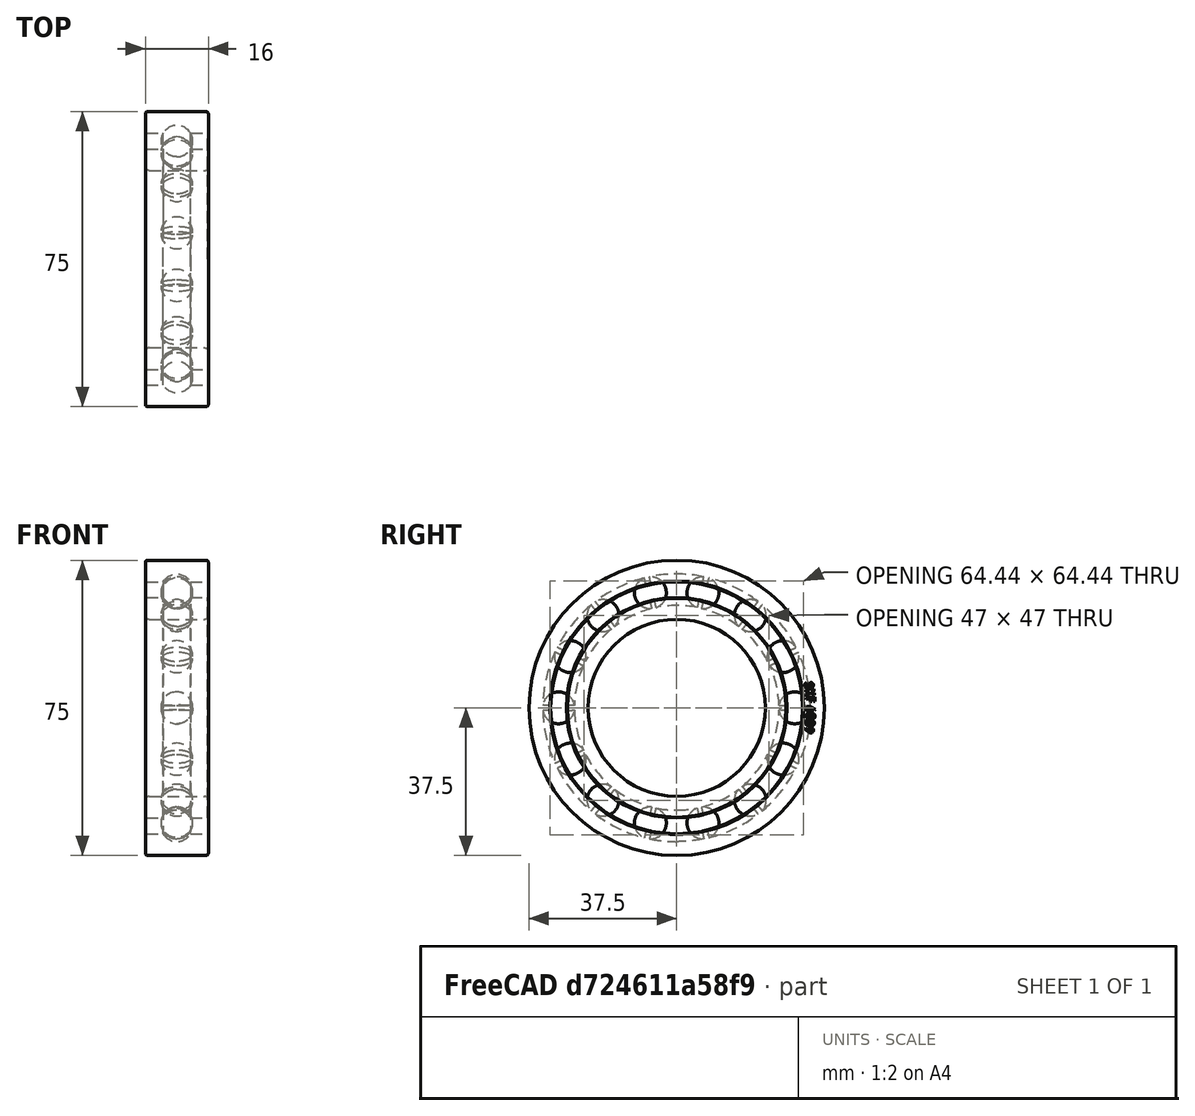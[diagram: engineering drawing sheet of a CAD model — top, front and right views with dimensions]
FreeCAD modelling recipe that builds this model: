
FCSTD DOCUMENT  (FreeCAD 0.21R33675 (Git))
Label: recicladora
License: Creative Commons Attribution-ShareAlike
LicenseURL: http://creativecommons.org/licenses/by-sa/4.0/
objects: App::Link×158, App::DocumentObjectGroup×3, App::FeaturePython×2, PartDesign::CoordinateSystem×2, App::Part×2, Part::Feature×1
note: 3 computed .brp shape members not serialized (recipe doc carries the construction recipe); baked Part::Feature solids carry a one-line shape summary decoded from their .brp
EXTERNAL_REF file=recicladora_eje.FCStd obj=LCS_eje_central_entrada
EXTERNAL_REF file=recicladora_eje.FCStd obj=EjeCentral
EXTERNAL_REF file=recicladora_eje.FCStd obj=LCS_eje_central_salida
EXTERNAL_REF file=recicladora_cuchillas.FCStd obj=LCS_separador_entrada
EXTERNAL_REF file=recicladora_cuchillas.FCStd obj=Body007
EXTERNAL_REF file=recicladora_piezas_fijas.FCStd obj=LCS_placa_caja_salida
EXTERNAL_REF file=recicladora_piezas_fijas.FCStd obj=CuchillaFija001
EXTERNAL_REF file=recicladora_piezas_fijas.FCStd obj=LCS_eje_central
EXTERNAL_REF file=recicladora_piezas_fijas.FCStd obj=Body
EXTERNAL_REF file=recicladora_piezas_fijas.FCStd obj=LCS_cuchilla_fija_separador_salida
EXTERNAL_REF file=recicladora_piezas_fijas.FCStd obj=LCS_eje_central001
EXTERNAL_REF file=recicladora_piezas_fijas.FCStd obj=CuchillaFija
EXTERNAL_REF file=recicladora_piezas_fijas.FCStd obj=LCS_cuchilla_fija_salida
EXTERNAL_REF file=recicladora_cuchillas.FCStd obj=LCS_separador
EXTERNAL_REF file=recicladora_cuchillas.FCStd obj=Body008
EXTERNAL_REF file=recicladora_cuchillas.FCStd obj=LCS_cuchilla_entrada
EXTERNAL_REF file=recicladora_cuchillas.FCStd obj=LCS_separador_salida
EXTERNAL_REF file=recicladora_cuchillas.FCStd obj=Body001
EXTERNAL_REF file=recicladora_cuchillas.FCStd obj=LCS_cuchilla_salida
EXTERNAL_REF file=recicladora_cuchillas.FCStd obj=LCS_cuchilla_entrada001
EXTERNAL_REF file=recicladora_cuchillas.FCStd obj=Body009
EXTERNAL_REF file=recicladora_cuchillas.FCStd obj=LCS_cuchilla_salida001
EXTERNAL_REF file=recicladora_cuchillas.FCStd obj=LCS_cuchilla_entrada002
EXTERNAL_REF file=recicladora_cuchillas.FCStd obj=Body010
EXTERNAL_REF file=recicladora_cuchillas.FCStd obj=LCS_cuchilla_salida002
EXTERNAL_REF file=recicladora_cuchillas.FCStd obj=LCS_cuchilla_entrada003
EXTERNAL_REF file=recicladora_cuchillas.FCStd obj=Body011
EXTERNAL_REF file=recicladora_cuchillas.FCStd obj=LCS_cuchilla_salida003
EXTERNAL_REF file=recicladora_cuchillas.FCStd obj=LCS_cuchilla_entrada004
EXTERNAL_REF file=recicladora_cuchillas.FCStd obj=Body012
EXTERNAL_REF file=recicladora_cuchillas.FCStd obj=LCS_cuchilla_salida004
EXTERNAL_REF file=recicladora_cuchillas.FCStd obj=LCS_cuchilla_entrada005
EXTERNAL_REF file=recicladora_cuchillas.FCStd obj=Body013
EXTERNAL_REF file=recicladora_cuchillas.FCStd obj=LCS_cuchilla_salida005
EXTERNAL_REF file=recicladora_piezas_fijas.FCStd obj=LCS_eje_central003
EXTERNAL_REF file=recicladora_piezas_fijas.FCStd obj=CuchillaFija002
EXTERNAL_REF file=recicladora_cuchillas.FCStd obj=LCS_separador_entrada001
EXTERNAL_REF file=recicladora_cuchillas.FCStd obj=Body014
EXTERNAL_REF file=recicladora_piezas_fijas.FCStd obj=LCS_Placa_Fondo_Entrada
EXTERNAL_REF file=recicladora_piezas_fijas.FCStd obj=LCS_Placa_Salida_Fondo
EXTERNAL_REF file=recicladora_piezas_fijas.FCStd obj=Body001
EXTERNAL_REF file=recicladora_piezas_fijas.FCStd obj=LCS_Placa_Union_Entrada
EXTERNAL_REF file=recicladora_piezas_fijas.FCStd obj=LCS_Placa_union_salida
EXTERNAL_REF file=recicladora_piezas_fijas.FCStd obj=Body002
EXTERNAL_REF file=recicladora_piezas_fijas.FCStd obj=LCS_Paca_union_entrada_2
EXTERNAL_REF file=recicladora_piezas_fijas.FCStd obj=LCS_Placa_union_salida001

FEATURE [App::FeaturePython] dd  # WARN: FeaturePython — macro-defined, semantics opaque (R4)
  DynamicData = Created with DynamicData (v2.46) workbench. | This is a simple container object built | for holding custom properties.
  ddAnchoHex = 25
  ddAnchoPlaca = 3
  ddDiametroExternoHex = 28.8675
  ddDiametroUnion = 10
  ddLargoCono = 18.8675
  ddLargoEje = 100
  ddLargoUnion = 20
  expr: ddDiametroExternoHex = ddAnchoHex / cos(30)
  expr: ddLargoCono = ddDiametroExternoHex - ddDiametroUnion
FEATURE [PartDesign::CoordinateSystem] LCS_Origin
  AttacherType = Attacher::AttachEngine3D
  MapMode = 2
  Support = -> [X_Axis001]
FEATURE [App::DocumentObjectGroup] Constraints
FEATURE [App::FeaturePython] Variables  # WARN: FeaturePython — macro-defined, semantics opaque (R4)
  Type = App::PropertyContainer
  angulo = 6
FEATURE [App::DocumentObjectGroup] Configurations
FEATURE [Part::Feature] Part__Feature  label="45mm Bearing SKF 6009 (RS 286-7754)"
  shape: bbox 16 x 81.18 x 81.18 mm, 195 faces (baked)
FEATURE [PartDesign::CoordinateSystem] LCS_0  label="LCS_rodamiento"
  AttacherType = Attacher::AttachEngine3D
  MapMode = 11
  Placement = pos=(1e-15,0,-7.1e-15) rot=(0.57735,0.57735,-0.57735;4.18879rad)
  Support = -> [Part__Feature]
FEATURE [App::Part] Rodamiento
  Group = -> [LCS_0,Part__Feature]
  Origin = -> Origin
FEATURE [App::DocumentObjectGroup] Parts
  Group = -> [Rodamiento]
FEATURE [App::Link] EjeCentral
  AssemblyType = Part::Link
  AttachedBy = #LCS_eje_central_entrada
  AttachedTo = Parent Assembly#LCS_Origin
  AttachmentOffset = pos=(0,0,0) rot=(0,0,1;0.418879rad)
  LinkPlacement = pos=(2e-16,1e-16,85.5354) rot=(0,0,-1;1.15192rad)
  LinkedObject = -> <external recicladora_eje.FCStd>#EjeCentral
  Placement = pos=(2e-16,1e-16,85.5354) rot=(0,0,-1;1.15192rad)
  SolverId = Asm4EE
  expr: .AttachmentOffset.Rotation.Angle = -Variables.angulo + 30
  expr: Placement = LCS_Origin.Placement * AttachmentOffset * recicladora_eje#LCS_eje_central_entrada.Placement ^ -1
FEATURE [App::Link] Rodamiento001
  AssemblyType = Part::Link
  AttachedBy = #LCS_0
  AttachedTo = EjeCentral#LCS_eje_central_salida
  AttachmentOffset = pos=(0,0,-13) rot=(0,0,1;0rad)
  LinkPlacement = pos=(-3.7e-15,-1.7e-15,72.5354) rot=(0.699253,0.148631,-0.699253;2.84649rad)
  LinkedObject = -> Rodamiento
  Placement = pos=(-3.7e-15,-1.7e-15,72.5354) rot=(0.699253,0.148631,-0.699253;2.84649rad)
  SolverId = Asm4EE
  expr: Placement = EjeCentral.Placement * recicladora_eje#LCS_eje_central_salida.Placement * AttachmentOffset * LCS_0.Placement ^ -1
FEATURE [App::Link] SeparadorCuchillaInicial
  AssemblyType = Part::Link
  AttachedBy = #LCS_separador_entrada
  AttachedTo = EjeCentral#LCS_eje_central_salida
  AttachmentOffset = pos=(0,0,0) rot=(0,0,1;0.10472rad)
  LinkPlacement = pos=(-2.9e-15,-1.7e-15,85.5354) rot=(0,0,-1;2.61799rad)
  LinkedObject = -> <external recicladora_cuchillas.FCStd>#Body007
  Placement = pos=(-2.9e-15,-1.7e-15,85.5354) rot=(0,0,-1;2.61799rad)
  SolverId = Asm4EE
  expr: .AttachmentOffset.Rotation.Angle = Variables.angulo
  expr: Placement = EjeCentral.Placement * recicladora_eje#LCS_eje_central_salida.Placement * AttachmentOffset * recicladora_cuchillas#LCS_separador_entrada.Placement ^ -1
FEATURE [App::Link] PlacaCaja
  AssemblyType = Part::Link
  AttachedBy = #LCS_placa_caja_salida
  AttachedTo = Parent Assembly#LCS_Origin
  AttachmentOffset = pos=(0,0,88.535) rot=(0,0,1;0rad)
  LinkPlacement = pos=(65,-65,87.035) rot=(0,0,1;0rad)
  LinkedObject = -> <external recicladora_piezas_fijas.FCStd>#CuchillaFija001
  Placement = pos=(65,-65,87.035) rot=(0,0,1;0rad)
  SolverId = Asm4EE
  expr: Placement = LCS_Origin.Placement * AttachmentOffset * recicladora_piezas_fijas#LCS_placa_caja_salida.Placement ^ -1
FEATURE [App::Link] CuchillaFijaSeparador
  AssemblyType = Part::Link
  AttachedBy = #LCS_eje_central
  AttachedTo = PlacaCaja#LCS_placa_caja_salida
  LinkPlacement = pos=(65,-65,88.535) rot=(0,0,1;0rad)
  LinkedObject = -> <external recicladora_piezas_fijas.FCStd>#Body
  Placement = pos=(65,-65,88.535) rot=(0,0,1;0rad)
  SolverId = Asm4EE
  expr: Placement = PlacaCaja.Placement * recicladora_piezas_fijas#LCS_placa_caja_salida.Placement * AttachmentOffset * recicladora_piezas_fijas#LCS_eje_central.Placement ^ -1
FEATURE [App::Link] CuchillaFija
  AssemblyType = Part::Link
  AttachedBy = #LCS_eje_central001
  AttachedTo = CuchillaFijaSeparador#LCS_cuchilla_fija_separador_salida
  LinkPlacement = pos=(65,-65,90.035) rot=(0,0,1;0rad)
  LinkedObject = -> <external recicladora_piezas_fijas.FCStd>#CuchillaFija
  Placement = pos=(65,-65,90.035) rot=(0,0,1;0rad)
  SolverId = Asm4EE
  expr: Placement = CuchillaFijaSeparador.Placement * recicladora_piezas_fijas#LCS_cuchilla_fija_separador_salida.Placement * AttachmentOffset * recicladora_piezas_fijas#LCS_eje_central001.Placement ^ -1
FEATURE [App::Link] CuchillaFijaSeparador001
  AssemblyType = Part::Link
  AttachedBy = #LCS_eje_central
  AttachedTo = CuchillaFija#LCS_cuchilla_fija_salida
  LinkPlacement = pos=(65,-65,91.535) rot=(0,0,1;0rad)
  LinkedObject = -> <external recicladora_piezas_fijas.FCStd>#Body
  Placement = pos=(65,-65,91.535) rot=(0,0,1;0rad)
  SolverId = Asm4EE
  expr: Placement = CuchillaFija.Placement * recicladora_piezas_fijas#LCS_cuchilla_fija_salida.Placement * AttachmentOffset * recicladora_piezas_fijas#LCS_eje_central.Placement ^ -1
FEATURE [App::Link] CuchillaFija001
  AssemblyType = Part::Link
  AttachedBy = #LCS_eje_central001
  AttachedTo = CuchillaFijaSeparador001#LCS_cuchilla_fija_separador_salida
  LinkPlacement = pos=(65,-65,93.035) rot=(0,0,1;0rad)
  LinkedObject = -> <external recicladora_piezas_fijas.FCStd>#CuchillaFija
  Placement = pos=(65,-65,93.035) rot=(0,0,1;0rad)
  SolverId = Asm4EE
  expr: Placement = CuchillaFijaSeparador001.Placement * recicladora_piezas_fijas#LCS_cuchilla_fija_separador_salida.Placement * AttachmentOffset * recicladora_piezas_fijas#LCS_eje_central001.Placement ^ -1
FEATURE [App::Link] CuchillaFijaSeparador002
  AssemblyType = Part::Link
  AttachedBy = #LCS_eje_central
  AttachedTo = CuchillaFija001#LCS_cuchilla_fija_salida
  LinkPlacement = pos=(65,-65,94.535) rot=(0,0,1;0rad)
  LinkedObject = -> <external recicladora_piezas_fijas.FCStd>#Body
  Placement = pos=(65,-65,94.535) rot=(0,0,1;0rad)
  SolverId = Asm4EE
  expr: Placement = CuchillaFija001.Placement * recicladora_piezas_fijas#LCS_cuchilla_fija_salida.Placement * AttachmentOffset * recicladora_piezas_fijas#LCS_eje_central.Placement ^ -1
FEATURE [App::Link] CuchillaFija002
  AssemblyType = Part::Link
  AttachedBy = #LCS_eje_central001
  AttachedTo = CuchillaFijaSeparador002#LCS_cuchilla_fija_separador_salida
  LinkPlacement = pos=(65,-65,96.035) rot=(0,0,1;0rad)
  LinkedObject = -> <external recicladora_piezas_fijas.FCStd>#CuchillaFija
  Placement = pos=(65,-65,96.035) rot=(0,0,1;0rad)
  SolverId = Asm4EE
  expr: Placement = CuchillaFijaSeparador002.Placement * recicladora_piezas_fijas#LCS_cuchilla_fija_separador_salida.Placement * AttachmentOffset * recicladora_piezas_fijas#LCS_eje_central001.Placement ^ -1
FEATURE [App::Link] CuchillaFijaSeparador003
  AssemblyType = Part::Link
  AttachedBy = #LCS_eje_central
  AttachedTo = CuchillaFija002#LCS_cuchilla_fija_salida
  LinkPlacement = pos=(65,-65,97.535) rot=(0,0,1;0rad)
  LinkedObject = -> <external recicladora_piezas_fijas.FCStd>#Body
  Placement = pos=(65,-65,97.535) rot=(0,0,1;0rad)
  SolverId = Asm4EE
  expr: Placement = CuchillaFija002.Placement * recicladora_piezas_fijas#LCS_cuchilla_fija_salida.Placement * AttachmentOffset * recicladora_piezas_fijas#LCS_eje_central.Placement ^ -1
FEATURE [App::Link] CuchillaFija003
  AssemblyType = Part::Link
  AttachedBy = #LCS_eje_central001
  AttachedTo = CuchillaFijaSeparador003#LCS_cuchilla_fija_separador_salida
  LinkPlacement = pos=(65,-65,99.035) rot=(0,0,1;0rad)
  LinkedObject = -> <external recicladora_piezas_fijas.FCStd>#CuchillaFija
  Placement = pos=(65,-65,99.035) rot=(0,0,1;0rad)
  SolverId = Asm4EE
  expr: Placement = CuchillaFijaSeparador003.Placement * recicladora_piezas_fijas#LCS_cuchilla_fija_separador_salida.Placement * AttachmentOffset * recicladora_piezas_fijas#LCS_eje_central001.Placement ^ -1
FEATURE [App::Link] SeparadorCuchilla
  AssemblyType = Part::Link
  AttachedBy = #LCS_separador
  AttachedTo = PlacaCaja#LCS_placa_caja_salida
  AttachmentOffset = pos=(0,0,0) rot=(0,0,1;-0.10472rad)
  LinkPlacement = pos=(-1e-16,-1e-16,90.035) rot=(0.669131,-0.743145,0;3.14159rad)
  LinkedObject = -> <external recicladora_cuchillas.FCStd>#Body008
  Placement = pos=(-1e-16,-1e-16,90.035) rot=(0.669131,-0.743145,0;3.14159rad)
  SolverId = Asm4EE
  expr: .AttachmentOffset.Rotation.Angle = -Variables.angulo
  expr: Placement = PlacaCaja.Placement * recicladora_piezas_fijas#LCS_placa_caja_salida.Placement * AttachmentOffset * recicladora_cuchillas#LCS_separador.Placement ^ -1
FEATURE [App::Link] Cuchilla001
  AssemblyType = Part::Link
  AttachedBy = #LCS_cuchilla_entrada
  AttachedTo = SeparadorCuchilla#LCS_separador_salida
  LinkPlacement = pos=(-4e-16,-3.6e-15,90.035) rot=(0,0,1;4.60767rad)
  LinkedObject = -> <external recicladora_cuchillas.FCStd>#Body001
  Placement = pos=(-4e-16,-3.6e-15,90.035) rot=(0,0,1;4.60767rad)
  SolverId = Asm4EE
  expr: Placement = SeparadorCuchilla.Placement * recicladora_cuchillas#LCS_separador_salida.Placement * AttachmentOffset * recicladora_cuchillas#LCS_cuchilla_entrada.Placement ^ -1
FEATURE [App::Link] SeparadorCuchilla001
  AssemblyType = Part::Link
  AttachedBy = #LCS_separador
  AttachedTo = Cuchilla001#LCS_cuchilla_salida
  LinkPlacement = pos=(-4e-16,-3e-16,93.035) rot=(0.669131,-0.743145,0;3.14159rad)
  LinkedObject = -> <external recicladora_cuchillas.FCStd>#Body008
  Placement = pos=(-4e-16,-3e-16,93.035) rot=(0.669131,-0.743145,0;3.14159rad)
  SolverId = Asm4EE
  expr: Placement = Cuchilla001.Placement * recicladora_cuchillas#LCS_cuchilla_salida.Placement * AttachmentOffset * recicladora_cuchillas#LCS_separador.Placement ^ -1
FEATURE [App::Link] Cuchilla002
  AssemblyType = Part::Link
  AttachedBy = #LCS_cuchilla_entrada001
  AttachedTo = SeparadorCuchilla001#LCS_separador_salida
  LinkPlacement = pos=(-1e-15,-3.9e-15,93.035) rot=(0,0,1;4.43314rad)
  LinkedObject = -> <external recicladora_cuchillas.FCStd>#Body009
  Placement = pos=(-1e-15,-3.9e-15,93.035) rot=(0,0,1;4.43314rad)
  SolverId = Asm4EE
  expr: Placement = SeparadorCuchilla001.Placement * recicladora_cuchillas#LCS_separador_salida.Placement * AttachmentOffset * recicladora_cuchillas#LCS_cuchilla_entrada001.Placement ^ -1
FEATURE [App::Link] SeparadorCuchilla002
  AssemblyType = Part::Link
  AttachedBy = #LCS_separador
  AttachedTo = Cuchilla002#LCS_cuchilla_salida001
  LinkPlacement = pos=(-1.1e-15,-9e-16,96.035) rot=(0.669131,-0.743145,0;3.14159rad)
  LinkedObject = -> <external recicladora_cuchillas.FCStd>#Body008
  Placement = pos=(-1.1e-15,-9e-16,96.035) rot=(0.669131,-0.743145,0;3.14159rad)
  SolverId = Asm4EE
  expr: Placement = Cuchilla002.Placement * recicladora_cuchillas#LCS_cuchilla_salida001.Placement * AttachmentOffset * recicladora_cuchillas#LCS_separador.Placement ^ -1
FEATURE [App::Link] Cuchilla003
  AssemblyType = Part::Link
  AttachedBy = #LCS_cuchilla_entrada002
  AttachedTo = SeparadorCuchilla002#LCS_separador_salida
  LinkPlacement = pos=(-1.8e-15,-4.4e-15,96.035) rot=(0,0,1;4.2586rad)
  LinkedObject = -> <external recicladora_cuchillas.FCStd>#Body010
  Placement = pos=(-1.8e-15,-4.4e-15,96.035) rot=(0,0,1;4.2586rad)
  SolverId = Asm4EE
  expr: Placement = SeparadorCuchilla002.Placement * recicladora_cuchillas#LCS_separador_salida.Placement * AttachmentOffset * recicladora_cuchillas#LCS_cuchilla_entrada002.Placement ^ -1
FEATURE [App::Link] SeparadorCuchilla003
  AssemblyType = Part::Link
  AttachedBy = #LCS_separador
  AttachedTo = Cuchilla003#LCS_cuchilla_salida002
  LinkPlacement = pos=(-2e-15,-1.6e-15,99.035) rot=(0.669131,-0.743145,0;3.14159rad)
  LinkedObject = -> <external recicladora_cuchillas.FCStd>#Body008
  Placement = pos=(-2e-15,-1.6e-15,99.035) rot=(0.669131,-0.743145,0;3.14159rad)
  SolverId = Asm4EE
  expr: Placement = Cuchilla003.Placement * recicladora_cuchillas#LCS_cuchilla_salida002.Placement * AttachmentOffset * recicladora_cuchillas#LCS_separador.Placement ^ -1
FEATURE [App::Link] Cuchilla004
  AssemblyType = Part::Link
  AttachedBy = #LCS_cuchilla_entrada003
  AttachedTo = SeparadorCuchilla003#LCS_separador_salida
  LinkPlacement = pos=(-2.6e-15,-5.5e-15,99.035) rot=(0,0,1;4.08407rad)
  LinkedObject = -> <external recicladora_cuchillas.FCStd>#Body011
  Placement = pos=(-2.6e-15,-5.5e-15,99.035) rot=(0,0,1;4.08407rad)
  SolverId = Asm4EE
  expr: Placement = SeparadorCuchilla003.Placement * recicladora_cuchillas#LCS_separador_salida.Placement * AttachmentOffset * recicladora_cuchillas#LCS_cuchilla_entrada003.Placement ^ -1
FEATURE [App::Link] SeparadorCuchilla004
  AssemblyType = Part::Link
  AttachedBy = #LCS_separador
  AttachedTo = Cuchilla004#LCS_cuchilla_salida003
  LinkPlacement = pos=(-3.2e-15,-2.6e-15,102.035) rot=(0.669131,-0.743145,0;3.14159rad)
  LinkedObject = -> <external recicladora_cuchillas.FCStd>#Body008
  Placement = pos=(-3.2e-15,-2.6e-15,102.035) rot=(0.669131,-0.743145,0;3.14159rad)
  SolverId = Asm4EE
  expr: Placement = Cuchilla004.Placement * recicladora_cuchillas#LCS_cuchilla_salida003.Placement * AttachmentOffset * recicladora_cuchillas#LCS_separador.Placement ^ -1
FEATURE [App::Link] Cuchilla005
  AssemblyType = Part::Link
  AttachedBy = #LCS_cuchilla_entrada004
  AttachedTo = SeparadorCuchilla004#LCS_separador_salida
  LinkPlacement = pos=(-3.2e-15,-2.6e-15,102.035) rot=(0,0,1;3.90954rad)
  LinkedObject = -> <external recicladora_cuchillas.FCStd>#Body012
  Placement = pos=(-3.2e-15,-2.6e-15,102.035) rot=(0,0,1;3.90954rad)
  SolverId = Asm4EE
  expr: Placement = SeparadorCuchilla004.Placement * recicladora_cuchillas#LCS_separador_salida.Placement * AttachmentOffset * recicladora_cuchillas#LCS_cuchilla_entrada004.Placement ^ -1
FEATURE [App::Link] SeparadorCuchilla005
  AssemblyType = Part::Link
  AttachedBy = #LCS_separador
  AttachedTo = Cuchilla005#LCS_cuchilla_salida004
  LinkPlacement = pos=(-4.7e-15,-3.8e-15,105.035) rot=(0.669131,-0.743145,0;3.14159rad)
  LinkedObject = -> <external recicladora_cuchillas.FCStd>#Body008
  Placement = pos=(-4.7e-15,-3.8e-15,105.035) rot=(0.669131,-0.743145,0;3.14159rad)
  SolverId = Asm4EE
  expr: Placement = Cuchilla005.Placement * recicladora_cuchillas#LCS_cuchilla_salida004.Placement * AttachmentOffset * recicladora_cuchillas#LCS_separador.Placement ^ -1
FEATURE [App::Link] Cuchilla006
  AssemblyType = Part::Link
  AttachedBy = #LCS_cuchilla_entrada005
  AttachedTo = SeparadorCuchilla005#LCS_separador_salida
  LinkPlacement = pos=(-5.2e-15,-6.3e-15,105.035) rot=(0,0,1;3.73501rad)
  LinkedObject = -> <external recicladora_cuchillas.FCStd>#Body013
  Placement = pos=(-5.2e-15,-6.3e-15,105.035) rot=(0,0,1;3.73501rad)
  SolverId = Asm4EE
  expr: Placement = SeparadorCuchilla005.Placement * recicladora_cuchillas#LCS_separador_salida.Placement * AttachmentOffset * recicladora_cuchillas#LCS_cuchilla_entrada005.Placement ^ -1
FEATURE [App::Link] SeparadorCuchilla006
  AssemblyType = Part::Link
  AttachedBy = #LCS_separador
  AttachedTo = Cuchilla006#LCS_cuchilla_salida005
  LinkPlacement = pos=(-6.5e-15,-5.3e-15,108.035) rot=(0.669131,-0.743145,0;3.14159rad)
  LinkedObject = -> <external recicladora_cuchillas.FCStd>#Body008
  Placement = pos=(-6.5e-15,-5.3e-15,108.035) rot=(0.669131,-0.743145,0;3.14159rad)
  SolverId = Asm4EE
  expr: Placement = Cuchilla006.Placement * recicladora_cuchillas#LCS_cuchilla_salida005.Placement * AttachmentOffset * recicladora_cuchillas#LCS_separador.Placement ^ -1
FEATURE [App::Link] Cuchilla001001
  AssemblyType = Part::Link
  AttachedBy = #LCS_cuchilla_entrada
  AttachedTo = SeparadorCuchilla006#LCS_separador_salida
  AttachmentOffset = pos=(0,0,0) rot=(0,0,1;-1.0472rad)
  LinkPlacement = pos=(-9.7e-15,-6.7e-15,108.035) rot=(0,0,-1;2.72271rad)
  LinkedObject = -> <external recicladora_cuchillas.FCStd>#Body001
  Placement = pos=(-9.7e-15,-6.7e-15,108.035) rot=(0,0,-1;2.72271rad)
  SolverId = Asm4EE
  expr: Placement = SeparadorCuchilla006.Placement * recicladora_cuchillas#LCS_separador_salida.Placement * AttachmentOffset * recicladora_cuchillas#LCS_cuchilla_entrada.Placement ^ -1
FEATURE [App::Link] SeparadorCuchilla007
  AssemblyType = Part::Link
  AttachedBy = #LCS_separador
  AttachedTo = Cuchilla001001#LCS_cuchilla_salida
  LinkPlacement = pos=(-8.6e-15,-6.8e-15,111.035) rot=(-0.207912,0.978148,0;3.14159rad)
  LinkedObject = -> <external recicladora_cuchillas.FCStd>#Body008
  Placement = pos=(-8.6e-15,-6.8e-15,111.035) rot=(-0.207912,0.978148,0;3.14159rad)
  SolverId = Asm4EE
  expr: Placement = Cuchilla001001.Placement * recicladora_cuchillas#LCS_cuchilla_salida.Placement * AttachmentOffset * recicladora_cuchillas#LCS_separador.Placement ^ -1
FEATURE [App::Link] Cuchilla002001
  AssemblyType = Part::Link
  AttachedBy = #LCS_cuchilla_entrada001
  AttachedTo = SeparadorCuchilla007#LCS_separador_salida
  LinkPlacement = pos=(-1.19e-14,-8.1e-15,111.035) rot=(0,0,-1;2.89725rad)
  LinkedObject = -> <external recicladora_cuchillas.FCStd>#Body009
  Placement = pos=(-1.19e-14,-8.1e-15,111.035) rot=(0,0,-1;2.89725rad)
  SolverId = Asm4EE
  expr: Placement = SeparadorCuchilla007.Placement * recicladora_cuchillas#LCS_separador_salida.Placement * AttachmentOffset * recicladora_cuchillas#LCS_cuchilla_entrada001.Placement ^ -1
FEATURE [App::Link] SeparadorCuchilla008
  AssemblyType = Part::Link
  AttachedBy = #LCS_separador
  AttachedTo = Cuchilla002001#LCS_cuchilla_salida001
  LinkPlacement = pos=(-1.1e-14,-8.3e-15,114.035) rot=(-0.207912,0.978148,0;3.14159rad)
  LinkedObject = -> <external recicladora_cuchillas.FCStd>#Body008
  Placement = pos=(-1.1e-14,-8.3e-15,114.035) rot=(-0.207912,0.978148,0;3.14159rad)
  SolverId = Asm4EE
  expr: Placement = Cuchilla002001.Placement * recicladora_cuchillas#LCS_cuchilla_salida001.Placement * AttachmentOffset * recicladora_cuchillas#LCS_separador.Placement ^ -1
FEATURE [App::Link] Cuchilla003001
  AssemblyType = Part::Link
  AttachedBy = #LCS_cuchilla_entrada002
  AttachedTo = SeparadorCuchilla008#LCS_separador_salida
  LinkPlacement = pos=(-1.45e-14,-9.4e-15,114.035) rot=(0,0,-1;3.07178rad)
  LinkedObject = -> <external recicladora_cuchillas.FCStd>#Body010
  Placement = pos=(-1.45e-14,-9.4e-15,114.035) rot=(0,0,-1;3.07178rad)
  SolverId = Asm4EE
  expr: Placement = SeparadorCuchilla008.Placement * recicladora_cuchillas#LCS_separador_salida.Placement * AttachmentOffset * recicladora_cuchillas#LCS_cuchilla_entrada002.Placement ^ -1
FEATURE [App::Link] SeparadorCuchilla009
  AssemblyType = Part::Link
  AttachedBy = #LCS_separador
  AttachedTo = Cuchilla003001#LCS_cuchilla_salida002
  LinkPlacement = pos=(-1.38e-14,-9.6e-15,117.035) rot=(-0.207912,0.978148,0;3.14159rad)
  LinkedObject = -> <external recicladora_cuchillas.FCStd>#Body008
  Placement = pos=(-1.38e-14,-9.6e-15,117.035) rot=(-0.207912,0.978148,0;3.14159rad)
  SolverId = Asm4EE
  expr: Placement = Cuchilla003001.Placement * recicladora_cuchillas#LCS_cuchilla_salida002.Placement * AttachmentOffset * recicladora_cuchillas#LCS_separador.Placement ^ -1
FEATURE [App::Link] Cuchilla004001
  AssemblyType = Part::Link
  AttachedBy = #LCS_cuchilla_entrada003
  AttachedTo = SeparadorCuchilla009#LCS_separador_salida
  LinkPlacement = pos=(-1.75e-14,-1.1e-14,117.035) rot=(0,0,-1;3.24631rad)
  LinkedObject = -> <external recicladora_cuchillas.FCStd>#Body011
  Placement = pos=(-1.75e-14,-1.1e-14,117.035) rot=(0,0,-1;3.24631rad)
  SolverId = Asm4EE
  expr: Placement = SeparadorCuchilla009.Placement * recicladora_cuchillas#LCS_separador_salida.Placement * AttachmentOffset * recicladora_cuchillas#LCS_cuchilla_entrada003.Placement ^ -1
FEATURE [App::Link] SeparadorCuchilla010
  AssemblyType = Part::Link
  AttachedBy = #LCS_separador
  AttachedTo = Cuchilla004001#LCS_cuchilla_salida003
  LinkPlacement = pos=(-1.69e-14,-1.08e-14,120.035) rot=(-0.207912,0.978148,0;3.14159rad)
  LinkedObject = -> <external recicladora_cuchillas.FCStd>#Body008
  Placement = pos=(-1.69e-14,-1.08e-14,120.035) rot=(-0.207912,0.978148,0;3.14159rad)
  SolverId = Asm4EE
  expr: Placement = Cuchilla004001.Placement * recicladora_cuchillas#LCS_cuchilla_salida003.Placement * AttachmentOffset * recicladora_cuchillas#LCS_separador.Placement ^ -1
FEATURE [App::Link] Cuchilla005001
  AssemblyType = Part::Link
  AttachedBy = #LCS_cuchilla_entrada004
  AttachedTo = SeparadorCuchilla010#LCS_separador_salida
  LinkPlacement = pos=(-1.69e-14,-1.08e-14,120.035) rot=(0,0,-1;3.42084rad)
  LinkedObject = -> <external recicladora_cuchillas.FCStd>#Body012
  Placement = pos=(-1.69e-14,-1.08e-14,120.035) rot=(0,0,-1;3.42084rad)
  SolverId = Asm4EE
  expr: Placement = SeparadorCuchilla010.Placement * recicladora_cuchillas#LCS_separador_salida.Placement * AttachmentOffset * recicladora_cuchillas#LCS_cuchilla_entrada004.Placement ^ -1
FEATURE [App::Link] SeparadorCuchilla011
  AssemblyType = Part::Link
  AttachedBy = #LCS_separador
  AttachedTo = Cuchilla005001#LCS_cuchilla_salida004
  LinkPlacement = pos=(-2.03e-14,-1.19e-14,123.035) rot=(-0.207912,0.978148,0;3.14159rad)
  LinkedObject = -> <external recicladora_cuchillas.FCStd>#Body008
  Placement = pos=(-2.03e-14,-1.19e-14,123.035) rot=(-0.207912,0.978148,0;3.14159rad)
  SolverId = Asm4EE
  expr: Placement = Cuchilla005001.Placement * recicladora_cuchillas#LCS_cuchilla_salida004.Placement * AttachmentOffset * recicladora_cuchillas#LCS_separador.Placement ^ -1
FEATURE [App::Link] Cuchilla006001
  AssemblyType = Part::Link
  AttachedBy = #LCS_cuchilla_entrada005
  AttachedTo = SeparadorCuchilla011#LCS_separador_salida
  LinkPlacement = pos=(-2.27e-14,-1.27e-14,123.035) rot=(0,0,-1;3.59538rad)
  LinkedObject = -> <external recicladora_cuchillas.FCStd>#Body013
  Placement = pos=(-2.27e-14,-1.27e-14,123.035) rot=(0,0,-1;3.59538rad)
  SolverId = Asm4EE
  expr: Placement = SeparadorCuchilla011.Placement * recicladora_cuchillas#LCS_separador_salida.Placement * AttachmentOffset * recicladora_cuchillas#LCS_cuchilla_entrada005.Placement ^ -1
FEATURE [App::Link] SeparadorCuchilla012
  AssemblyType = Part::Link
  AttachedBy = #LCS_separador
  AttachedTo = Cuchilla006001#LCS_cuchilla_salida005
  LinkPlacement = pos=(-2.41e-14,-1.28e-14,126.035) rot=(-0.207912,0.978148,0;3.14159rad)
  LinkedObject = -> <external recicladora_cuchillas.FCStd>#Body008
  Placement = pos=(-2.41e-14,-1.28e-14,126.035) rot=(-0.207912,0.978148,0;3.14159rad)
  SolverId = Asm4EE
  expr: Placement = Cuchilla006001.Placement * recicladora_cuchillas#LCS_cuchilla_salida005.Placement * AttachmentOffset * recicladora_cuchillas#LCS_separador.Placement ^ -1
FEATURE [App::Link] Cuchilla001002
  AssemblyType = Part::Link
  AttachedBy = #LCS_cuchilla_entrada
  AttachedTo = SeparadorCuchilla012#LCS_separador_salida
  AttachmentOffset = pos=(0,0,0) rot=(0,0,1;-1.0472rad)
  LinkPlacement = pos=(-2.7e-14,-1.07e-14,126.035) rot=(0,0,1;2.51327rad)
  LinkedObject = -> <external recicladora_cuchillas.FCStd>#Body001
  Placement = pos=(-2.7e-14,-1.07e-14,126.035) rot=(0,0,1;2.51327rad)
  SolverId = Asm4EE
  expr: Placement = SeparadorCuchilla012.Placement * recicladora_cuchillas#LCS_separador_salida.Placement * AttachmentOffset * recicladora_cuchillas#LCS_cuchilla_entrada.Placement ^ -1
FEATURE [App::Link] SeparadorCuchilla013
  AssemblyType = Part::Link
  AttachedBy = #LCS_separador
  AttachedTo = Cuchilla001002#LCS_cuchilla_salida
  LinkPlacement = pos=(-2.82e-14,-1.35e-14,129.035) rot=(-0.309017,-0.951057,0;3.14159rad)
  LinkedObject = -> <external recicladora_cuchillas.FCStd>#Body008
  Placement = pos=(-2.82e-14,-1.35e-14,129.035) rot=(-0.309017,-0.951057,0;3.14159rad)
  SolverId = Asm4EE
  expr: Placement = Cuchilla001002.Placement * recicladora_cuchillas#LCS_cuchilla_salida.Placement * AttachmentOffset * recicladora_cuchillas#LCS_separador.Placement ^ -1
FEATURE [App::Link] Cuchilla002002
  AssemblyType = Part::Link
  AttachedBy = #LCS_cuchilla_entrada001
  AttachedTo = SeparadorCuchilla013#LCS_separador_salida
  LinkPlacement = pos=(-3.1e-14,-1.13e-14,129.035) rot=(0,0,1;2.33874rad)
  LinkedObject = -> <external recicladora_cuchillas.FCStd>#Body009
  Placement = pos=(-3.1e-14,-1.13e-14,129.035) rot=(0,0,1;2.33874rad)
  SolverId = Asm4EE
  expr: Placement = SeparadorCuchilla013.Placement * recicladora_cuchillas#LCS_separador_salida.Placement * AttachmentOffset * recicladora_cuchillas#LCS_cuchilla_entrada001.Placement ^ -1
FEATURE [App::Link] SeparadorCuchilla014
  AssemblyType = Part::Link
  AttachedBy = #LCS_separador
  AttachedTo = Cuchilla002002#LCS_cuchilla_salida001
  LinkPlacement = pos=(-3.23e-14,-1.39e-14,132.035) rot=(-0.309017,-0.951057,0;3.14159rad)
  LinkedObject = -> <external recicladora_cuchillas.FCStd>#Body008
  Placement = pos=(-3.23e-14,-1.39e-14,132.035) rot=(-0.309017,-0.951057,0;3.14159rad)
  SolverId = Asm4EE
  expr: Placement = Cuchilla002002.Placement * recicladora_cuchillas#LCS_cuchilla_salida001.Placement * AttachmentOffset * recicladora_cuchillas#LCS_separador.Placement ^ -1
FEATURE [App::Link] Cuchilla003002
  AssemblyType = Part::Link
  AttachedBy = #LCS_cuchilla_entrada002
  AttachedTo = SeparadorCuchilla014#LCS_separador_salida
  LinkPlacement = pos=(-3.51e-14,-1.15e-14,132.035) rot=(0,0,1;2.16421rad)
  LinkedObject = -> <external recicladora_cuchillas.FCStd>#Body010
  Placement = pos=(-3.51e-14,-1.15e-14,132.035) rot=(0,0,1;2.16421rad)
  SolverId = Asm4EE
  expr: Placement = SeparadorCuchilla014.Placement * recicladora_cuchillas#LCS_separador_salida.Placement * AttachmentOffset * recicladora_cuchillas#LCS_cuchilla_entrada002.Placement ^ -1
FEATURE [App::Link] SeparadorCuchilla015
  AssemblyType = Part::Link
  AttachedBy = #LCS_separador
  AttachedTo = Cuchilla003002#LCS_cuchilla_salida002
  LinkPlacement = pos=(-3.65e-14,-1.39e-14,135.035) rot=(-0.309017,-0.951057,0;3.14159rad)
  LinkedObject = -> <external recicladora_cuchillas.FCStd>#Body008
  Placement = pos=(-3.65e-14,-1.39e-14,135.035) rot=(-0.309017,-0.951057,0;3.14159rad)
  SolverId = Asm4EE
  expr: Placement = Cuchilla003002.Placement * recicladora_cuchillas#LCS_cuchilla_salida002.Placement * AttachmentOffset * recicladora_cuchillas#LCS_separador.Placement ^ -1
FEATURE [App::Link] Cuchilla004002
  AssemblyType = Part::Link
  AttachedBy = #LCS_cuchilla_entrada003
  AttachedTo = SeparadorCuchilla015#LCS_separador_salida
  LinkPlacement = pos=(-3.96e-14,-1.14e-14,135.035) rot=(0,0,1;1.98968rad)
  LinkedObject = -> <external recicladora_cuchillas.FCStd>#Body011
  Placement = pos=(-3.96e-14,-1.14e-14,135.035) rot=(0,0,1;1.98968rad)
  SolverId = Asm4EE
  expr: Placement = SeparadorCuchilla015.Placement * recicladora_cuchillas#LCS_separador_salida.Placement * AttachmentOffset * recicladora_cuchillas#LCS_cuchilla_entrada003.Placement ^ -1
FEATURE [App::Link] SeparadorCuchilla016
  AssemblyType = Part::Link
  AttachedBy = #LCS_separador
  AttachedTo = Cuchilla004002#LCS_cuchilla_salida003
  LinkPlacement = pos=(-4.08e-14,-1.36e-14,138.035) rot=(-0.309017,-0.951057,0;3.14159rad)
  LinkedObject = -> <external recicladora_cuchillas.FCStd>#Body008
  Placement = pos=(-4.08e-14,-1.36e-14,138.035) rot=(-0.309017,-0.951057,0;3.14159rad)
  SolverId = Asm4EE
  expr: Placement = Cuchilla004002.Placement * recicladora_cuchillas#LCS_cuchilla_salida003.Placement * AttachmentOffset * recicladora_cuchillas#LCS_separador.Placement ^ -1
FEATURE [App::Link] Cuchilla005002
  AssemblyType = Part::Link
  AttachedBy = #LCS_cuchilla_entrada004
  AttachedTo = SeparadorCuchilla016#LCS_separador_salida
  LinkPlacement = pos=(-4.08e-14,-1.36e-14,138.035) rot=(0,0,1;1.81514rad)
  LinkedObject = -> <external recicladora_cuchillas.FCStd>#Body012
  Placement = pos=(-4.08e-14,-1.36e-14,138.035) rot=(0,0,1;1.81514rad)
  SolverId = Asm4EE
  expr: Placement = SeparadorCuchilla016.Placement * recicladora_cuchillas#LCS_separador_salida.Placement * AttachmentOffset * recicladora_cuchillas#LCS_cuchilla_entrada004.Placement ^ -1
FEATURE [App::Link] SeparadorCuchilla017
  AssemblyType = Part::Link
  AttachedBy = #LCS_separador
  AttachedTo = Cuchilla005002#LCS_cuchilla_salida004
  LinkPlacement = pos=(-4.51e-14,-1.29e-14,141.035) rot=(-0.309017,-0.951057,0;3.14159rad)
  LinkedObject = -> <external recicladora_cuchillas.FCStd>#Body008
  Placement = pos=(-4.51e-14,-1.29e-14,141.035) rot=(-0.309017,-0.951057,0;3.14159rad)
  SolverId = Asm4EE
  expr: Placement = Cuchilla005002.Placement * recicladora_cuchillas#LCS_cuchilla_salida004.Placement * AttachmentOffset * recicladora_cuchillas#LCS_separador.Placement ^ -1
FEATURE [App::Link] Cuchilla006002
  AssemblyType = Part::Link
  AttachedBy = #LCS_cuchilla_entrada005
  AttachedTo = SeparadorCuchilla017#LCS_separador_salida
  LinkPlacement = pos=(-4.7e-14,-1.12e-14,141.035) rot=(0,0,1;1.64061rad)
  LinkedObject = -> <external recicladora_cuchillas.FCStd>#Body013
  Placement = pos=(-4.7e-14,-1.12e-14,141.035) rot=(0,0,1;1.64061rad)
  SolverId = Asm4EE
  expr: Placement = SeparadorCuchilla017.Placement * recicladora_cuchillas#LCS_separador_salida.Placement * AttachmentOffset * recicladora_cuchillas#LCS_cuchilla_entrada005.Placement ^ -1
FEATURE [App::Link] SeparadorCuchilla018
  AssemblyType = Part::Link
  AttachedBy = #LCS_separador
  AttachedTo = Cuchilla006002#LCS_cuchilla_salida005
  LinkPlacement = pos=(-4.94e-14,-1.18e-14,144.035) rot=(-0.309017,-0.951057,0;3.14159rad)
  LinkedObject = -> <external recicladora_cuchillas.FCStd>#Body008
  Placement = pos=(-4.94e-14,-1.18e-14,144.035) rot=(-0.309017,-0.951057,0;3.14159rad)
  SolverId = Asm4EE
  expr: Placement = Cuchilla006002.Placement * recicladora_cuchillas#LCS_cuchilla_salida005.Placement * AttachmentOffset * recicladora_cuchillas#LCS_separador.Placement ^ -1
FEATURE [App::Link] Cuchilla006003
  AssemblyType = Part::Link
  AttachedBy = #LCS_cuchilla_entrada
  AttachedTo = SeparadorCuchilla018#LCS_separador_salida
  AttachmentOffset = pos=(0,0,0) rot=(0,0,1;-1.0472rad)
  LinkPlacement = pos=(-4.91e-14,-8.2e-15,144.035) rot=(0,0,-1;4.81711rad)
  LinkedObject = -> <external recicladora_cuchillas.FCStd>#Body001
  Placement = pos=(-4.91e-14,-8.2e-15,144.035) rot=(0,0,-1;4.81711rad)
  SolverId = Asm4EE
  expr: Placement = SeparadorCuchilla018.Placement * recicladora_cuchillas#LCS_separador_salida.Placement * AttachmentOffset * recicladora_cuchillas#LCS_cuchilla_entrada.Placement ^ -1
FEATURE [App::Link] Cuchilla006004
  AssemblyType = Part::Link
  AttachedBy = #LCS_cuchilla_entrada
  AttachedTo = SeparadorCuchilla006#LCS_separador_salida
  AttachmentOffset = pos=(0,0,0) rot=(0,0,1;-1.0472rad)
  LinkPlacement = pos=(-6.79e-14,1.6e-15,162.035) rot=(0,0,1;0.418879rad)
  LinkedObject = -> <external recicladora_cuchillas.FCStd>#Body001
  Placement = pos=(-6.79e-14,1.6e-15,162.035) rot=(0,0,1;0.418879rad)
  SolverId = Asm4EE
  expr: Placement = SeparadorCuchilla024.Placement * recicladora_cuchillas#LCS_separador_salida.Placement * AttachmentOffset * recicladora_cuchillas#LCS_cuchilla_entrada.Placement ^ -1
FEATURE [App::Link] Cuchilla006005
  AssemblyType = Part::Link
  AttachedBy = #LCS_cuchilla_entrada
  AttachedTo = SeparadorCuchilla012#LCS_separador_salida
  AttachmentOffset = pos=(0,0,0) rot=(0,0,1;-1.0472rad)
  LinkPlacement = pos=(-7.87e-14,1.23e-14,180.035) rot=(0,0,1;5.65487rad)
  LinkedObject = -> <external recicladora_cuchillas.FCStd>#Body001
  Placement = pos=(-7.87e-14,1.23e-14,180.035) rot=(0,0,1;5.65487rad)
  SolverId = Asm4EE
  expr: Placement = SeparadorCuchilla030.Placement * recicladora_cuchillas#LCS_separador_salida.Placement * AttachmentOffset * recicladora_cuchillas#LCS_cuchilla_entrada.Placement ^ -1
FEATURE [App::Link] Cuchilla006006
  AssemblyType = Part::Link
  AttachedBy = #LCS_cuchilla_entrada001
  AttachedTo = SeparadorCuchilla001#LCS_separador_salida
  LinkPlacement = pos=(-5.32e-14,-6.8e-15,147.035) rot=(0,0,-1;4.99164rad)
  LinkedObject = -> <external recicladora_cuchillas.FCStd>#Body009
  Placement = pos=(-5.32e-14,-6.8e-15,147.035) rot=(0,0,-1;4.99164rad)
  SolverId = Asm4EE
  expr: Placement = SeparadorCuchilla019.Placement * recicladora_cuchillas#LCS_separador_salida.Placement * AttachmentOffset * recicladora_cuchillas#LCS_cuchilla_entrada001.Placement ^ -1
FEATURE [App::Link] Cuchilla006007
  AssemblyType = Part::Link
  AttachedBy = #LCS_cuchilla_entrada001
  AttachedTo = SeparadorCuchilla007#LCS_separador_salida
  LinkPlacement = pos=(-7.04e-14,4.1e-15,165.035) rot=(0,0,1;0.244346rad)
  LinkedObject = -> <external recicladora_cuchillas.FCStd>#Body009
  Placement = pos=(-7.04e-14,4.1e-15,165.035) rot=(0,0,1;0.244346rad)
  SolverId = Asm4EE
  expr: Placement = SeparadorCuchilla025.Placement * recicladora_cuchillas#LCS_separador_salida.Placement * AttachmentOffset * recicladora_cuchillas#LCS_cuchilla_entrada001.Placement ^ -1
FEATURE [App::Link] Cuchilla006008
  AssemblyType = Part::Link
  AttachedBy = #LCS_cuchilla_entrada001
  AttachedTo = SeparadorCuchilla013#LCS_separador_salida
  LinkPlacement = pos=(-7.94e-14,1.4e-14,183.035) rot=(0,0,1;5.48033rad)
  LinkedObject = -> <external recicladora_cuchillas.FCStd>#Body009
  Placement = pos=(-7.94e-14,1.4e-14,183.035) rot=(0,0,1;5.48033rad)
  SolverId = Asm4EE
  expr: Placement = SeparadorCuchilla031.Placement * recicladora_cuchillas#LCS_separador_salida.Placement * AttachmentOffset * recicladora_cuchillas#LCS_cuchilla_entrada001.Placement ^ -1
FEATURE [App::Link] Cuchilla006009
  AssemblyType = Part::Link
  AttachedBy = #LCS_cuchilla_entrada002
  AttachedTo = SeparadorCuchilla002#LCS_separador_salida
  LinkPlacement = pos=(-5.7e-14,-5.2e-15,150.035) rot=(0,0,-1;5.16617rad)
  LinkedObject = -> <external recicladora_cuchillas.FCStd>#Body010
  Placement = pos=(-5.7e-14,-5.2e-15,150.035) rot=(0,0,-1;5.16617rad)
  SolverId = Asm4EE
  expr: Placement = SeparadorCuchilla020.Placement * recicladora_cuchillas#LCS_separador_salida.Placement * AttachmentOffset * recicladora_cuchillas#LCS_cuchilla_entrada002.Placement ^ -1
FEATURE [App::Link] Cuchilla006010
  AssemblyType = Part::Link
  AttachedBy = #LCS_cuchilla_entrada002
  AttachedTo = SeparadorCuchilla008#LCS_separador_salida
  LinkPlacement = pos=(-7.25e-14,6.5e-15,168.035) rot=(0,0,1;0.069813rad)
  LinkedObject = -> <external recicladora_cuchillas.FCStd>#Body010
  Placement = pos=(-7.25e-14,6.5e-15,168.035) rot=(0,0,1;0.069813rad)
  SolverId = Asm4EE
  expr: Placement = SeparadorCuchilla026.Placement * recicladora_cuchillas#LCS_separador_salida.Placement * AttachmentOffset * recicladora_cuchillas#LCS_cuchilla_entrada002.Placement ^ -1
FEATURE [App::Link] Cuchilla006011
  AssemblyType = Part::Link
  AttachedBy = #LCS_cuchilla_entrada002
  AttachedTo = SeparadorCuchilla014#LCS_separador_salida
  LinkPlacement = pos=(-8.01e-14,1.53e-14,186.035) rot=(0,0,1;5.3058rad)
  LinkedObject = -> <external recicladora_cuchillas.FCStd>#Body010
  Placement = pos=(-8.01e-14,1.53e-14,186.035) rot=(0,0,1;5.3058rad)
  SolverId = Asm4EE
  expr: Placement = SeparadorCuchilla032.Placement * recicladora_cuchillas#LCS_separador_salida.Placement * AttachmentOffset * recicladora_cuchillas#LCS_cuchilla_entrada002.Placement ^ -1
FEATURE [App::Link] Cuchilla006012
  AssemblyType = Part::Link
  AttachedBy = #LCS_cuchilla_entrada003
  AttachedTo = SeparadorCuchilla003#LCS_separador_salida
  LinkPlacement = pos=(-6.09e-14,-3e-15,153.035) rot=(0,0,-1;5.34071rad)
  LinkedObject = -> <external recicladora_cuchillas.FCStd>#Body011
  Placement = pos=(-6.09e-14,-3e-15,153.035) rot=(0,0,-1;5.34071rad)
  SolverId = Asm4EE
  expr: Placement = SeparadorCuchilla021.Placement * recicladora_cuchillas#LCS_separador_salida.Placement * AttachmentOffset * recicladora_cuchillas#LCS_cuchilla_entrada003.Placement ^ -1
FEATURE [App::Link] Cuchilla006013
  AssemblyType = Part::Link
  AttachedBy = #LCS_cuchilla_entrada003
  AttachedTo = SeparadorCuchilla009#LCS_separador_salida
  LinkPlacement = pos=(-7.42e-14,9.2e-15,171.035) rot=(0,0,-1;0.10472rad)
  LinkedObject = -> <external recicladora_cuchillas.FCStd>#Body011
  Placement = pos=(-7.42e-14,9.2e-15,171.035) rot=(0,0,-1;0.10472rad)
  SolverId = Asm4EE
  expr: Placement = SeparadorCuchilla027.Placement * recicladora_cuchillas#LCS_separador_salida.Placement * AttachmentOffset * recicladora_cuchillas#LCS_cuchilla_entrada003.Placement ^ -1
FEATURE [App::Link] Cuchilla006014
  AssemblyType = Part::Link
  AttachedBy = #LCS_cuchilla_entrada003
  AttachedTo = SeparadorCuchilla015#LCS_separador_salida
  LinkPlacement = pos=(-8.02e-14,1.63e-14,189.035) rot=(0,0,1;5.13127rad)
  LinkedObject = -> <external recicladora_cuchillas.FCStd>#Body011
  Placement = pos=(-8.02e-14,1.63e-14,189.035) rot=(0,0,1;5.13127rad)
  SolverId = Asm4EE
  expr: Placement = SeparadorCuchilla033.Placement * recicladora_cuchillas#LCS_separador_salida.Placement * AttachmentOffset * recicladora_cuchillas#LCS_cuchilla_entrada003.Placement ^ -1
FEATURE [App::Link] Cuchilla006015
  AssemblyType = Part::Link
  AttachedBy = #LCS_cuchilla_entrada004
  AttachedTo = SeparadorCuchilla004#LCS_separador_salida
  LinkPlacement = pos=(-6.5e-14,-4.8e-15,156.035) rot=(0,0,-1;5.51524rad)
  LinkedObject = -> <external recicladora_cuchillas.FCStd>#Body012
  Placement = pos=(-6.5e-14,-4.8e-15,156.035) rot=(0,0,-1;5.51524rad)
  SolverId = Asm4EE
  expr: Placement = SeparadorCuchilla022.Placement * recicladora_cuchillas#LCS_separador_salida.Placement * AttachmentOffset * recicladora_cuchillas#LCS_cuchilla_entrada004.Placement ^ -1
FEATURE [App::Link] Cuchilla006016
  AssemblyType = Part::Link
  AttachedBy = #LCS_cuchilla_entrada004
  AttachedTo = SeparadorCuchilla010#LCS_separador_salida
  LinkPlacement = pos=(-7.95e-14,1.01e-14,174.035) rot=(0,0,-1;0.279253rad)
  LinkedObject = -> <external recicladora_cuchillas.FCStd>#Body012
  Placement = pos=(-7.95e-14,1.01e-14,174.035) rot=(0,0,-1;0.279253rad)
  SolverId = Asm4EE
  expr: Placement = SeparadorCuchilla028.Placement * recicladora_cuchillas#LCS_separador_salida.Placement * AttachmentOffset * recicladora_cuchillas#LCS_cuchilla_entrada004.Placement ^ -1
FEATURE [App::Link] Cuchilla006017
  AssemblyType = Part::Link
  AttachedBy = #LCS_cuchilla_entrada004
  AttachedTo = SeparadorCuchilla016#LCS_separador_salida
  LinkPlacement = pos=(-8.37e-14,1.96e-14,192.035) rot=(0,0,1;4.95674rad)
  LinkedObject = -> <external recicladora_cuchillas.FCStd>#Body012
  Placement = pos=(-8.37e-14,1.96e-14,192.035) rot=(0,0,1;4.95674rad)
  SolverId = Asm4EE
  expr: Placement = SeparadorCuchilla034.Placement * recicladora_cuchillas#LCS_separador_salida.Placement * AttachmentOffset * recicladora_cuchillas#LCS_cuchilla_entrada004.Placement ^ -1
FEATURE [App::Link] Cuchilla006018
  AssemblyType = Part::Link
  AttachedBy = #LCS_cuchilla_entrada005
  AttachedTo = SeparadorCuchilla005#LCS_separador_salida
  LinkPlacement = pos=(-6.78e-14,0,159.035) rot=(0,0,-1;5.68977rad)
  LinkedObject = -> <external recicladora_cuchillas.FCStd>#Body013
  Placement = pos=(-6.78e-14,0,159.035) rot=(0,0,-1;5.68977rad)
  SolverId = Asm4EE
  expr: Placement = SeparadorCuchilla023.Placement * recicladora_cuchillas#LCS_separador_salida.Placement * AttachmentOffset * recicladora_cuchillas#LCS_cuchilla_entrada005.Placement ^ -1
FEATURE [App::Link] Cuchilla006019
  AssemblyType = Part::Link
  AttachedBy = #LCS_cuchilla_entrada005
  AttachedTo = SeparadorCuchilla011#LCS_separador_salida
  LinkPlacement = pos=(-7.83e-14,1.31e-14,177.035) rot=(0,0,-1;0.453786rad)
  LinkedObject = -> <external recicladora_cuchillas.FCStd>#Body013
  Placement = pos=(-7.83e-14,1.31e-14,177.035) rot=(0,0,-1;0.453786rad)
  SolverId = Asm4EE
  expr: Placement = SeparadorCuchilla029.Placement * recicladora_cuchillas#LCS_separador_salida.Placement * AttachmentOffset * recicladora_cuchillas#LCS_cuchilla_entrada005.Placement ^ -1
FEATURE [App::Link] Cuchilla006020
  AssemblyType = Part::Link
  AttachedBy = #LCS_cuchilla_entrada005
  AttachedTo = SeparadorCuchilla017#LCS_separador_salida
  LinkPlacement = pos=(-8.22e-14,1.84e-14,195.035) rot=(0,0,1;4.7822rad)
  LinkedObject = -> <external recicladora_cuchillas.FCStd>#Body013
  Placement = pos=(-8.22e-14,1.84e-14,195.035) rot=(0,0,1;4.7822rad)
  SolverId = Asm4EE
  expr: Placement = SeparadorCuchilla035.Placement * recicladora_cuchillas#LCS_separador_salida.Placement * AttachmentOffset * recicladora_cuchillas#LCS_cuchilla_entrada005.Placement ^ -1
FEATURE [App::Link] SeparadorCuchilla019
  AssemblyType = Part::Link
  AttachedBy = #LCS_separador
  AttachedTo = Cuchilla001#LCS_cuchilla_salida
  LinkPlacement = pos=(-5.38e-14,-1.04e-14,147.035) rot=(0.743145,0.669131,0;3.14159rad)
  LinkedObject = -> <external recicladora_cuchillas.FCStd>#Body008
  Placement = pos=(-5.38e-14,-1.04e-14,147.035) rot=(0.743145,0.669131,0;3.14159rad)
  SolverId = Asm4EE
  expr: Placement = Cuchilla006003.Placement * recicladora_cuchillas#LCS_cuchilla_salida.Placement * AttachmentOffset * recicladora_cuchillas#LCS_separador.Placement ^ -1
FEATURE [App::Link] SeparadorCuchilla020
  AssemblyType = Part::Link
  AttachedBy = #LCS_separador
  AttachedTo = Cuchilla002#LCS_cuchilla_salida001
  LinkPlacement = pos=(-5.78e-14,-8.7e-15,150.035) rot=(0.743145,0.669131,0;3.14159rad)
  LinkedObject = -> <external recicladora_cuchillas.FCStd>#Body008
  Placement = pos=(-5.78e-14,-8.7e-15,150.035) rot=(0.743145,0.669131,0;3.14159rad)
  SolverId = Asm4EE
  expr: Placement = Cuchilla006006.Placement * recicladora_cuchillas#LCS_cuchilla_salida001.Placement * AttachmentOffset * recicladora_cuchillas#LCS_separador.Placement ^ -1
FEATURE [App::Link] SeparadorCuchilla021
  AssemblyType = Part::Link
  AttachedBy = #LCS_separador
  AttachedTo = Cuchilla003#LCS_cuchilla_salida002
  LinkPlacement = pos=(-6.16e-14,-6.9e-15,153.035) rot=(0.743145,0.669131,0;3.14159rad)
  LinkedObject = -> <external recicladora_cuchillas.FCStd>#Body008
  Placement = pos=(-6.16e-14,-6.9e-15,153.035) rot=(0.743145,0.669131,0;3.14159rad)
  SolverId = Asm4EE
  expr: Placement = Cuchilla006009.Placement * recicladora_cuchillas#LCS_cuchilla_salida002.Placement * AttachmentOffset * recicladora_cuchillas#LCS_separador.Placement ^ -1
FEATURE [App::Link] SeparadorCuchilla022
  AssemblyType = Part::Link
  AttachedBy = #LCS_separador
  AttachedTo = Cuchilla004#LCS_cuchilla_salida003
  LinkPlacement = pos=(-6.5e-14,-4.8e-15,156.035) rot=(0.743145,0.669131,0;3.14159rad)
  LinkedObject = -> <external recicladora_cuchillas.FCStd>#Body008
  Placement = pos=(-6.5e-14,-4.8e-15,156.035) rot=(0.743145,0.669131,0;3.14159rad)
  SolverId = Asm4EE
  expr: Placement = Cuchilla006012.Placement * recicladora_cuchillas#LCS_cuchilla_salida003.Placement * AttachmentOffset * recicladora_cuchillas#LCS_separador.Placement ^ -1
FEATURE [App::Link] SeparadorCuchilla023
  AssemblyType = Part::Link
  AttachedBy = #LCS_separador
  AttachedTo = Cuchilla005#LCS_cuchilla_salida004
  LinkPlacement = pos=(-6.82e-14,-2.4e-15,159.035) rot=(0.743145,0.669131,0;3.14159rad)
  LinkedObject = -> <external recicladora_cuchillas.FCStd>#Body008
  Placement = pos=(-6.82e-14,-2.4e-15,159.035) rot=(0.743145,0.669131,0;3.14159rad)
  SolverId = Asm4EE
  expr: Placement = Cuchilla006015.Placement * recicladora_cuchillas#LCS_cuchilla_salida004.Placement * AttachmentOffset * recicladora_cuchillas#LCS_separador.Placement ^ -1
FEATURE [App::Link] SeparadorCuchilla024
  AssemblyType = Part::Link
  AttachedBy = #LCS_separador
  AttachedTo = Cuchilla006#LCS_cuchilla_salida005
  LinkPlacement = pos=(-7.11e-14,1e-16,162.035) rot=(0.743145,0.669131,0;3.14159rad)
  LinkedObject = -> <external recicladora_cuchillas.FCStd>#Body008
  Placement = pos=(-7.11e-14,1e-16,162.035) rot=(0.743145,0.669131,0;3.14159rad)
  SolverId = Asm4EE
  expr: Placement = Cuchilla006018.Placement * recicladora_cuchillas#LCS_cuchilla_salida005.Placement * AttachmentOffset * recicladora_cuchillas#LCS_separador.Placement ^ -1
FEATURE [App::Link] SeparadorCuchilla025
  AssemblyType = Part::Link
  AttachedBy = #LCS_separador
  AttachedTo = Cuchilla001001#LCS_cuchilla_salida
  LinkPlacement = pos=(-7.37e-14,2.8e-15,165.035) rot=(-0.978148,-0.207912,0;3.14159rad)
  LinkedObject = -> <external recicladora_cuchillas.FCStd>#Body008
  Placement = pos=(-7.37e-14,2.8e-15,165.035) rot=(-0.978148,-0.207912,0;3.14159rad)
  SolverId = Asm4EE
  expr: Placement = Cuchilla006004.Placement * recicladora_cuchillas#LCS_cuchilla_salida.Placement * AttachmentOffset * recicladora_cuchillas#LCS_separador.Placement ^ -1
FEATURE [App::Link] SeparadorCuchilla026
  AssemblyType = Part::Link
  AttachedBy = #LCS_separador
  AttachedTo = Cuchilla002001#LCS_cuchilla_salida001
  LinkPlacement = pos=(-7.6e-14,5.4e-15,168.035) rot=(-0.978148,-0.207912,0;3.14159rad)
  LinkedObject = -> <external recicladora_cuchillas.FCStd>#Body008
  Placement = pos=(-7.6e-14,5.4e-15,168.035) rot=(-0.978148,-0.207912,0;3.14159rad)
  SolverId = Asm4EE
  expr: Placement = Cuchilla006007.Placement * recicladora_cuchillas#LCS_cuchilla_salida001.Placement * AttachmentOffset * recicladora_cuchillas#LCS_separador.Placement ^ -1
FEATURE [App::Link] SeparadorCuchilla027
  AssemblyType = Part::Link
  AttachedBy = #LCS_separador
  AttachedTo = Cuchilla003001#LCS_cuchilla_salida002
  LinkPlacement = pos=(-7.79e-14,7.8e-15,171.035) rot=(-0.978148,-0.207912,0;3.14159rad)
  LinkedObject = -> <external recicladora_cuchillas.FCStd>#Body008
  Placement = pos=(-7.79e-14,7.8e-15,171.035) rot=(-0.978148,-0.207912,0;3.14159rad)
  SolverId = Asm4EE
  expr: Placement = Cuchilla006010.Placement * recicladora_cuchillas#LCS_cuchilla_salida002.Placement * AttachmentOffset * recicladora_cuchillas#LCS_separador.Placement ^ -1
FEATURE [App::Link] SeparadorCuchilla028
  AssemblyType = Part::Link
  AttachedBy = #LCS_separador
  AttachedTo = Cuchilla004001#LCS_cuchilla_salida003
  LinkPlacement = pos=(-7.95e-14,1.01e-14,174.035) rot=(-0.978148,-0.207912,0;3.14159rad)
  LinkedObject = -> <external recicladora_cuchillas.FCStd>#Body008
  Placement = pos=(-7.95e-14,1.01e-14,174.035) rot=(-0.978148,-0.207912,0;3.14159rad)
  SolverId = Asm4EE
  expr: Placement = Cuchilla006013.Placement * recicladora_cuchillas#LCS_cuchilla_salida003.Placement * AttachmentOffset * recicladora_cuchillas#LCS_separador.Placement ^ -1
FEATURE [App::Link] SeparadorCuchilla029
  AssemblyType = Part::Link
  AttachedBy = #LCS_separador
  AttachedTo = Cuchilla005001#LCS_cuchilla_salida004
  LinkPlacement = pos=(-8.07e-14,1.23e-14,177.035) rot=(-0.978148,-0.207912,0;3.14159rad)
  LinkedObject = -> <external recicladora_cuchillas.FCStd>#Body008
  Placement = pos=(-8.07e-14,1.23e-14,177.035) rot=(-0.978148,-0.207912,0;3.14159rad)
  SolverId = Asm4EE
  expr: Placement = Cuchilla006016.Placement * recicladora_cuchillas#LCS_cuchilla_salida004.Placement * AttachmentOffset * recicladora_cuchillas#LCS_separador.Placement ^ -1
FEATURE [App::Link] SeparadorCuchilla030
  AssemblyType = Part::Link
  AttachedBy = #LCS_separador
  AttachedTo = Cuchilla006001#LCS_cuchilla_salida005
  LinkPlacement = pos=(-8.16e-14,1.44e-14,180.035) rot=(-0.978148,-0.207912,0;3.14159rad)
  LinkedObject = -> <external recicladora_cuchillas.FCStd>#Body008
  Placement = pos=(-8.16e-14,1.44e-14,180.035) rot=(-0.978148,-0.207912,0;3.14159rad)
  SolverId = Asm4EE
  expr: Placement = Cuchilla006019.Placement * recicladora_cuchillas#LCS_cuchilla_salida005.Placement * AttachmentOffset * recicladora_cuchillas#LCS_separador.Placement ^ -1
FEATURE [App::Link] SeparadorCuchilla031
  AssemblyType = Part::Link
  AttachedBy = #LCS_separador
  AttachedTo = Cuchilla001002#LCS_cuchilla_salida
  LinkPlacement = pos=(-8.22e-14,1.62e-14,183.035) rot=(0.951057,-0.309017,0;3.14159rad)
  LinkedObject = -> <external recicladora_cuchillas.FCStd>#Body008
  Placement = pos=(-8.22e-14,1.62e-14,183.035) rot=(0.951057,-0.309017,0;3.14159rad)
  SolverId = Asm4EE
  expr: Placement = Cuchilla006005.Placement * recicladora_cuchillas#LCS_cuchilla_salida.Placement * AttachmentOffset * recicladora_cuchillas#LCS_separador.Placement ^ -1
FEATURE [App::Link] SeparadorCuchilla032
  AssemblyType = Part::Link
  AttachedBy = #LCS_separador
  AttachedTo = Cuchilla002002#LCS_cuchilla_salida001
  LinkPlacement = pos=(-8.28e-14,1.77e-14,186.035) rot=(0.951057,-0.309017,0;3.14159rad)
  LinkedObject = -> <external recicladora_cuchillas.FCStd>#Body008
  Placement = pos=(-8.28e-14,1.77e-14,186.035) rot=(0.951057,-0.309017,0;3.14159rad)
  SolverId = Asm4EE
  expr: Placement = Cuchilla006008.Placement * recicladora_cuchillas#LCS_cuchilla_salida001.Placement * AttachmentOffset * recicladora_cuchillas#LCS_separador.Placement ^ -1
FEATURE [App::Link] SeparadorCuchilla033
  AssemblyType = Part::Link
  AttachedBy = #LCS_separador
  AttachedTo = Cuchilla003002#LCS_cuchilla_salida002
  LinkPlacement = pos=(-8.33e-14,1.88e-14,189.035) rot=(0.951057,-0.309017,0;3.14159rad)
  LinkedObject = -> <external recicladora_cuchillas.FCStd>#Body008
  Placement = pos=(-8.33e-14,1.88e-14,189.035) rot=(0.951057,-0.309017,0;3.14159rad)
  SolverId = Asm4EE
  expr: Placement = Cuchilla006011.Placement * recicladora_cuchillas#LCS_cuchilla_salida002.Placement * AttachmentOffset * recicladora_cuchillas#LCS_separador.Placement ^ -1
FEATURE [App::Link] SeparadorCuchilla034
  AssemblyType = Part::Link
  AttachedBy = #LCS_separador
  AttachedTo = Cuchilla004002#LCS_cuchilla_salida003
  LinkPlacement = pos=(-8.37e-14,1.96e-14,192.035) rot=(0.951057,-0.309017,0;3.14159rad)
  LinkedObject = -> <external recicladora_cuchillas.FCStd>#Body008
  Placement = pos=(-8.37e-14,1.96e-14,192.035) rot=(0.951057,-0.309017,0;3.14159rad)
  SolverId = Asm4EE
  expr: Placement = Cuchilla006014.Placement * recicladora_cuchillas#LCS_cuchilla_salida003.Placement * AttachmentOffset * recicladora_cuchillas#LCS_separador.Placement ^ -1
FEATURE [App::Link] SeparadorCuchilla035
  AssemblyType = Part::Link
  AttachedBy = #LCS_separador
  AttachedTo = Cuchilla005002#LCS_cuchilla_salida004
  LinkPlacement = pos=(-8.41e-14,2e-14,195.035) rot=(0.951057,-0.309017,0;3.14159rad)
  LinkedObject = -> <external recicladora_cuchillas.FCStd>#Body008
  Placement = pos=(-8.41e-14,2e-14,195.035) rot=(0.951057,-0.309017,0;3.14159rad)
  SolverId = Asm4EE
  expr: Placement = Cuchilla006017.Placement * recicladora_cuchillas#LCS_cuchilla_salida004.Placement * AttachmentOffset * recicladora_cuchillas#LCS_separador.Placement ^ -1
FEATURE [App::Link] CuchillaFijaSeparador004
  AssemblyType = Part::Link
  AttachedBy = #LCS_eje_central
  AttachedTo = CuchillaFija003#LCS_cuchilla_fija_salida
  LinkPlacement = pos=(65,-65,100.535) rot=(0,0,1;0rad)
  LinkedObject = -> <external recicladora_piezas_fijas.FCStd>#Body
  Placement = pos=(65,-65,100.535) rot=(0,0,1;0rad)
  SolverId = Asm4EE
  expr: Placement = CuchillaFija003.Placement * recicladora_piezas_fijas#LCS_cuchilla_fija_salida.Placement * AttachmentOffset * recicladora_piezas_fijas#LCS_eje_central.Placement ^ -1
FEATURE [App::Link] CuchillaFija004
  AssemblyType = Part::Link
  AttachedBy = #LCS_eje_central001
  AttachedTo = CuchillaFijaSeparador004#LCS_cuchilla_fija_separador_salida
  LinkPlacement = pos=(65,-65,102.035) rot=(0,0,1;0rad)
  LinkedObject = -> <external recicladora_piezas_fijas.FCStd>#CuchillaFija
  Placement = pos=(65,-65,102.035) rot=(0,0,1;0rad)
  SolverId = Asm4EE
  expr: Placement = CuchillaFijaSeparador004.Placement * recicladora_piezas_fijas#LCS_cuchilla_fija_separador_salida.Placement * AttachmentOffset * recicladora_piezas_fijas#LCS_eje_central001.Placement ^ -1
FEATURE [App::Link] CuchillaFijaSeparador005
  AssemblyType = Part::Link
  AttachedBy = #LCS_eje_central
  AttachedTo = CuchillaFija004#LCS_cuchilla_fija_salida
  LinkPlacement = pos=(65,-65,103.535) rot=(0,0,1;0rad)
  LinkedObject = -> <external recicladora_piezas_fijas.FCStd>#Body
  Placement = pos=(65,-65,103.535) rot=(0,0,1;0rad)
  SolverId = Asm4EE
  expr: Placement = CuchillaFija004.Placement * recicladora_piezas_fijas#LCS_cuchilla_fija_salida.Placement * AttachmentOffset * recicladora_piezas_fijas#LCS_eje_central.Placement ^ -1
FEATURE [App::Link] CuchillaFija005
  AssemblyType = Part::Link
  AttachedBy = #LCS_eje_central001
  AttachedTo = CuchillaFijaSeparador005#LCS_cuchilla_fija_separador_salida
  LinkPlacement = pos=(65,-65,105.035) rot=(0,0,1;0rad)
  LinkedObject = -> <external recicladora_piezas_fijas.FCStd>#CuchillaFija
  Placement = pos=(65,-65,105.035) rot=(0,0,1;0rad)
  SolverId = Asm4EE
  expr: Placement = CuchillaFijaSeparador005.Placement * recicladora_piezas_fijas#LCS_cuchilla_fija_separador_salida.Placement * AttachmentOffset * recicladora_piezas_fijas#LCS_eje_central001.Placement ^ -1
FEATURE [App::Link] CuchillaFijaSeparador006
  AssemblyType = Part::Link
  AttachedBy = #LCS_eje_central
  AttachedTo = CuchillaFija005#LCS_cuchilla_fija_salida
  LinkPlacement = pos=(65,-65,106.535) rot=(0,0,1;0rad)
  LinkedObject = -> <external recicladora_piezas_fijas.FCStd>#Body
  Placement = pos=(65,-65,106.535) rot=(0,0,1;0rad)
  SolverId = Asm4EE
  expr: Placement = CuchillaFija005.Placement * recicladora_piezas_fijas#LCS_cuchilla_fija_salida.Placement * AttachmentOffset * recicladora_piezas_fijas#LCS_eje_central.Placement ^ -1
FEATURE [App::Link] CuchillaFija006
  AssemblyType = Part::Link
  AttachedBy = #LCS_eje_central001
  AttachedTo = CuchillaFijaSeparador006#LCS_cuchilla_fija_separador_salida
  LinkPlacement = pos=(65,-65,108.035) rot=(0,0,1;0rad)
  LinkedObject = -> <external recicladora_piezas_fijas.FCStd>#CuchillaFija
  Placement = pos=(65,-65,108.035) rot=(0,0,1;0rad)
  SolverId = Asm4EE
  expr: Placement = CuchillaFijaSeparador006.Placement * recicladora_piezas_fijas#LCS_cuchilla_fija_separador_salida.Placement * AttachmentOffset * recicladora_piezas_fijas#LCS_eje_central001.Placement ^ -1
FEATURE [App::Link] CuchillaFijaSeparador007
  AssemblyType = Part::Link
  AttachedBy = #LCS_eje_central
  AttachedTo = CuchillaFija006#LCS_cuchilla_fija_salida
  LinkPlacement = pos=(65,-65,109.535) rot=(0,0,1;0rad)
  LinkedObject = -> <external recicladora_piezas_fijas.FCStd>#Body
  Placement = pos=(65,-65,109.535) rot=(0,0,1;0rad)
  SolverId = Asm4EE
  expr: Placement = CuchillaFija006.Placement * recicladora_piezas_fijas#LCS_cuchilla_fija_salida.Placement * AttachmentOffset * recicladora_piezas_fijas#LCS_eje_central.Placement ^ -1
FEATURE [App::Link] CuchillaFija007
  AssemblyType = Part::Link
  AttachedBy = #LCS_eje_central001
  AttachedTo = CuchillaFijaSeparador007#LCS_cuchilla_fija_separador_salida
  LinkPlacement = pos=(65,-65,111.035) rot=(0,0,1;0rad)
  LinkedObject = -> <external recicladora_piezas_fijas.FCStd>#CuchillaFija
  Placement = pos=(65,-65,111.035) rot=(0,0,1;0rad)
  SolverId = Asm4EE
  expr: Placement = CuchillaFijaSeparador007.Placement * recicladora_piezas_fijas#LCS_cuchilla_fija_separador_salida.Placement * AttachmentOffset * recicladora_piezas_fijas#LCS_eje_central001.Placement ^ -1
FEATURE [App::Link] CuchillaFijaSeparador008
  AssemblyType = Part::Link
  AttachedBy = #LCS_eje_central
  AttachedTo = CuchillaFija007#LCS_cuchilla_fija_salida
  LinkPlacement = pos=(65,-65,112.535) rot=(0,0,1;0rad)
  LinkedObject = -> <external recicladora_piezas_fijas.FCStd>#Body
  Placement = pos=(65,-65,112.535) rot=(0,0,1;0rad)
  SolverId = Asm4EE
  expr: Placement = CuchillaFija007.Placement * recicladora_piezas_fijas#LCS_cuchilla_fija_salida.Placement * AttachmentOffset * recicladora_piezas_fijas#LCS_eje_central.Placement ^ -1
FEATURE [App::Link] CuchillaFija008
  AssemblyType = Part::Link
  AttachedBy = #LCS_eje_central001
  AttachedTo = CuchillaFijaSeparador008#LCS_cuchilla_fija_separador_salida
  LinkPlacement = pos=(65,-65,114.035) rot=(0,0,1;0rad)
  LinkedObject = -> <external recicladora_piezas_fijas.FCStd>#CuchillaFija
  Placement = pos=(65,-65,114.035) rot=(0,0,1;0rad)
  SolverId = Asm4EE
  expr: Placement = CuchillaFijaSeparador008.Placement * recicladora_piezas_fijas#LCS_cuchilla_fija_separador_salida.Placement * AttachmentOffset * recicladora_piezas_fijas#LCS_eje_central001.Placement ^ -1
FEATURE [App::Link] CuchillaFijaSeparador009
  AssemblyType = Part::Link
  AttachedBy = #LCS_eje_central
  AttachedTo = CuchillaFija008#LCS_cuchilla_fija_salida
  LinkPlacement = pos=(65,-65,115.535) rot=(0,0,1;0rad)
  LinkedObject = -> <external recicladora_piezas_fijas.FCStd>#Body
  Placement = pos=(65,-65,115.535) rot=(0,0,1;0rad)
  SolverId = Asm4EE
  expr: Placement = CuchillaFija008.Placement * recicladora_piezas_fijas#LCS_cuchilla_fija_salida.Placement * AttachmentOffset * recicladora_piezas_fijas#LCS_eje_central.Placement ^ -1
FEATURE [App::Link] CuchillaFija009
  AssemblyType = Part::Link
  AttachedBy = #LCS_eje_central001
  AttachedTo = CuchillaFijaSeparador009#LCS_cuchilla_fija_separador_salida
  LinkPlacement = pos=(65,-65,117.035) rot=(0,0,1;0rad)
  LinkedObject = -> <external recicladora_piezas_fijas.FCStd>#CuchillaFija
  Placement = pos=(65,-65,117.035) rot=(0,0,1;0rad)
  SolverId = Asm4EE
  expr: Placement = CuchillaFijaSeparador009.Placement * recicladora_piezas_fijas#LCS_cuchilla_fija_separador_salida.Placement * AttachmentOffset * recicladora_piezas_fijas#LCS_eje_central001.Placement ^ -1
FEATURE [App::Link] CuchillaFijaSeparador010
  AssemblyType = Part::Link
  AttachedBy = #LCS_eje_central
  AttachedTo = CuchillaFija009#LCS_cuchilla_fija_salida
  LinkPlacement = pos=(65,-65,118.535) rot=(0,0,1;0rad)
  LinkedObject = -> <external recicladora_piezas_fijas.FCStd>#Body
  Placement = pos=(65,-65,118.535) rot=(0,0,1;0rad)
  SolverId = Asm4EE
  expr: Placement = CuchillaFija009.Placement * recicladora_piezas_fijas#LCS_cuchilla_fija_salida.Placement * AttachmentOffset * recicladora_piezas_fijas#LCS_eje_central.Placement ^ -1
FEATURE [App::Link] CuchillaFija010
  AssemblyType = Part::Link
  AttachedBy = #LCS_eje_central001
  AttachedTo = CuchillaFijaSeparador010#LCS_cuchilla_fija_separador_salida
  LinkPlacement = pos=(65,-65,120.035) rot=(0,0,1;0rad)
  LinkedObject = -> <external recicladora_piezas_fijas.FCStd>#CuchillaFija
  Placement = pos=(65,-65,120.035) rot=(0,0,1;0rad)
  SolverId = Asm4EE
  expr: Placement = CuchillaFijaSeparador010.Placement * recicladora_piezas_fijas#LCS_cuchilla_fija_separador_salida.Placement * AttachmentOffset * recicladora_piezas_fijas#LCS_eje_central001.Placement ^ -1
FEATURE [App::Link] CuchillaFijaSeparador011
  AssemblyType = Part::Link
  AttachedBy = #LCS_eje_central
  AttachedTo = CuchillaFija010#LCS_cuchilla_fija_salida
  LinkPlacement = pos=(65,-65,121.535) rot=(0,0,1;0rad)
  LinkedObject = -> <external recicladora_piezas_fijas.FCStd>#Body
  Placement = pos=(65,-65,121.535) rot=(0,0,1;0rad)
  SolverId = Asm4EE
  expr: Placement = CuchillaFija010.Placement * recicladora_piezas_fijas#LCS_cuchilla_fija_salida.Placement * AttachmentOffset * recicladora_piezas_fijas#LCS_eje_central.Placement ^ -1
FEATURE [App::Link] CuchillaFija011
  AssemblyType = Part::Link
  AttachedBy = #LCS_eje_central001
  AttachedTo = CuchillaFijaSeparador011#LCS_cuchilla_fija_separador_salida
  LinkPlacement = pos=(65,-65,123.035) rot=(0,0,1;0rad)
  LinkedObject = -> <external recicladora_piezas_fijas.FCStd>#CuchillaFija
  Placement = pos=(65,-65,123.035) rot=(0,0,1;0rad)
  SolverId = Asm4EE
  expr: Placement = CuchillaFijaSeparador011.Placement * recicladora_piezas_fijas#LCS_cuchilla_fija_separador_salida.Placement * AttachmentOffset * recicladora_piezas_fijas#LCS_eje_central001.Placement ^ -1
FEATURE [App::Link] CuchillaFija012
  AssemblyType = Part::Link
  AttachedBy = #LCS_eje_central001
  AttachedTo = CuchillaFijaSeparador#LCS_cuchilla_fija_separador_salida
  LinkPlacement = pos=(65,-65,126.035) rot=(0,0,1;0rad)
  LinkedObject = -> <external recicladora_piezas_fijas.FCStd>#CuchillaFija
  Placement = pos=(65,-65,126.035) rot=(0,0,1;0rad)
  SolverId = Asm4EE
  expr: Placement = CuchillaFijaSeparador012.Placement * recicladora_piezas_fijas#LCS_cuchilla_fija_separador_salida.Placement * AttachmentOffset * recicladora_piezas_fijas#LCS_eje_central001.Placement ^ -1
FEATURE [App::Link] CuchillaFija013
  AssemblyType = Part::Link
  AttachedBy = #LCS_eje_central001
  AttachedTo = CuchillaFijaSeparador001#LCS_cuchilla_fija_separador_salida
  LinkPlacement = pos=(65,-65,129.035) rot=(0,0,1;0rad)
  LinkedObject = -> <external recicladora_piezas_fijas.FCStd>#CuchillaFija
  Placement = pos=(65,-65,129.035) rot=(0,0,1;0rad)
  SolverId = Asm4EE
  expr: Placement = CuchillaFijaSeparador013.Placement * recicladora_piezas_fijas#LCS_cuchilla_fija_separador_salida.Placement * AttachmentOffset * recicladora_piezas_fijas#LCS_eje_central001.Placement ^ -1
FEATURE [App::Link] CuchillaFija014
  AssemblyType = Part::Link
  AttachedBy = #LCS_eje_central001
  AttachedTo = CuchillaFijaSeparador002#LCS_cuchilla_fija_separador_salida
  LinkPlacement = pos=(65,-65,132.035) rot=(0,0,1;0rad)
  LinkedObject = -> <external recicladora_piezas_fijas.FCStd>#CuchillaFija
  Placement = pos=(65,-65,132.035) rot=(0,0,1;0rad)
  SolverId = Asm4EE
  expr: Placement = CuchillaFijaSeparador014.Placement * recicladora_piezas_fijas#LCS_cuchilla_fija_separador_salida.Placement * AttachmentOffset * recicladora_piezas_fijas#LCS_eje_central001.Placement ^ -1
FEATURE [App::Link] CuchillaFija015
  AssemblyType = Part::Link
  AttachedBy = #LCS_eje_central001
  AttachedTo = CuchillaFijaSeparador003#LCS_cuchilla_fija_separador_salida
  LinkPlacement = pos=(65,-65,135.035) rot=(0,0,1;0rad)
  LinkedObject = -> <external recicladora_piezas_fijas.FCStd>#CuchillaFija
  Placement = pos=(65,-65,135.035) rot=(0,0,1;0rad)
  SolverId = Asm4EE
  expr: Placement = CuchillaFijaSeparador015.Placement * recicladora_piezas_fijas#LCS_cuchilla_fija_separador_salida.Placement * AttachmentOffset * recicladora_piezas_fijas#LCS_eje_central001.Placement ^ -1
FEATURE [App::Link] CuchillaFija016
  AssemblyType = Part::Link
  AttachedBy = #LCS_eje_central001
  AttachedTo = CuchillaFijaSeparador004#LCS_cuchilla_fija_separador_salida
  LinkPlacement = pos=(65,-65,138.035) rot=(0,0,1;0rad)
  LinkedObject = -> <external recicladora_piezas_fijas.FCStd>#CuchillaFija
  Placement = pos=(65,-65,138.035) rot=(0,0,1;0rad)
  SolverId = Asm4EE
  expr: Placement = CuchillaFijaSeparador016.Placement * recicladora_piezas_fijas#LCS_cuchilla_fija_separador_salida.Placement * AttachmentOffset * recicladora_piezas_fijas#LCS_eje_central001.Placement ^ -1
FEATURE [App::Link] CuchillaFija017
  AssemblyType = Part::Link
  AttachedBy = #LCS_eje_central001
  AttachedTo = CuchillaFijaSeparador005#LCS_cuchilla_fija_separador_salida
  LinkPlacement = pos=(65,-65,141.035) rot=(0,0,1;0rad)
  LinkedObject = -> <external recicladora_piezas_fijas.FCStd>#CuchillaFija
  Placement = pos=(65,-65,141.035) rot=(0,0,1;0rad)
  SolverId = Asm4EE
  expr: Placement = CuchillaFijaSeparador017.Placement * recicladora_piezas_fijas#LCS_cuchilla_fija_separador_salida.Placement * AttachmentOffset * recicladora_piezas_fijas#LCS_eje_central001.Placement ^ -1
FEATURE [App::Link] CuchillaFija018
  AssemblyType = Part::Link
  AttachedBy = #LCS_eje_central001
  AttachedTo = CuchillaFijaSeparador006#LCS_cuchilla_fija_separador_salida
  LinkPlacement = pos=(65,-65,144.035) rot=(0,0,1;0rad)
  LinkedObject = -> <external recicladora_piezas_fijas.FCStd>#CuchillaFija
  Placement = pos=(65,-65,144.035) rot=(0,0,1;0rad)
  SolverId = Asm4EE
  expr: Placement = CuchillaFijaSeparador018.Placement * recicladora_piezas_fijas#LCS_cuchilla_fija_separador_salida.Placement * AttachmentOffset * recicladora_piezas_fijas#LCS_eje_central001.Placement ^ -1
FEATURE [App::Link] CuchillaFija019
  AssemblyType = Part::Link
  AttachedBy = #LCS_eje_central001
  AttachedTo = CuchillaFijaSeparador007#LCS_cuchilla_fija_separador_salida
  LinkPlacement = pos=(65,-65,147.035) rot=(0,0,1;0rad)
  LinkedObject = -> <external recicladora_piezas_fijas.FCStd>#CuchillaFija
  Placement = pos=(65,-65,147.035) rot=(0,0,1;0rad)
  SolverId = Asm4EE
  expr: Placement = CuchillaFijaSeparador019.Placement * recicladora_piezas_fijas#LCS_cuchilla_fija_separador_salida.Placement * AttachmentOffset * recicladora_piezas_fijas#LCS_eje_central001.Placement ^ -1
FEATURE [App::Link] CuchillaFija020
  AssemblyType = Part::Link
  AttachedBy = #LCS_eje_central001
  AttachedTo = CuchillaFijaSeparador008#LCS_cuchilla_fija_separador_salida
  LinkPlacement = pos=(65,-65,150.035) rot=(0,0,1;0rad)
  LinkedObject = -> <external recicladora_piezas_fijas.FCStd>#CuchillaFija
  Placement = pos=(65,-65,150.035) rot=(0,0,1;0rad)
  SolverId = Asm4EE
  expr: Placement = CuchillaFijaSeparador020.Placement * recicladora_piezas_fijas#LCS_cuchilla_fija_separador_salida.Placement * AttachmentOffset * recicladora_piezas_fijas#LCS_eje_central001.Placement ^ -1
FEATURE [App::Link] CuchillaFija021
  AssemblyType = Part::Link
  AttachedBy = #LCS_eje_central001
  AttachedTo = CuchillaFijaSeparador009#LCS_cuchilla_fija_separador_salida
  LinkPlacement = pos=(65,-65,153.035) rot=(0,0,1;0rad)
  LinkedObject = -> <external recicladora_piezas_fijas.FCStd>#CuchillaFija
  Placement = pos=(65,-65,153.035) rot=(0,0,1;0rad)
  SolverId = Asm4EE
  expr: Placement = CuchillaFijaSeparador021.Placement * recicladora_piezas_fijas#LCS_cuchilla_fija_separador_salida.Placement * AttachmentOffset * recicladora_piezas_fijas#LCS_eje_central001.Placement ^ -1
FEATURE [App::Link] CuchillaFija022
  AssemblyType = Part::Link
  AttachedBy = #LCS_eje_central001
  AttachedTo = CuchillaFijaSeparador010#LCS_cuchilla_fija_separador_salida
  LinkPlacement = pos=(65,-65,156.035) rot=(0,0,1;0rad)
  LinkedObject = -> <external recicladora_piezas_fijas.FCStd>#CuchillaFija
  Placement = pos=(65,-65,156.035) rot=(0,0,1;0rad)
  SolverId = Asm4EE
  expr: Placement = CuchillaFijaSeparador022.Placement * recicladora_piezas_fijas#LCS_cuchilla_fija_separador_salida.Placement * AttachmentOffset * recicladora_piezas_fijas#LCS_eje_central001.Placement ^ -1
FEATURE [App::Link] CuchillaFija023
  AssemblyType = Part::Link
  AttachedBy = #LCS_eje_central001
  AttachedTo = CuchillaFijaSeparador011#LCS_cuchilla_fija_separador_salida
  LinkPlacement = pos=(65,-65,159.035) rot=(0,0,1;0rad)
  LinkedObject = -> <external recicladora_piezas_fijas.FCStd>#CuchillaFija
  Placement = pos=(65,-65,159.035) rot=(0,0,1;0rad)
  SolverId = Asm4EE
  expr: Placement = CuchillaFijaSeparador023.Placement * recicladora_piezas_fijas#LCS_cuchilla_fija_separador_salida.Placement * AttachmentOffset * recicladora_piezas_fijas#LCS_eje_central001.Placement ^ -1
FEATURE [App::Link] CuchillaFijaSeparador012
  AssemblyType = Part::Link
  AttachedBy = #LCS_eje_central
  AttachedTo = CuchillaFija011#LCS_cuchilla_fija_salida
  LinkPlacement = pos=(65,-65,124.535) rot=(0,0,1;0rad)
  LinkedObject = -> <external recicladora_piezas_fijas.FCStd>#Body
  Placement = pos=(65,-65,124.535) rot=(0,0,1;0rad)
  SolverId = Asm4EE
  expr: Placement = CuchillaFija011.Placement * recicladora_piezas_fijas#LCS_cuchilla_fija_salida.Placement * AttachmentOffset * recicladora_piezas_fijas#LCS_eje_central.Placement ^ -1
FEATURE [App::Link] CuchillaFijaSeparador013
  AssemblyType = Part::Link
  AttachedBy = #LCS_eje_central
  AttachedTo = CuchillaFija#LCS_cuchilla_fija_salida
  LinkPlacement = pos=(65,-65,127.535) rot=(0,0,1;0rad)
  LinkedObject = -> <external recicladora_piezas_fijas.FCStd>#Body
  Placement = pos=(65,-65,127.535) rot=(0,0,1;0rad)
  SolverId = Asm4EE
  expr: Placement = CuchillaFija012.Placement * recicladora_piezas_fijas#LCS_cuchilla_fija_salida.Placement * AttachmentOffset * recicladora_piezas_fijas#LCS_eje_central.Placement ^ -1
FEATURE [App::Link] CuchillaFijaSeparador014
  AssemblyType = Part::Link
  AttachedBy = #LCS_eje_central
  AttachedTo = CuchillaFija001#LCS_cuchilla_fija_salida
  LinkPlacement = pos=(65,-65,130.535) rot=(0,0,1;0rad)
  LinkedObject = -> <external recicladora_piezas_fijas.FCStd>#Body
  Placement = pos=(65,-65,130.535) rot=(0,0,1;0rad)
  SolverId = Asm4EE
  expr: Placement = CuchillaFija013.Placement * recicladora_piezas_fijas#LCS_cuchilla_fija_salida.Placement * AttachmentOffset * recicladora_piezas_fijas#LCS_eje_central.Placement ^ -1
FEATURE [App::Link] CuchillaFijaSeparador015
  AssemblyType = Part::Link
  AttachedBy = #LCS_eje_central
  AttachedTo = CuchillaFija002#LCS_cuchilla_fija_salida
  LinkPlacement = pos=(65,-65,133.535) rot=(0,0,1;0rad)
  LinkedObject = -> <external recicladora_piezas_fijas.FCStd>#Body
  Placement = pos=(65,-65,133.535) rot=(0,0,1;0rad)
  SolverId = Asm4EE
  expr: Placement = CuchillaFija014.Placement * recicladora_piezas_fijas#LCS_cuchilla_fija_salida.Placement * AttachmentOffset * recicladora_piezas_fijas#LCS_eje_central.Placement ^ -1
FEATURE [App::Link] CuchillaFijaSeparador016
  AssemblyType = Part::Link
  AttachedBy = #LCS_eje_central
  AttachedTo = CuchillaFija003#LCS_cuchilla_fija_salida
  LinkPlacement = pos=(65,-65,136.535) rot=(0,0,1;0rad)
  LinkedObject = -> <external recicladora_piezas_fijas.FCStd>#Body
  Placement = pos=(65,-65,136.535) rot=(0,0,1;0rad)
  SolverId = Asm4EE
  expr: Placement = CuchillaFija015.Placement * recicladora_piezas_fijas#LCS_cuchilla_fija_salida.Placement * AttachmentOffset * recicladora_piezas_fijas#LCS_eje_central.Placement ^ -1
FEATURE [App::Link] CuchillaFijaSeparador017
  AssemblyType = Part::Link
  AttachedBy = #LCS_eje_central
  AttachedTo = CuchillaFija004#LCS_cuchilla_fija_salida
  LinkPlacement = pos=(65,-65,139.535) rot=(0,0,1;0rad)
  LinkedObject = -> <external recicladora_piezas_fijas.FCStd>#Body
  Placement = pos=(65,-65,139.535) rot=(0,0,1;0rad)
  SolverId = Asm4EE
  expr: Placement = CuchillaFija016.Placement * recicladora_piezas_fijas#LCS_cuchilla_fija_salida.Placement * AttachmentOffset * recicladora_piezas_fijas#LCS_eje_central.Placement ^ -1
FEATURE [App::Link] CuchillaFijaSeparador018
  AssemblyType = Part::Link
  AttachedBy = #LCS_eje_central
  AttachedTo = CuchillaFija005#LCS_cuchilla_fija_salida
  LinkPlacement = pos=(65,-65,142.535) rot=(0,0,1;0rad)
  LinkedObject = -> <external recicladora_piezas_fijas.FCStd>#Body
  Placement = pos=(65,-65,142.535) rot=(0,0,1;0rad)
  SolverId = Asm4EE
  expr: Placement = CuchillaFija017.Placement * recicladora_piezas_fijas#LCS_cuchilla_fija_salida.Placement * AttachmentOffset * recicladora_piezas_fijas#LCS_eje_central.Placement ^ -1
FEATURE [App::Link] CuchillaFijaSeparador019
  AssemblyType = Part::Link
  AttachedBy = #LCS_eje_central
  AttachedTo = CuchillaFija006#LCS_cuchilla_fija_salida
  LinkPlacement = pos=(65,-65,145.535) rot=(0,0,1;0rad)
  LinkedObject = -> <external recicladora_piezas_fijas.FCStd>#Body
  Placement = pos=(65,-65,145.535) rot=(0,0,1;0rad)
  SolverId = Asm4EE
  expr: Placement = CuchillaFija018.Placement * recicladora_piezas_fijas#LCS_cuchilla_fija_salida.Placement * AttachmentOffset * recicladora_piezas_fijas#LCS_eje_central.Placement ^ -1
FEATURE [App::Link] CuchillaFijaSeparador020
  AssemblyType = Part::Link
  AttachedBy = #LCS_eje_central
  AttachedTo = CuchillaFija007#LCS_cuchilla_fija_salida
  LinkPlacement = pos=(65,-65,148.535) rot=(0,0,1;0rad)
  LinkedObject = -> <external recicladora_piezas_fijas.FCStd>#Body
  Placement = pos=(65,-65,148.535) rot=(0,0,1;0rad)
  SolverId = Asm4EE
  expr: Placement = CuchillaFija019.Placement * recicladora_piezas_fijas#LCS_cuchilla_fija_salida.Placement * AttachmentOffset * recicladora_piezas_fijas#LCS_eje_central.Placement ^ -1
FEATURE [App::Link] CuchillaFijaSeparador021
  AssemblyType = Part::Link
  AttachedBy = #LCS_eje_central
  AttachedTo = CuchillaFija008#LCS_cuchilla_fija_salida
  LinkPlacement = pos=(65,-65,151.535) rot=(0,0,1;0rad)
  LinkedObject = -> <external recicladora_piezas_fijas.FCStd>#Body
  Placement = pos=(65,-65,151.535) rot=(0,0,1;0rad)
  SolverId = Asm4EE
  expr: Placement = CuchillaFija020.Placement * recicladora_piezas_fijas#LCS_cuchilla_fija_salida.Placement * AttachmentOffset * recicladora_piezas_fijas#LCS_eje_central.Placement ^ -1
FEATURE [App::Link] CuchillaFijaSeparador022
  AssemblyType = Part::Link
  AttachedBy = #LCS_eje_central
  AttachedTo = CuchillaFija009#LCS_cuchilla_fija_salida
  LinkPlacement = pos=(65,-65,154.535) rot=(0,0,1;0rad)
  LinkedObject = -> <external recicladora_piezas_fijas.FCStd>#Body
  Placement = pos=(65,-65,154.535) rot=(0,0,1;0rad)
  SolverId = Asm4EE
  expr: Placement = CuchillaFija021.Placement * recicladora_piezas_fijas#LCS_cuchilla_fija_salida.Placement * AttachmentOffset * recicladora_piezas_fijas#LCS_eje_central.Placement ^ -1
FEATURE [App::Link] CuchillaFijaSeparador023
  AssemblyType = Part::Link
  AttachedBy = #LCS_eje_central
  AttachedTo = CuchillaFija010#LCS_cuchilla_fija_salida
  LinkPlacement = pos=(65,-65,157.535) rot=(0,0,1;0rad)
  LinkedObject = -> <external recicladora_piezas_fijas.FCStd>#Body
  Placement = pos=(65,-65,157.535) rot=(0,0,1;0rad)
  SolverId = Asm4EE
  expr: Placement = CuchillaFija022.Placement * recicladora_piezas_fijas#LCS_cuchilla_fija_salida.Placement * AttachmentOffset * recicladora_piezas_fijas#LCS_eje_central.Placement ^ -1
FEATURE [App::Link] SeparadorCuchilla036
  AssemblyType = Part::Link
  AttachedBy = #LCS_separador
  AttachedTo = PlacaCaja#LCS_placa_caja_salida
  AttachmentOffset = pos=(0,0,0) rot=(0,0,1;-0.10472rad)
  LinkPlacement = pos=(-1e-16,-1e-16,90.035) rot=(0.669131,-0.743145,0;3.14159rad)
  LinkedObject = -> <external recicladora_cuchillas.FCStd>#Body008
  Placement = pos=(-1e-16,-1e-16,90.035) rot=(0.669131,-0.743145,0;3.14159rad)
  SolverId = Asm4EE
  expr: .AttachmentOffset.Rotation.Angle = -Variables.angulo
  expr: Placement = PlacaCaja.Placement * recicladora_piezas_fijas#LCS_placa_caja_salida.Placement * AttachmentOffset * recicladora_cuchillas#LCS_separador.Placement ^ -1
FEATURE [App::Link] CuchillaFija024
  AssemblyType = Part::Link
  AttachedBy = #LCS_eje_central001
  AttachedTo = CuchillaFijaSeparador#LCS_cuchilla_fija_separador_salida
  LinkPlacement = pos=(65,-65,162.035) rot=(0,0,1;0rad)
  LinkedObject = -> <external recicladora_piezas_fijas.FCStd>#CuchillaFija
  Placement = pos=(65,-65,162.035) rot=(0,0,1;0rad)
  SolverId = Asm4EE
  expr: Placement = CuchillaFijaSeparador024.Placement * recicladora_piezas_fijas#LCS_cuchilla_fija_separador_salida.Placement * AttachmentOffset * recicladora_piezas_fijas#LCS_eje_central001.Placement ^ -1
FEATURE [App::Link] CuchillaFija025
  AssemblyType = Part::Link
  AttachedBy = #LCS_eje_central001
  AttachedTo = CuchillaFijaSeparador001#LCS_cuchilla_fija_separador_salida
  LinkPlacement = pos=(65,-65,165.035) rot=(0,0,1;0rad)
  LinkedObject = -> <external recicladora_piezas_fijas.FCStd>#CuchillaFija
  Placement = pos=(65,-65,165.035) rot=(0,0,1;0rad)
  SolverId = Asm4EE
  expr: Placement = CuchillaFijaSeparador025.Placement * recicladora_piezas_fijas#LCS_cuchilla_fija_separador_salida.Placement * AttachmentOffset * recicladora_piezas_fijas#LCS_eje_central001.Placement ^ -1
FEATURE [App::Link] CuchillaFija026
  AssemblyType = Part::Link
  AttachedBy = #LCS_eje_central001
  AttachedTo = CuchillaFijaSeparador002#LCS_cuchilla_fija_separador_salida
  LinkPlacement = pos=(65,-65,168.035) rot=(0,0,1;0rad)
  LinkedObject = -> <external recicladora_piezas_fijas.FCStd>#CuchillaFija
  Placement = pos=(65,-65,168.035) rot=(0,0,1;0rad)
  SolverId = Asm4EE
  expr: Placement = CuchillaFijaSeparador026.Placement * recicladora_piezas_fijas#LCS_cuchilla_fija_separador_salida.Placement * AttachmentOffset * recicladora_piezas_fijas#LCS_eje_central001.Placement ^ -1
FEATURE [App::Link] CuchillaFija027
  AssemblyType = Part::Link
  AttachedBy = #LCS_eje_central001
  AttachedTo = CuchillaFijaSeparador003#LCS_cuchilla_fija_separador_salida
  LinkPlacement = pos=(65,-65,171.035) rot=(0,0,1;0rad)
  LinkedObject = -> <external recicladora_piezas_fijas.FCStd>#CuchillaFija
  Placement = pos=(65,-65,171.035) rot=(0,0,1;0rad)
  SolverId = Asm4EE
  expr: Placement = CuchillaFijaSeparador027.Placement * recicladora_piezas_fijas#LCS_cuchilla_fija_separador_salida.Placement * AttachmentOffset * recicladora_piezas_fijas#LCS_eje_central001.Placement ^ -1
FEATURE [App::Link] CuchillaFija028
  AssemblyType = Part::Link
  AttachedBy = #LCS_eje_central001
  AttachedTo = CuchillaFijaSeparador004#LCS_cuchilla_fija_separador_salida
  LinkPlacement = pos=(65,-65,174.035) rot=(0,0,1;0rad)
  LinkedObject = -> <external recicladora_piezas_fijas.FCStd>#CuchillaFija
  Placement = pos=(65,-65,174.035) rot=(0,0,1;0rad)
  SolverId = Asm4EE
  expr: Placement = CuchillaFijaSeparador028.Placement * recicladora_piezas_fijas#LCS_cuchilla_fija_separador_salida.Placement * AttachmentOffset * recicladora_piezas_fijas#LCS_eje_central001.Placement ^ -1
FEATURE [App::Link] CuchillaFija029
  AssemblyType = Part::Link
  AttachedBy = #LCS_eje_central001
  AttachedTo = CuchillaFijaSeparador005#LCS_cuchilla_fija_separador_salida
  LinkPlacement = pos=(65,-65,177.035) rot=(0,0,1;0rad)
  LinkedObject = -> <external recicladora_piezas_fijas.FCStd>#CuchillaFija
  Placement = pos=(65,-65,177.035) rot=(0,0,1;0rad)
  SolverId = Asm4EE
  expr: Placement = CuchillaFijaSeparador029.Placement * recicladora_piezas_fijas#LCS_cuchilla_fija_separador_salida.Placement * AttachmentOffset * recicladora_piezas_fijas#LCS_eje_central001.Placement ^ -1
FEATURE [App::Link] CuchillaFija030
  AssemblyType = Part::Link
  AttachedBy = #LCS_eje_central001
  AttachedTo = CuchillaFijaSeparador006#LCS_cuchilla_fija_separador_salida
  LinkPlacement = pos=(65,-65,180.035) rot=(0,0,1;0rad)
  LinkedObject = -> <external recicladora_piezas_fijas.FCStd>#CuchillaFija
  Placement = pos=(65,-65,180.035) rot=(0,0,1;0rad)
  SolverId = Asm4EE
  expr: Placement = CuchillaFijaSeparador030.Placement * recicladora_piezas_fijas#LCS_cuchilla_fija_separador_salida.Placement * AttachmentOffset * recicladora_piezas_fijas#LCS_eje_central001.Placement ^ -1
FEATURE [App::Link] CuchillaFija031
  AssemblyType = Part::Link
  AttachedBy = #LCS_eje_central001
  AttachedTo = CuchillaFijaSeparador007#LCS_cuchilla_fija_separador_salida
  LinkPlacement = pos=(65,-65,183.035) rot=(0,0,1;0rad)
  LinkedObject = -> <external recicladora_piezas_fijas.FCStd>#CuchillaFija
  Placement = pos=(65,-65,183.035) rot=(0,0,1;0rad)
  SolverId = Asm4EE
  expr: Placement = CuchillaFijaSeparador031.Placement * recicladora_piezas_fijas#LCS_cuchilla_fija_separador_salida.Placement * AttachmentOffset * recicladora_piezas_fijas#LCS_eje_central001.Placement ^ -1
FEATURE [App::Link] CuchillaFija032
  AssemblyType = Part::Link
  AttachedBy = #LCS_eje_central001
  AttachedTo = CuchillaFijaSeparador008#LCS_cuchilla_fija_separador_salida
  LinkPlacement = pos=(65,-65,186.035) rot=(0,0,1;0rad)
  LinkedObject = -> <external recicladora_piezas_fijas.FCStd>#CuchillaFija
  Placement = pos=(65,-65,186.035) rot=(0,0,1;0rad)
  SolverId = Asm4EE
  expr: Placement = CuchillaFijaSeparador032.Placement * recicladora_piezas_fijas#LCS_cuchilla_fija_separador_salida.Placement * AttachmentOffset * recicladora_piezas_fijas#LCS_eje_central001.Placement ^ -1
FEATURE [App::Link] CuchillaFija033
  AssemblyType = Part::Link
  AttachedBy = #LCS_eje_central001
  AttachedTo = CuchillaFijaSeparador009#LCS_cuchilla_fija_separador_salida
  LinkPlacement = pos=(65,-65,189.035) rot=(0,0,1;0rad)
  LinkedObject = -> <external recicladora_piezas_fijas.FCStd>#CuchillaFija
  Placement = pos=(65,-65,189.035) rot=(0,0,1;0rad)
  SolverId = Asm4EE
  expr: Placement = CuchillaFijaSeparador033.Placement * recicladora_piezas_fijas#LCS_cuchilla_fija_separador_salida.Placement * AttachmentOffset * recicladora_piezas_fijas#LCS_eje_central001.Placement ^ -1
FEATURE [App::Link] CuchillaFija034
  AssemblyType = Part::Link
  AttachedBy = #LCS_eje_central001
  AttachedTo = CuchillaFijaSeparador010#LCS_cuchilla_fija_separador_salida
  LinkPlacement = pos=(65,-65,192.035) rot=(0,0,1;0rad)
  LinkedObject = -> <external recicladora_piezas_fijas.FCStd>#CuchillaFija
  Placement = pos=(65,-65,192.035) rot=(0,0,1;0rad)
  SolverId = Asm4EE
  expr: Placement = CuchillaFijaSeparador034.Placement * recicladora_piezas_fijas#LCS_cuchilla_fija_separador_salida.Placement * AttachmentOffset * recicladora_piezas_fijas#LCS_eje_central001.Placement ^ -1
FEATURE [App::Link] CuchillaFija035
  AssemblyType = Part::Link
  AttachedBy = #LCS_eje_central001
  AttachedTo = CuchillaFijaSeparador011#LCS_cuchilla_fija_separador_salida
  LinkPlacement = pos=(65,-65,195.035) rot=(0,0,1;0rad)
  LinkedObject = -> <external recicladora_piezas_fijas.FCStd>#CuchillaFija
  Placement = pos=(65,-65,195.035) rot=(0,0,1;0rad)
  SolverId = Asm4EE
  expr: Placement = CuchillaFijaSeparador035.Placement * recicladora_piezas_fijas#LCS_cuchilla_fija_separador_salida.Placement * AttachmentOffset * recicladora_piezas_fijas#LCS_eje_central001.Placement ^ -1
FEATURE [App::Link] CuchillaFijaSeparador024
  AssemblyType = Part::Link
  AttachedBy = #LCS_eje_central
  AttachedTo = CuchillaFija023#LCS_cuchilla_fija_salida
  LinkPlacement = pos=(65,-65,160.535) rot=(0,0,1;0rad)
  LinkedObject = -> <external recicladora_piezas_fijas.FCStd>#Body
  Placement = pos=(65,-65,160.535) rot=(0,0,1;0rad)
  SolverId = Asm4EE
  expr: Placement = CuchillaFija023.Placement * recicladora_piezas_fijas#LCS_cuchilla_fija_salida.Placement * AttachmentOffset * recicladora_piezas_fijas#LCS_eje_central.Placement ^ -1
FEATURE [App::Link] CuchillaFijaSeparador025
  AssemblyType = Part::Link
  AttachedBy = #LCS_eje_central
  AttachedTo = CuchillaFija#LCS_cuchilla_fija_salida
  LinkPlacement = pos=(65,-65,163.535) rot=(0,0,1;0rad)
  LinkedObject = -> <external recicladora_piezas_fijas.FCStd>#Body
  Placement = pos=(65,-65,163.535) rot=(0,0,1;0rad)
  SolverId = Asm4EE
  expr: Placement = CuchillaFija024.Placement * recicladora_piezas_fijas#LCS_cuchilla_fija_salida.Placement * AttachmentOffset * recicladora_piezas_fijas#LCS_eje_central.Placement ^ -1
FEATURE [App::Link] CuchillaFijaSeparador026
  AssemblyType = Part::Link
  AttachedBy = #LCS_eje_central
  AttachedTo = CuchillaFija001#LCS_cuchilla_fija_salida
  LinkPlacement = pos=(65,-65,166.535) rot=(0,0,1;0rad)
  LinkedObject = -> <external recicladora_piezas_fijas.FCStd>#Body
  Placement = pos=(65,-65,166.535) rot=(0,0,1;0rad)
  SolverId = Asm4EE
  expr: Placement = CuchillaFija025.Placement * recicladora_piezas_fijas#LCS_cuchilla_fija_salida.Placement * AttachmentOffset * recicladora_piezas_fijas#LCS_eje_central.Placement ^ -1
FEATURE [App::Link] CuchillaFijaSeparador027
  AssemblyType = Part::Link
  AttachedBy = #LCS_eje_central
  AttachedTo = CuchillaFija002#LCS_cuchilla_fija_salida
  LinkPlacement = pos=(65,-65,169.535) rot=(0,0,1;0rad)
  LinkedObject = -> <external recicladora_piezas_fijas.FCStd>#Body
  Placement = pos=(65,-65,169.535) rot=(0,0,1;0rad)
  SolverId = Asm4EE
  expr: Placement = CuchillaFija026.Placement * recicladora_piezas_fijas#LCS_cuchilla_fija_salida.Placement * AttachmentOffset * recicladora_piezas_fijas#LCS_eje_central.Placement ^ -1
FEATURE [App::Link] CuchillaFijaSeparador028
  AssemblyType = Part::Link
  AttachedBy = #LCS_eje_central
  AttachedTo = CuchillaFija003#LCS_cuchilla_fija_salida
  LinkPlacement = pos=(65,-65,172.535) rot=(0,0,1;0rad)
  LinkedObject = -> <external recicladora_piezas_fijas.FCStd>#Body
  Placement = pos=(65,-65,172.535) rot=(0,0,1;0rad)
  SolverId = Asm4EE
  expr: Placement = CuchillaFija027.Placement * recicladora_piezas_fijas#LCS_cuchilla_fija_salida.Placement * AttachmentOffset * recicladora_piezas_fijas#LCS_eje_central.Placement ^ -1
FEATURE [App::Link] CuchillaFijaSeparador029
  AssemblyType = Part::Link
  AttachedBy = #LCS_eje_central
  AttachedTo = CuchillaFija004#LCS_cuchilla_fija_salida
  LinkPlacement = pos=(65,-65,175.535) rot=(0,0,1;0rad)
  LinkedObject = -> <external recicladora_piezas_fijas.FCStd>#Body
  Placement = pos=(65,-65,175.535) rot=(0,0,1;0rad)
  SolverId = Asm4EE
  expr: Placement = CuchillaFija028.Placement * recicladora_piezas_fijas#LCS_cuchilla_fija_salida.Placement * AttachmentOffset * recicladora_piezas_fijas#LCS_eje_central.Placement ^ -1
FEATURE [App::Link] CuchillaFijaSeparador030
  AssemblyType = Part::Link
  AttachedBy = #LCS_eje_central
  AttachedTo = CuchillaFija005#LCS_cuchilla_fija_salida
  LinkPlacement = pos=(65,-65,178.535) rot=(0,0,1;0rad)
  LinkedObject = -> <external recicladora_piezas_fijas.FCStd>#Body
  Placement = pos=(65,-65,178.535) rot=(0,0,1;0rad)
  SolverId = Asm4EE
  expr: Placement = CuchillaFija029.Placement * recicladora_piezas_fijas#LCS_cuchilla_fija_salida.Placement * AttachmentOffset * recicladora_piezas_fijas#LCS_eje_central.Placement ^ -1
FEATURE [App::Link] CuchillaFijaSeparador031
  AssemblyType = Part::Link
  AttachedBy = #LCS_eje_central
  AttachedTo = CuchillaFija006#LCS_cuchilla_fija_salida
  LinkPlacement = pos=(65,-65,181.535) rot=(0,0,1;0rad)
  LinkedObject = -> <external recicladora_piezas_fijas.FCStd>#Body
  Placement = pos=(65,-65,181.535) rot=(0,0,1;0rad)
  SolverId = Asm4EE
  expr: Placement = CuchillaFija030.Placement * recicladora_piezas_fijas#LCS_cuchilla_fija_salida.Placement * AttachmentOffset * recicladora_piezas_fijas#LCS_eje_central.Placement ^ -1
FEATURE [App::Link] CuchillaFijaSeparador032
  AssemblyType = Part::Link
  AttachedBy = #LCS_eje_central
  AttachedTo = CuchillaFija007#LCS_cuchilla_fija_salida
  LinkPlacement = pos=(65,-65,184.535) rot=(0,0,1;0rad)
  LinkedObject = -> <external recicladora_piezas_fijas.FCStd>#Body
  Placement = pos=(65,-65,184.535) rot=(0,0,1;0rad)
  SolverId = Asm4EE
  expr: Placement = CuchillaFija031.Placement * recicladora_piezas_fijas#LCS_cuchilla_fija_salida.Placement * AttachmentOffset * recicladora_piezas_fijas#LCS_eje_central.Placement ^ -1
FEATURE [App::Link] CuchillaFijaSeparador033
  AssemblyType = Part::Link
  AttachedBy = #LCS_eje_central
  AttachedTo = CuchillaFija008#LCS_cuchilla_fija_salida
  LinkPlacement = pos=(65,-65,187.535) rot=(0,0,1;0rad)
  LinkedObject = -> <external recicladora_piezas_fijas.FCStd>#Body
  Placement = pos=(65,-65,187.535) rot=(0,0,1;0rad)
  SolverId = Asm4EE
  expr: Placement = CuchillaFija032.Placement * recicladora_piezas_fijas#LCS_cuchilla_fija_salida.Placement * AttachmentOffset * recicladora_piezas_fijas#LCS_eje_central.Placement ^ -1
FEATURE [App::Link] CuchillaFijaSeparador034
  AssemblyType = Part::Link
  AttachedBy = #LCS_eje_central
  AttachedTo = CuchillaFija009#LCS_cuchilla_fija_salida
  LinkPlacement = pos=(65,-65,190.535) rot=(0,0,1;0rad)
  LinkedObject = -> <external recicladora_piezas_fijas.FCStd>#Body
  Placement = pos=(65,-65,190.535) rot=(0,0,1;0rad)
  SolverId = Asm4EE
  expr: Placement = CuchillaFija033.Placement * recicladora_piezas_fijas#LCS_cuchilla_fija_salida.Placement * AttachmentOffset * recicladora_piezas_fijas#LCS_eje_central.Placement ^ -1
FEATURE [App::Link] CuchillaFijaSeparador035
  AssemblyType = Part::Link
  AttachedBy = #LCS_eje_central
  AttachedTo = CuchillaFija010#LCS_cuchilla_fija_salida
  LinkPlacement = pos=(65,-65,193.535) rot=(0,0,1;0rad)
  LinkedObject = -> <external recicladora_piezas_fijas.FCStd>#Body
  Placement = pos=(65,-65,193.535) rot=(0,0,1;0rad)
  SolverId = Asm4EE
  expr: Placement = CuchillaFija034.Placement * recicladora_piezas_fijas#LCS_cuchilla_fija_salida.Placement * AttachmentOffset * recicladora_piezas_fijas#LCS_eje_central.Placement ^ -1
FEATURE [App::Link] SeparadorCuchilla037
  AssemblyType = Part::Link
  AttachedBy = #LCS_separador
  AttachedTo = PlacaCaja#LCS_placa_caja_salida
  AttachmentOffset = pos=(0,0,0) rot=(0,0,1;-0.10472rad)
  LinkPlacement = pos=(-1e-16,-1e-16,90.035) rot=(0.669131,-0.743145,0;3.14159rad)
  LinkedObject = -> <external recicladora_cuchillas.FCStd>#Body008
  Placement = pos=(-1e-16,-1e-16,90.035) rot=(0.669131,-0.743145,0;3.14159rad)
  SolverId = Asm4EE
  expr: .AttachmentOffset.Rotation.Angle = -Variables.angulo
  expr: Placement = PlacaCaja.Placement * recicladora_piezas_fijas#LCS_placa_caja_salida.Placement * AttachmentOffset * recicladora_cuchillas#LCS_separador.Placement ^ -1
FEATURE [App::Link] SeparadorCuchilla038
  AssemblyType = Part::Link
  AttachedBy = #LCS_separador
  AttachedTo = Cuchilla006020#LCS_cuchilla_salida005
  LinkPlacement = pos=(-8.44e-14,2.01e-14,198.035) rot=(0.951057,-0.309017,0;3.14159rad)
  LinkedObject = -> <external recicladora_cuchillas.FCStd>#Body008
  Placement = pos=(-8.44e-14,2.01e-14,198.035) rot=(0.951057,-0.309017,0;3.14159rad)
  SolverId = Asm4EE
  expr: Placement = Cuchilla006020.Placement * recicladora_cuchillas#LCS_cuchilla_salida005.Placement * AttachmentOffset * recicladora_cuchillas#LCS_separador.Placement ^ -1
FEATURE [App::Link] CuchillaFijaSeparador036
  AssemblyType = Part::Link
  AttachedBy = #LCS_eje_central
  AttachedTo = CuchillaFija035#LCS_cuchilla_fija_salida
  LinkPlacement = pos=(65,-65,196.535) rot=(0,0,1;0rad)
  LinkedObject = -> <external recicladora_piezas_fijas.FCStd>#Body
  Placement = pos=(65,-65,196.535) rot=(0,0,1;0rad)
  SolverId = Asm4EE
  expr: Placement = CuchillaFija035.Placement * recicladora_piezas_fijas#LCS_cuchilla_fija_salida.Placement * AttachmentOffset * recicladora_piezas_fijas#LCS_eje_central.Placement ^ -1
FEATURE [App::Link] PlacaCaja001
  AssemblyType = Part::Link
  AttachedBy = #LCS_eje_central003
  AttachedTo = CuchillaFijaSeparador036#LCS_cuchilla_fija_separador_salida
  LinkPlacement = pos=(65,-65,198.035) rot=(0,0,1;0rad)
  LinkedObject = -> <external recicladora_piezas_fijas.FCStd>#CuchillaFija002
  Placement = pos=(65,-65,198.035) rot=(0,0,1;0rad)
  SolverId = Asm4EE
  expr: Placement = CuchillaFijaSeparador036.Placement * recicladora_piezas_fijas#LCS_cuchilla_fija_separador_salida.Placement * AttachmentOffset * recicladora_piezas_fijas#LCS_eje_central003.Placement ^ -1
FEATURE [App::Link] Rodamiento002
  AssemblyType = Part::Link
  AttachedBy = #LCS_0
  AttachedTo = CuchillaFijaSeparador036#LCS_cuchilla_fija_separador_salida
  LinkPlacement = pos=(0,-7.1e-15,198.035) rot=(0.57735,0.57735,-0.57735;2.0944rad)
  LinkedObject = -> Rodamiento
  Placement = pos=(0,-7.1e-15,198.035) rot=(0.57735,0.57735,-0.57735;2.0944rad)
  SolverId = Asm4EE
  expr: Placement = CuchillaFijaSeparador036.Placement * recicladora_piezas_fijas#LCS_cuchilla_fija_separador_salida.Placement * AttachmentOffset * LCS_0.Placement ^ -1
FEATURE [App::Link] SeparadorCuchillaFinal
  AssemblyType = Part::Link
  AttachedBy = #LCS_separador_entrada001
  AttachedTo = PlacaCaja001#LCS_eje_central003
  AttachmentOffset = pos=(0,0,0) rot=(0,0,1;-0.10472rad)
  LinkPlacement = pos=(-4e-16,-3.5e-15,198.035) rot=(0,0,1;4.60767rad)
  LinkedObject = -> <external recicladora_cuchillas.FCStd>#Body014
  Placement = pos=(-4e-16,-3.5e-15,198.035) rot=(0,0,1;4.60767rad)
  SolverId = Asm4EE
  expr: .AttachmentOffset.Rotation.Angle = -Variables.angulo
  expr: Placement = PlacaCaja001.Placement * recicladora_piezas_fijas#LCS_eje_central003.Placement * AttachmentOffset * recicladora_cuchillas#LCS_separador_entrada001.Placement ^ -1
FEATURE [App::Link] PlacaFondo
  AssemblyType = Part::Link
  AttachedBy = #LCS_Placa_Fondo_Entrada
  AttachedTo = PlacaCaja#LCS_Placa_Salida_Fondo
  LinkPlacement = pos=(-51,5,143.285) rot=(0,-1,0;1.5708rad)
  LinkedObject = -> <external recicladora_piezas_fijas.FCStd>#Body001
  Placement = pos=(-51,5,143.285) rot=(0,-1,0;1.5708rad)
  SolverId = Asm4EE
  expr: Placement = PlacaCaja.Placement * recicladora_piezas_fijas#LCS_Placa_Salida_Fondo.Placement * AttachmentOffset * recicladora_piezas_fijas#LCS_Placa_Fondo_Entrada.Placement ^ -1
FEATURE [App::Link] Placa_union
  AssemblyType = Part::Link
  AttachedBy = #LCS_Placa_Union_Entrada
  AttachedTo = PlacaCaja001#LCS_Placa_union_salida
  AttachmentOffset = pos=(0,0,0) rot=(0,0,1;3.14159rad)
  LinkPlacement = pos=(-58.75,5,198.035) rot=(0,-1,0;3.14159rad)
  LinkedObject = -> <external recicladora_piezas_fijas.FCStd>#Body002
  Placement = pos=(-58.75,5,198.035) rot=(0,-1,0;3.14159rad)
  SolverId = Asm4EE
  expr: Placement = PlacaCaja001.Placement * recicladora_piezas_fijas#LCS_Placa_union_salida.Placement * AttachmentOffset * recicladora_piezas_fijas#LCS_Placa_Union_Entrada.Placement ^ -1
FEATURE [App::Link] Placa_union001
  AssemblyType = Part::Link
  AttachedBy = #LCS_Paca_union_entrada_2
  AttachedTo = PlacaCaja#LCS_Placa_union_salida001
  AttachmentOffset = pos=(0,0,0) rot=(-1,0,0;3.14159rad)
  LinkPlacement = pos=(-58.75,5,90.035) rot=(0,1,0;3.14159rad)
  LinkedObject = -> <external recicladora_piezas_fijas.FCStd>#Body002
  Placement = pos=(-58.75,5,90.035) rot=(0,1,0;3.14159rad)
  SolverId = Asm4EE
  expr: Placement = PlacaCaja.Placement * recicladora_piezas_fijas#LCS_Placa_union_salida001.Placement * AttachmentOffset * recicladora_piezas_fijas#LCS_Paca_union_entrada_2.Placement ^ -1
FEATURE [App::Part] Model
  AssemblyType = Part::Link
  Group = -> [LCS_Origin,Constraints,Variables,Configurations,EjeCentral,Rodamiento001,SeparadorCuchillaInicial,PlacaCaja,CuchillaFijaSeparador,CuchillaFija,CuchillaFijaSeparador001,CuchillaFija001,CuchillaFijaSeparador002,CuchillaFija002,CuchillaFijaSeparador003,CuchillaFija003,SeparadorCuchilla,Cuchilla001,SeparadorCuchilla001,Cuchilla002,SeparadorCuchilla002,Cuchilla003,SeparadorCuchilla003,Cuchilla004,+138 more]
  Origin = -> Origin001
  Type = Assembly

RESOLVED EXTERNAL PARTS (link-assembly join: the EXTERNAL_REF files above that resolve inside this repo's crawl, each included once):
---- part recicladora_cuchillas.FCStd = doc fcstd_128981c37c2e (88179 chars; too large to inline — full recipe in that document) ----
---- part recicladora_eje.FCStd = doc fcstd_a445973c1eb2 ----
FCSTD DOCUMENT  (FreeCAD 0.20R29177 (Git))
Label: recicladora_eje
License: Creative Commons Attribution-ShareAlike
LicenseURL: http://creativecommons.org/licenses/by-sa/4.0/
objects: Sketcher::SketchObject×7, PartDesign::CoordinateSystem×3, PartDesign::Pad×3, PartDesign::Fillet×2, PartDesign::Body×2, Part::Feature×1, PartDesign::FeatureBase×1, PartDesign::Groove×1, PartDesign::Plane×1, PartDesign::SubtractiveLoft×1
note: 29 computed .brp shape members not serialized (recipe doc carries the construction recipe); baked Part::Feature solids carry a one-line shape summary decoded from their .brp

FEATURE [Part::Feature] EjeOriginal001
  shape: bbox 44.36 x 44.36 x 249.7 mm, 20 faces (baked)
FEATURE [PartDesign::FeatureBase] BaseFeature
  BaseFeature = -> EjeOriginal001
FEATURE [PartDesign::CoordinateSystem] LCS_0
  AttacherType = Attacher::AttachEngine3D
  MapMode = 2
  Support = -> [X_Axis002]
FEATURE [Sketcher::SketchObject] Sketch
  ExternalGeometry = -> [BaseFeature]
  FullyConstrained = true
  MapMode = 5
  Placement = pos=(0,0,0) rot=(1,0,0;1.5708rad)
  Support = -> [XZ_Plane]
  expr: Constraints[12] = 10 / 2
  sketch-geometry (7):
    g0: LineSegment StartX=15.75 StartY=-96.74 StartZ=0 EndX=15.75 EndY=-26 EndZ=0
    g1: LineSegment StartX=15.75 StartY=-26 StartZ=0 EndX=5 EndY=-55.5354 EndZ=0
    g2: LineSegment StartX=5 StartY=-55.5354 StartZ=0 EndX=5 EndY=-85.5354 EndZ=0
    g3: LineSegment StartX=5 StartY=-85.5354 StartZ=0 EndX=0 EndY=-85.5354 EndZ=0
    g4: LineSegment StartX=0 StartY=-85.5354 StartZ=0 EndX=0 EndY=-96.74 EndZ=0
    g5: LineSegment StartX=0 StartY=-96.74 StartZ=0 EndX=15.75 EndY=-96.74 EndZ=0
    g6: LineSegment StartX=15.75 StartY=-16 StartZ=0 EndX=15.75 EndY=-26 EndZ=0
  constraints (19):
    c: Vertical(g0)
    c: Coincident(g0,g1)
    c: Coincident(g1,g2)
    c: Coincident(g2,g3)
    c: PointOnObject(g3,g-2)
    c: Horizontal(g3)
    c: Coincident(g3,g4)
    c: PointOnObject(g4,g-7)
    c: Vertical(g4)
    c: Coincident(g4,g5)
    c: Coincident(g5,g-8)
    c: Coincident(g0,g5)
    c: DistanceX(g3,g3) = 5
    c: Vertical(g2)
    c: Coincident(g6,g-8)
    c: Coincident(g6,g0)
    c: Angle(g1,g0) = 0.349066
    c: DistanceY(g2,g2) = 30
    c: DistanceY(g6,g6) = 10
FEATURE [PartDesign::Groove] Groove
  Angle = 360
  Axis = (0,2e-16,1)
  Base = (0,0,0)
  BaseFeature = -> BaseFeature
  Profile = -> Sketch
  ReferenceAxis = -> Sketch [V_Axis]
FEATURE [Sketcher::SketchObject] Sketch005
  FullyConstrained = true
  MapMode = 5
  Support = -> [XY_Plane002]
  expr: Constraints[19] = 31.22
  sketch-geometry (7):
    g0: LineSegment StartX=15.61 StartY=-9.01244 StartZ=0 EndX=15.61 EndY=9.01244 EndZ=0
    g1: LineSegment StartX=15.61 StartY=9.01244 StartZ=0 EndX=-1.8e-15 EndY=18.0249 EndZ=0
    g2: LineSegment StartX=-1.8e-15 StartY=18.0249 StartZ=0 EndX=-15.61 EndY=9.01244 EndZ=0
    g3: LineSegment StartX=-15.61 StartY=9.01244 StartZ=0 EndX=-15.61 EndY=-9.01244 EndZ=0
    g4: LineSegment StartX=-15.61 StartY=-9.01244 StartZ=0 EndX=0 EndY=-18.0249 EndZ=0
    g5: LineSegment StartX=0 StartY=-18.0249 StartZ=0 EndX=15.61 EndY=-9.01244 EndZ=0
    g6: Circle CenterX=0 CenterY=0 CenterZ=0 NormalX=0 NormalY=0 NormalZ=1 AngleXU=0 Radius=18.0249
  constraints (16):
    c: Coincident(g0,g1)
    c: Coincident(g1,g2)
    c: Coincident(g2,g3)
    c: Coincident(g3,g4)
    c: Coincident(g4,g5)
    c: Coincident(g5,g0)
    c: Equal(g0, g1-g5) x5
    c: PointOnObject(g0,g6)
    c: PointOnObject(g1,g6)
    c: PointOnObject(g2,g6)
    c: PointOnObject(g3,g6)
    c: PointOnObject(g4,g6)
    c: PointOnObject(g5,g6)
    c: Coincident(g6,g-1)
    c: Vertical(g0)
    c: DistanceX(g2,g0) = 31.22
FEATURE [PartDesign::Pad] Pad003
  Direction = (0,0,1)
  Length = 153
  Length2 = 10
  Profile = -> Sketch005
  ReferenceAxis = -> Sketch005 [N_Axis]
  Type = 0
FEATURE [Sketcher::SketchObject] Sketch006
  FullyConstrained = true
  MapMode = 5
  Placement = pos=(0,0,0) rot=(1,0,0;3.14159rad)
  Support = -> [Pad003]
  sketch-geometry (1):
    g0: Circle CenterX=0 CenterY=0 CenterZ=0 NormalX=0 NormalY=0 NormalZ=1 AngleXU=0 Radius=22.18
  constraints (2):
    c: Coincident(g0,g-1)
    c: Diameter(g0) = 44.36
FEATURE [PartDesign::Pad] Pad004
  BaseFeature = -> Pad003
  Direction = (0,0,-1)
  Length = 13
  Length2 = 10
  Profile = -> Sketch006
  ReferenceAxis = -> Sketch006 [N_Axis]
  Type = 0
FEATURE [Sketcher::SketchObject] Sketch007
  FullyConstrained = true
  MapMode = 5
  Placement = pos=(0,0,-13) rot=(1,0,0;3.14159rad)
  Support = -> [Pad004]
  expr: Constraints[1] = 31.5
  sketch-geometry (1):
    g0: Circle CenterX=0 CenterY=0 CenterZ=0 NormalX=0 NormalY=0 NormalZ=1 AngleXU=0 Radius=15.75
  constraints (2):
    c: Coincident(g0,g-1)
    c: Diameter(g0) = 31.5
FEATURE [PartDesign::Pad] Pad005
  BaseFeature = -> Pad004
  Direction = (0,0,-1)
  Length = 83.74
  Length2 = 10
  Profile = -> Sketch007
  ReferenceAxis = -> Sketch007 [N_Axis]
  Type = 0
  expr: Length = 83.73999999999999
FEATURE [PartDesign::Fillet] Fillet
  Base = -> Pad005 [Edge8,Edge9,Edge7,Edge6,Edge4,Edge5]
  BaseFeature = -> Pad005
  Radius = 3
  SupportTransform = false
  UseAllEdges = false
FEATURE [PartDesign::Fillet] Fillet001
  Base = -> Fillet [Edge34]
  BaseFeature = -> Fillet
  Radius = 3
  SupportTransform = false
  UseAllEdges = false
FEATURE [PartDesign::Plane] DatumPlane
  AttachmentOffset = pos=(0,0,-4.275) rot=(0,0,1;0rad)
  Length = 60
  MapMode = 5
  Placement = pos=(0,0,148.725) rot=(0,0,1;0rad)
  ResizeMode = 0
  Support = -> [Fillet001]
  Width = 60
  expr: .AttachmentOffset.Base.z = (27.5 - 36.05) / 2
FEATURE [Sketcher::SketchObject] Sketch008
  FullyConstrained = false
  MapMode = 5
  Placement = pos=(0,0,153) rot=(0,0,1;0rad)
  Support = -> [Fillet001]
  expr: Constraints[1] = 27.5
  sketch-geometry (2):
    g0: Circle CenterX=0 CenterY=0 CenterZ=0 NormalX=0 NormalY=0 NormalZ=1 AngleXU=0 Radius=13.75
    g1: Circle CenterX=0 CenterY=0 CenterZ=0 NormalX=0 NormalY=0 NormalZ=1 AngleXU=0 Radius=33.668
  constraints (3):
    c: Coincident(g0,g-1)
    c: Diameter(g0) = 27.5
    c: Coincident(g1,g0)
FEATURE [Sketcher::SketchObject] Sketch009
  ExternalGeometry = -> [Fillet001]
  FullyConstrained = false
  MapMode = 5
  Placement = pos=(0,0,148.725) rot=(0,0,1;0rad)
  Support = -> [DatumPlane]
  sketch-geometry (2):
    g0: Circle CenterX=0 CenterY=0 CenterZ=0 NormalX=0 NormalY=0 NormalZ=1 AngleXU=0 Radius=18.0249
    g1: Circle CenterX=0 CenterY=0 CenterZ=0 NormalX=0 NormalY=0 NormalZ=1 AngleXU=0 Radius=33.5558
  constraints (3):
    c: Coincident(g0,g-1)
    c: PointOnObject(g-3,g0)
    c: Coincident(g1,g0)
FEATURE [PartDesign::SubtractiveLoft] SubtractiveLoft001
  BaseFeature = -> Fillet001
  Closed = false
  Profile = -> Sketch008
  Ruled = false
  Sections = -> [Sketch009]
FEATURE [PartDesign::Body] EjeOriginal
  Group = -> [LCS_0,Sketch005,Pad003,Sketch006,Pad004,Sketch007,Pad005,Fillet,Fillet001,Sketch008,DatumPlane,Sketch009,SubtractiveLoft001]
  LabelDocUser = recicladora
  LabelPartUser = EjeOriginal
  Origin = -> Origin002
  Tip = -> SubtractiveLoft001
FEATURE [PartDesign::CoordinateSystem] LCS_eje_central_entrada
  AttacherType = Attacher::AttachEngine3D
  MapMode = 11
  Placement = pos=(0,-1.9e-14,-85.5354) rot=(0,0,1;1.5708rad)
  Support = -> [Groove]
FEATURE [Sketcher::SketchObject] Sketch010
  ExternalGeometry = -> [Groove]
  FullyConstrained = true
  MapMode = 5
  Support = -> [Groove]
  sketch-geometry (7):
    g0: Circle CenterX=0 CenterY=0 CenterZ=0 NormalX=0 NormalY=0 NormalZ=1 AngleXU=0 Radius=22.18
    g1: LineSegment StartX=-18.61 StartY=10.7445 StartZ=0 EndX=0 EndY=21.489 EndZ=0
    g2: LineSegment StartX=0 StartY=21.489 StartZ=0 EndX=18.61 EndY=10.7445 EndZ=0
    g3: LineSegment StartX=-18.61 StartY=10.7445 StartZ=0 EndX=-18.61 EndY=-10.7445 EndZ=0
    g4: LineSegment StartX=18.61 StartY=10.7445 StartZ=0 EndX=18.61 EndY=-10.7445 EndZ=0
    g5: LineSegment StartX=18.61 StartY=-10.7445 StartZ=0 EndX=3.6e-15 EndY=-21.489 EndZ=0
    g6: LineSegment StartX=3.6e-15 StartY=-21.489 StartZ=0 EndX=-18.61 EndY=-10.7445 EndZ=0
  constraints (14):
    c: Coincident(g0,g-3)
    c: Equal(g0,g-3)
    c: Coincident(g1,g-4)
    c: Coincident(g1,g-5)
    c: Coincident(g2,g1)
    c: Coincident(g2,g-5)
    c: Coincident(g3,g1)
    c: Coincident(g3,g-6)
    c: Coincident(g2,g4)
    c: Coincident(g4,g-8)
    c: Coincident(g4,g5)
    c: Coincident(g5,g-9)
    c: Coincident(g5,g6)
    c: Coincident(g6,g3)
FEATURE [PartDesign::CoordinateSystem] LCS_eje_central_salida
  AttacherType = Attacher::AttachEngine3D
  MapMode = 11
  Support = -> [Sketch010]
FEATURE [PartDesign::Body] EjeCentral
  BaseFeature = -> EjeOriginal001
  Group = -> [BaseFeature,Sketch,Groove,LCS_eje_central_salida,LCS_eje_central_entrada,Sketch010]
  Origin = -> Origin
  Tip = -> Groove
---- part recicladora_piezas_fijas.FCStd = doc fcstd_8e03c54b985e ----
FCSTD DOCUMENT  (FreeCAD 0.19R)
Label: recicladora_piezas_fijas
License: Creative Commons Attribution-ShareAlike
LicenseURL: http://creativecommons.org/licenses/by-sa/4.0/
objects: PartDesign::CoordinateSystem×14, Sketcher::SketchObject×13, PartDesign::Pad×8, PartDesign::Body×6, PartDesign::Fillet×4, PartDesign::Hole×3, PartDesign::Pocket×2, PartDesign::Chamfer×2, App::FeaturePython×1, PartDesign::Line×1
note: 72 computed .brp shape members not serialized (recipe doc carries the construction recipe); baked Part::Feature solids carry a one-line shape summary decoded from their .brp

FEATURE [App::FeaturePython] dd  # WARN: FeaturePython — macro-defined, semantics opaque (R4)
  DynamicData = Created with DynamicData (v2.46) workbench. | This is a simple container object built | for holding custom properties.
  ddAlturaEjeCentral = 65
  ddAlturaHueco = 12.5
  ddAlturaPlaca = 140
  ddAlturaSuperiorNotch = 41
  ddAnchoBarra = 21
  ddAnchoHexagono = 31.22
  ddAnchuraEjeCentral = 65
  ddDiametroEntrada = 88
  ddDiametroHollo = 11
  ddDiametroMayor = 100
  ddDiametroSeparador = 55
  ddDistanciaHollos = 110
  ddGrosorPlaca = 1.5
  ddMargen = 1
  ddNotchHeight = 20
FEATURE [Sketcher::SketchObject] Sketch001
  FullyConstrained = true
  MapMode = 5
  Support = -> [XY_Plane]
  expr: Constraints[39] = dd.ddDiametroSeparador
  expr: Constraints[37] = dd.ddAlturaEjeCentral
  expr: Constraints[36] = dd.ddAnchuraEjeCentral
  expr: Constraints[38] = dd.ddAlturaEjeCentral
  expr: Constraints[32] = dd.ddAlturaSuperiorNotch
  expr: Constraints[29] = dd.ddGrosorPlaca
  expr: Constraints[26] = dd.ddDiametroHollo
  expr: Constraints[24] = dd.ddDistanciaHollos
  expr: Constraints[19] = dd.ddDiametroEntrada
  expr: Constraints[27] = dd.ddAlturaHueco
  expr: Constraints[17] = dd.ddAlturaPlaca
  expr: Constraints[14] = dd.ddAnchoBarra
  sketch-geometry (16):
    g0: LineSegment StartX=0 StartY=140 StartZ=0 EndX=-21 EndY=140 EndZ=0
    g1: LineSegment StartX=-21 StartY=140 StartZ=0 EndX=-21 EndY=130 EndZ=0
    g2: ArcOfCircle CenterX=-65 CenterY=130 CenterZ=0 NormalX=0 NormalY=0 NormalZ=1 AngleXU=0 Radius=44 StartAngle=5.04594 EndAngle=6.28319
    g3: ArcOfCircle CenterX=-25 CenterY=53.6515 CenterZ=0 NormalX=0 NormalY=0 NormalZ=1 AngleXU=0 Radius=4 StartAngle=6e-16 EndAngle=1.5708
    g4: LineSegment StartX=-21 StartY=53.6515 StartZ=0 EndX=-21 EndY=41 EndZ=0
    g5: LineSegment StartX=-21 StartY=41 StartZ=0 EndX=-19.5633 EndY=40.569 EndZ=0
    g6: LineSegment StartX=-19.5633 StartY=40.569 StartZ=0 EndX=-21 EndY=35.7798 EndZ=0
    g7: LineSegment StartX=-21 StartY=35.7798 StartZ=0 EndX=-21 EndY=0 EndZ=0
    g8: LineSegment StartX=-21 StartY=0 StartZ=0 EndX=0 EndY=0 EndZ=0
    g9: LineSegment StartX=0 StartY=0 StartZ=0 EndX=0 EndY=140 EndZ=0
    g10: Circle CenterX=-10.5 CenterY=12.5 CenterZ=0 NormalX=0 NormalY=0 NormalZ=-1 AngleXU=0 Radius=5.5
    g11: Circle CenterX=-10.5 CenterY=122.5 CenterZ=0 NormalX=0 NormalY=0 NormalZ=-1 AngleXU=0 Radius=5.5
    g12: GeomPoint X=-10.5 Y=0 Z=0
    g13: ArcOfCircle CenterX=-65 CenterY=65 CenterZ=0 NormalX=0 NormalY=0 NormalZ=1 AngleXU=0 Radius=27.5 StartAngle=6.01268 EndAngle=7.30263
    g14: LineSegment StartX=-25 StartY=57.6515 StartZ=0 EndX=-38.5 EndY=57.6515 EndZ=0
    g15: LineSegment StartX=-37.5 StartY=65 StartZ=0 EndX=-37.5 EndY=57.6515 EndZ=0
  constraints (45):
    c: Coincident(g7,g8)
    c: Coincident(g8,g9)
    c: Coincident(g0,g9)
    c: Coincident(g0,g1)
    c: Coincident(g4,g5)
    c: Coincident(g5,g6)
    c: Coincident(g6,g7)
    c: Vertical(g9)
    c: Vertical(g7)
    c: Vertical(g4)
    c: Vertical(g1)
    c: Horizontal(g0)
    c: Tangent(g3,g4) = 1.5708
    c: Tangent(g1,g2) = 1.5708
    c: DistanceX(g8,g8) = 21
    c: Symmetric(g7,g8,g12)
    c: Vertical(g12,g10)
    c: DistanceY(g9,g9) = 140
    c: Radius(g3) = 4
    c: Diameter(g2) = 88
    c: Vertical(g10,g11)
    c: Vertical(g6,g4)
    c: Horizontal(g8)
    c: Coincident(g8,g-1)
    c: DistanceY(g10,g11) = 110
    c: Equal(g11,g10)
    c: Diameter(g11) = 11
    c: DistanceY(g8,g10) = 12.5
    c: Angle(g5,g6) = 1.5708
    c: Distance(g5) = 1.5
    c: Vertical(g1,g7)
    c: Distance(g6) = 5
    c: DistanceY(g-1,g4) = 41
    c: Coincident(g2,g13)
    c: Horizontal(g14)
    c: Coincident(g13,g14)
    c: DistanceX(g13,g-1) = 65
    c: DistanceY(g-1,g13) = 65
    c: DistanceY(g13,g2) = 65
    c: Diameter(g13) = 55
    c: Tangent(g3,g14) = -1.5708
    c: Vertical(g15)
    c: DistanceX(g13,g15) = 1
    c: Horizontal(g15,g13)
    c: Tangent(g15,g13) = 1.5708
FEATURE [Sketcher::SketchObject] Sketch002
  FullyConstrained = true
  MapMode = 5
  Support = -> [XY_Plane002]
  expr: Constraints[36] = dd.ddAlturaEjeCentral
  expr: Constraints[29] = dd.ddAlturaSuperiorNotch
  expr: Constraints[24] = dd.ddGrosorPlaca
  expr: Constraints[30] = dd.ddAnchoBarra
  expr: Constraints[28] = dd.ddAnchuraEjeCentral
  expr: Constraints[25] = dd.ddAlturaEjeCentral
  expr: Constraints[21] = dd.ddDiametroHollo
  expr: Constraints[19] = dd.ddDistanciaHollos
  expr: Constraints[22] = dd.ddAlturaHueco
  expr: Constraints[14] = dd.ddAlturaPlaca
  sketch-geometry (12):
    g0: LineSegment StartX=0 StartY=140 StartZ=0 EndX=-21 EndY=140 EndZ=0
    g1: LineSegment StartX=-21 StartY=140 StartZ=0 EndX=-21 EndY=130 EndZ=0
    g2: ArcOfCircle CenterX=-65 CenterY=130 CenterZ=0 NormalX=0 NormalY=0 NormalZ=1 AngleXU=0 Radius=44 StartAngle=5.59137 EndAngle=6.28319
    g3: ArcOfCircle CenterX=-65 CenterY=65 CenterZ=0 NormalX=0 NormalY=0 NormalZ=1 AngleXU=0 Radius=50.1199 StartAngle=5.78384 EndAngle=7.11158
    g4: LineSegment StartX=-21 StartY=41 StartZ=0 EndX=-19.5633 EndY=40.569 EndZ=0
    g5: LineSegment StartX=-19.5633 StartY=40.569 StartZ=0 EndX=-21 EndY=35.7798 EndZ=0
    g6: LineSegment StartX=-21 StartY=35.7798 StartZ=0 EndX=-21 EndY=0 EndZ=0
    g7: LineSegment StartX=-21 StartY=0 StartZ=0 EndX=0 EndY=0 EndZ=0
    g8: LineSegment StartX=0 StartY=0 StartZ=0 EndX=0 EndY=140 EndZ=0
    g9: Circle CenterX=-10.5 CenterY=12.5 CenterZ=0 NormalX=0 NormalY=0 NormalZ=-1 AngleXU=0 Radius=5.5
    g10: Circle CenterX=-10.5 CenterY=122.5 CenterZ=0 NormalX=0 NormalY=0 NormalZ=-1 AngleXU=0 Radius=5.5
    g11: GeomPoint X=-10.5 Y=0 Z=0
  constraints (39):
    c: Coincident(g6,g7)
    c: Coincident(g7,g8)
    c: Coincident(g0,g8)
    c: Coincident(g0,g1)
    c: Coincident(g2,g3)
    c: Coincident(g4,g5)
    c: Coincident(g5,g6)
    c: Vertical(g8)
    c: Vertical(g6)
    c: Vertical(g1)
    c: Horizontal(g0)
    c: Tangent(g1,g2) = 1.5708
    c: Symmetric(g6,g7,g11)
    c: Vertical(g11,g9)
    c: DistanceY(g8,g8) = 140
    c: Vertical(g9,g10)
    c: Vertical(g5,g4)
    c: Horizontal(g7)
    c: Coincident(g7,g-1)
    c: DistanceY(g9,g10) = 110
    c: Equal(g10,g9)
    c: Diameter(g10) = 11
    c: DistanceY(g7,g9) = 12.5
    c: Angle(g4,g5) = 1.5708
    c: Distance(g4) = 1.5
    c: DistanceY(g3) = 65
    c: Coincident(g3,g4)
    c: Distance(g5) = 5
    c: DistanceX(g3,g7) = 65
    c: DistanceY(g-1,g3) = 41
    c: DistanceX(g7,g7) = 21
    c: Diameter(g3) = 100.24
    c: DistanceX(g0,g0) = 21
    c: Vertical(g1,g3)
    c: Vertical(g2,g3)
    c: Diameter(g2) = 88
    c: DistanceY(g3,g2) = 65
    c: DistanceY(g1,g1) = 10
    c: DistanceY(g10,g0) = 17.5
FEATURE [PartDesign::Pad] Pad002
  Direction = (0,0,1)
  Length = 1.5
  Length2 = 10
  Profile = -> Sketch002
  Type = 0
  expr: Length = dd.ddGrosorPlaca
FEATURE [PartDesign::Pad] Pad
  Direction = (0,0,1)
  Length = 1.5
  Length2 = 10
  Profile = -> Sketch001
  Type = 0
  expr: Length = dd.ddGrosorPlaca
FEATURE [PartDesign::CoordinateSystem] LCS_eje_central  label="LCS_cucjilla_fija_separador_entrada"
  AttacherType = Attacher::AttachEngine3D
  AttachmentOffset = pos=(-65,65,0) rot=(0,0,1;0rad)
  MapMode = 5
  Placement = pos=(-65,65,0) rot=(0,0,1;0rad)
  Support = -> [XY_Plane]
  expr: .AttachmentOffset.Base.y = dd.ddAlturaEjeCentral
  expr: .AttachmentOffset.Base.x = -dd.ddAnchuraEjeCentral
FEATURE [PartDesign::CoordinateSystem] LCS_eje_central001  label="LCS_cuchilla_fija_entrada"
  AttacherType = Attacher::AttachEngine3D
  AttachmentOffset = pos=(-65,65,0) rot=(0,0,1;0rad)
  MapMode = 5
  Placement = pos=(-65,65,0) rot=(0,0,1;0rad)
  Support = -> [XY_Plane002]
  expr: .AttachmentOffset.Base.y = dd.ddAlturaEjeCentral
  expr: .AttachmentOffset.Base.x = -dd.ddAnchuraEjeCentral
FEATURE [PartDesign::CoordinateSystem] LCS_eje_central002  label="LCS_placa_caja_entrada"
  AttacherType = Attacher::AttachEngine3D
  AttachmentOffset = pos=(-65,65,0) rot=(0,0,1;0rad)
  MapMode = 5
  Placement = pos=(-65,65,0) rot=(0,0,1;0rad)
  Support = -> [XY_Plane003]
  expr: .AttachmentOffset.Base.y = dd.ddAlturaEjeCentral
  expr: .AttachmentOffset.Base.x = -dd.ddAnchuraEjeCentral
FEATURE [Sketcher::SketchObject] Sketch003
  FullyConstrained = true
  MapMode = 5
  Support = -> [XY_Plane003]
  expr: Constraints[21] = 75
  expr: Constraints[19] = dd.ddAnchuraEjeCentral
  expr: Constraints[18] = dd.ddAnchoBarra / 2
  expr: Constraints[17] = dd.ddAlturaSuperiorNotch
  expr: Constraints[33] = dd.ddAnchoBarra
  expr: Constraints[20] = dd.ddAlturaEjeCentral
  expr: Constraints[15] = dd.ddGrosorPlaca
  expr: Constraints[13] = dd.ddAlturaHueco
  expr: Constraints[12] = dd.ddDiametroHollo
  expr: Constraints[5] = dd.ddAlturaPlaca
  expr: Constraints[10] = dd.ddDistanciaHollos
  sketch-geometry (12):
    g0: LineSegment StartX=0 StartY=140 StartZ=0 EndX=-130 EndY=140 EndZ=0
    g1: LineSegment StartX=-21 StartY=41 StartZ=0 EndX=-19.5633 EndY=40.569 EndZ=0
    g2: LineSegment StartX=-19.5633 StartY=40.569 StartZ=0 EndX=-21 EndY=35.7798 EndZ=0
    g3: LineSegment StartX=-130 StartY=0 StartZ=0 EndX=0 EndY=0 EndZ=0
    g4: LineSegment StartX=0 StartY=0 StartZ=0 EndX=0 EndY=140 EndZ=0
    g5: Circle CenterX=-10.5 CenterY=12.5 CenterZ=0 NormalX=0 NormalY=0 NormalZ=-1 AngleXU=0 Radius=5.5
    g6: Circle CenterX=-10.5 CenterY=122.5 CenterZ=0 NormalX=0 NormalY=0 NormalZ=-1 AngleXU=0 Radius=5.5
    g7: Circle CenterX=-65 CenterY=65 CenterZ=0 NormalX=0 NormalY=0 NormalZ=1 AngleXU=0 Radius=37.5
    g8: LineSegment StartX=-130 StartY=140 StartZ=0 EndX=-130 EndY=0 EndZ=0
    g9: Circle CenterX=-65 CenterY=65 CenterZ=0 NormalX=0 NormalY=0 NormalZ=1 AngleXU=0 Radius=50
    g10: LineSegment StartX=-21 StartY=41 StartZ=0 EndX=-22.4367 EndY=36.2109 EndZ=0
    g11: LineSegment StartX=-22.4367 StartY=36.2109 StartZ=0 EndX=-21 EndY=35.7798 EndZ=0
  constraints (34):
    c: Coincident(g3,g4)
    c: Coincident(g0,g4)
    c: Coincident(g1,g2)
    c: Vertical(g4)
    c: Horizontal(g0)
    c: DistanceY(g4,g4) = 140
    c: Vertical(g5,g6)
    c: Vertical(g2,g1)
    c: Horizontal(g3)
    c: Coincident(g3,g-1)
    c: DistanceY(g5,g6) = 110
    c: Equal(g6,g5)
    c: Diameter(g6) = 11
    c: DistanceY(g3,g5) = 12.5
    c: Angle(g1,g2) = 1.5708
    c: Distance(g1) = 1.5
    c: Distance(g2) = 5
    c: DistanceY(g-1,g1) = 41
    c: DistanceX(g5,g3) = 10.5
    c: DistanceX(g7,g3) = 65
    c: DistanceY(g-1,g7) = 65
    c: Diameter(g7) = 75
    c: Coincident(g0,g8)
    c: Coincident(g3,g8)
    c: Vertical(g8)
    c: Diameter(g9) = 100
    c: Coincident(g7,g9)
    c: DistanceX(g0,g0) = 130
    c: Equal(g11,g1)
    c: Equal(g10,g2)
    c: Coincident(g2,g11)
    c: Coincident(g10,g11)
    c: Coincident(g1,g10)
    c: DistanceX(g2,g-1) = 21
FEATURE [PartDesign::Pad] Pad003
  Direction = (0,0,1)
  Length = 1.5
  Length2 = 10
  Profile = -> Sketch003
  Type = 0
  expr: Length = dd.ddGrosorPlaca
FEATURE [PartDesign::CoordinateSystem] LCS_placa_caja_salida
  AttacherType = Attacher::AttachEngine3D
  AttachmentOffset = pos=(0,0,0) rot=(0,0,-1;1.5708rad)
  MapMode = 11
  Placement = pos=(-65,65,1.5) rot=(0,0,1;0rad)
  Support = -> [Pad003]
FEATURE [Sketcher::SketchObject] Sketch
  ExternalGeometry = -> [Pad003]
  FullyConstrained = true
  MapMode = 5
  Placement = pos=(0,0,0) rot=(1,0,0;3.14159rad)
  Support = -> [Pad003]
  expr: Constraints[6] = dd.ddGrosorPlaca
  sketch-geometry (3):
    g0: Circle CenterX=-65 CenterY=-65 CenterZ=0 NormalX=0 NormalY=0 NormalZ=1 AngleXU=0 Radius=37.5
    g1: Circle CenterX=-65 CenterY=-65 CenterZ=0 NormalX=0 NormalY=0 NormalZ=1 AngleXU=0 Radius=39
    g2: LineSegment StartX=-27.5 StartY=-65 StartZ=0 EndX=-26 EndY=-65 EndZ=0
  constraints (8):
    c: Coincident(g0,g-3)
    c: Coincident(g1,g0)
    c: Equal(g0,g-3)
    c: PointOnObject(g2,g0)
    c: PointOnObject(g2,g1)
    c: Horizontal(g2)
    c: DistanceX(g2,g2) = 1.5
    c: Horizontal(g2,g0)
FEATURE [PartDesign::Pad] Pad004
  BaseFeature = -> Pad003
  Direction = (0,0,-1)
  Length = 10
  Length2 = 10
  Profile = -> Sketch
  Type = 0
FEATURE [PartDesign::CoordinateSystem] LCS_cuchilla_fija_salida
  AttacherType = Attacher::AttachEngine3D
  AttachmentOffset = pos=(-65,65,0) rot=(0,0,1;0rad)
  MapMode = 5
  Placement = pos=(-65,65,1.5) rot=(0,0,1;0rad)
  Support = -> [Pad002]
  expr: .AttachmentOffset.Base.y = dd.ddAlturaEjeCentral
  expr: .AttachmentOffset.Base.x = -dd.ddAnchuraEjeCentral
FEATURE [PartDesign::CoordinateSystem] LCS_cuchilla_fija_separador_salida
  AttacherType = Attacher::AttachEngine3D
  AttachmentOffset = pos=(-65,65,0) rot=(0,0,1;0rad)
  MapMode = 5
  Placement = pos=(-65,65,1.5) rot=(0,0,1;0rad)
  Support = -> [Pad]
  expr: .AttachmentOffset.Base.y = dd.ddAlturaEjeCentral
  expr: .AttachmentOffset.Base.x = -dd.ddAnchuraEjeCentral
FEATURE [PartDesign::Fillet] Fillet
  Base = -> Pad004 [Edge12]
  BaseFeature = -> Pad004
  Radius = 3
  SupportTransform = false
FEATURE [PartDesign::Fillet] Fillet001
  Base = -> Fillet [Edge36]
  BaseFeature = -> Fillet
  Radius = 3
  SupportTransform = false
FEATURE [PartDesign::CoordinateSystem] LCS_eje_central003  label="LCS_placa_caja_entrada001"
  AttacherType = Attacher::AttachEngine3D
  AttachmentOffset = pos=(-65,65,0) rot=(0,0,1;0rad)
  MapMode = 5
  Placement = pos=(-65,65,0) rot=(0,0,1;0rad)
  Support = -> [XY_Plane004]
  expr: .AttachmentOffset.Base.y = dd.ddAlturaEjeCentral
  expr: .AttachmentOffset.Base.x = -dd.ddAnchuraEjeCentral
FEATURE [Sketcher::SketchObject] Sketch005
  FullyConstrained = true
  MapMode = 5
  Support = -> [XY_Plane004]
  expr: Constraints[21] = 75
  expr: Constraints[19] = dd.ddAnchuraEjeCentral
  expr: Constraints[18] = dd.ddAnchoBarra / 2
  expr: Constraints[17] = dd.ddAlturaSuperiorNotch
  expr: Constraints[33] = dd.ddAnchoBarra
  expr: Constraints[20] = dd.ddAlturaEjeCentral
  expr: Constraints[15] = dd.ddGrosorPlaca
  expr: Constraints[13] = dd.ddAlturaHueco
  expr: Constraints[12] = dd.ddDiametroHollo
  expr: Constraints[5] = dd.ddAlturaPlaca
  expr: Constraints[10] = dd.ddDistanciaHollos
  sketch-geometry (12):
    g0: LineSegment StartX=0 StartY=140 StartZ=0 EndX=-130 EndY=140 EndZ=0
    g1: LineSegment StartX=-21 StartY=41 StartZ=0 EndX=-19.5633 EndY=40.569 EndZ=0
    g2: LineSegment StartX=-19.5633 StartY=40.569 StartZ=0 EndX=-21 EndY=35.7798 EndZ=0
    g3: LineSegment StartX=-130 StartY=0 StartZ=0 EndX=0 EndY=0 EndZ=0
    g4: LineSegment StartX=0 StartY=0 StartZ=0 EndX=0 EndY=140 EndZ=0
    g5: Circle CenterX=-10.5 CenterY=12.5 CenterZ=0 NormalX=0 NormalY=0 NormalZ=-1 AngleXU=0 Radius=5.5
    g6: Circle CenterX=-10.5 CenterY=122.5 CenterZ=0 NormalX=0 NormalY=0 NormalZ=-1 AngleXU=0 Radius=5.5
    g7: Circle CenterX=-65 CenterY=65 CenterZ=0 NormalX=0 NormalY=0 NormalZ=1 AngleXU=0 Radius=37.5
    g8: LineSegment StartX=-130 StartY=140 StartZ=0 EndX=-130 EndY=0 EndZ=0
    g9: Circle CenterX=-65 CenterY=65 CenterZ=0 NormalX=0 NormalY=0 NormalZ=1 AngleXU=0 Radius=50
    g10: LineSegment StartX=-21 StartY=41 StartZ=0 EndX=-22.4367 EndY=36.2109 EndZ=0
    g11: LineSegment StartX=-22.4367 StartY=36.2109 StartZ=0 EndX=-21 EndY=35.7798 EndZ=0
  constraints (34):
    c: Coincident(g3,g4)
    c: Coincident(g0,g4)
    c: Coincident(g1,g2)
    c: Vertical(g4)
    c: Horizontal(g0)
    c: DistanceY(g4,g4) = 140
    c: Vertical(g5,g6)
    c: Vertical(g2,g1)
    c: Horizontal(g3)
    c: Coincident(g3,g-1)
    c: DistanceY(g5,g6) = 110
    c: Equal(g6,g5)
    c: Diameter(g6) = 11
    c: DistanceY(g3,g5) = 12.5
    c: Angle(g1,g2) = 1.5708
    c: Distance(g1) = 1.5
    c: Distance(g2) = 5
    c: DistanceY(g-1,g1) = 41
    c: DistanceX(g5,g3) = 10.5
    c: DistanceX(g7,g3) = 65
    c: DistanceY(g-1,g7) = 65
    c: Diameter(g7) = 75
    c: Coincident(g0,g8)
    c: Coincident(g3,g8)
    c: Vertical(g8)
    c: Diameter(g9) = 100
    c: Coincident(g7,g9)
    c: DistanceX(g0,g0) = 130
    c: Equal(g11,g1)
    c: Equal(g10,g2)
    c: Coincident(g2,g11)
    c: Coincident(g10,g11)
    c: Coincident(g1,g10)
    c: DistanceX(g2,g-1) = 21
FEATURE [PartDesign::Pad] Pad005
  Direction = (0,0,1)
  Length = 1.5
  Length2 = 10
  Profile = -> Sketch005
  Type = 0
  expr: Length = dd.ddGrosorPlaca
FEATURE [PartDesign::CoordinateSystem] LCS_placa_caja_salida001
  AttacherType = Attacher::AttachEngine3D
  AttachmentOffset = pos=(0,0,0) rot=(0,0,-1;1.5708rad)
  MapMode = 11
  Placement = pos=(-65,65,1.5) rot=(0,0,1;0rad)
  Support = -> [Pad005]
FEATURE [Sketcher::SketchObject] Sketch004
  ExternalGeometry = -> [Pad005]
  FullyConstrained = true
  MapMode = 5
  Placement = pos=(0,0,1.5) rot=(0,0,1;0rad)
  Support = -> [Pad005]
  expr: Constraints[6] = dd.ddGrosorPlaca
  sketch-geometry (3):
    g0: Circle CenterX=-65 CenterY=65 CenterZ=0 NormalX=0 NormalY=0 NormalZ=1 AngleXU=0 Radius=37.5
    g1: Circle CenterX=-65 CenterY=65 CenterZ=0 NormalX=0 NormalY=0 NormalZ=1 AngleXU=0 Radius=39
    g2: LineSegment StartX=-27.5 StartY=65 StartZ=0 EndX=-26 EndY=65 EndZ=0
  constraints (8):
    c: Coincident(g0,g-3)
    c: Coincident(g1,g0)
    c: Equal(g0,g-3)
    c: PointOnObject(g2,g0)
    c: PointOnObject(g2,g1)
    c: Horizontal(g2)
    c: DistanceX(g2,g2) = 1.5
    c: Horizontal(g2,g0)
FEATURE [PartDesign::Pad] Pad006
  BaseFeature = -> Pad005
  Direction = (0,0,1)
  Length = 10
  Length2 = 10
  Profile = -> Sketch004
  Type = 0
FEATURE [PartDesign::Fillet] Fillet002
  Base = -> Pad006 [Edge12]
  BaseFeature = -> Pad006
  Radius = 3
  SupportTransform = false
FEATURE [PartDesign::Fillet] Fillet003
  Base = -> Fillet002 [Edge36]
  BaseFeature = -> Fillet002
  Radius = 3
  SupportTransform = false
FEATURE [Sketcher::SketchObject] Sketch006
  ExternalGeometry = -> [Fillet003]
  FullyConstrained = true
  MapMode = 5
  Placement = pos=(0,0,1.5) rot=(0,0,1;0rad)
  Support = -> [Fillet003]
  expr: Constraints[33] = dd.ddNotchHeight
  expr: Constraints[19] = dd.ddGrosorPlaca
  expr: Constraints[18] = dd.ddNotchHeight
  sketch-geometry (14):
    g0: LineSegment StartX=-117.5 StartY=120 StartZ=0 EndX=-116 EndY=120 EndZ=0
    g1: LineSegment StartX=-116 StartY=120 StartZ=0 EndX=-116 EndY=100 EndZ=0
    g2: LineSegment StartX=-116 StartY=100 StartZ=0 EndX=-117.5 EndY=100 EndZ=0
    g3: LineSegment StartX=-117.5 StartY=100 StartZ=0 EndX=-117.5 EndY=120 EndZ=0
    g4: LineSegment StartX=-117.5 StartY=40 StartZ=0 EndX=-116 EndY=40 EndZ=0
    g5: LineSegment StartX=-116 StartY=40 StartZ=0 EndX=-116 EndY=20 EndZ=0
    g6: LineSegment StartX=-116 StartY=20 StartZ=0 EndX=-117.5 EndY=20 EndZ=0
    g7: LineSegment StartX=-117.5 StartY=20 StartZ=0 EndX=-117.5 EndY=40 EndZ=0
    g8: GeomPoint X=-116 Y=30 Z=0
    g9: GeomPoint X=-116 Y=110 Z=0
    g10: LineSegment StartX=-65 StartY=65 StartZ=0 EndX=-116 EndY=65 EndZ=0
    g11: GeomPoint X=-130 Y=0 Z=0
    g12: GeomPoint X=-130 Y=70 Z=0
    g13: LineSegment StartX=-130 StartY=70 StartZ=0 EndX=0 EndY=70 EndZ=0
  constraints (34):
    c: Coincident(g0,g1)
    c: Coincident(g1,g2)
    c: Coincident(g2,g3)
    c: Coincident(g3,g0)
    c: Horizontal(g0)
    c: Horizontal(g2)
    c: Vertical(g1)
    c: Vertical(g3)
    c: Coincident(g4,g5)
    c: Coincident(g5,g6)
    c: Coincident(g6,g7)
    c: Coincident(g7,g4)
    c: Horizontal(g4)
    c: Horizontal(g6)
    c: Vertical(g5)
    c: Vertical(g7)
    c: Equal(g1,g5)
    c: Equal(g2,g4)
    c: DistanceY(g3,g3) = 20
    c: DistanceX(g0,g0) = 1.5
    c: Vertical(g2,g4)
    c: Symmetric(g4,g5,g8)
    c: Symmetric(g1,g0,g9)
    c: Coincident(g10,g-6)
    c: Horizontal(g10)
    c: DistanceX(g10,g10) = 51
    c: Vertical(g1,g10)
    c: PointOnObject(g11,g-1)
    c: Vertical(g-3,g12)
    c: Symmetric(g-3,g11,g12)
    c: Coincident(g13,g12)
    c: PointOnObject(g13,g-2)
    c: Symmetric(g4,g1,g13)
    c: DistanceY(g-1,g6) = 20
FEATURE [PartDesign::Pocket] Pocket
  BaseFeature = -> Fillet003
  Length = 5
  Length2 = 5
  Profile = -> Sketch006
  Type = 2
FEATURE [Sketcher::SketchObject] Sketch007
  ExternalGeometry = -> [Fillet001]
  FullyConstrained = true
  MapMode = 5
  Placement = pos=(0,0,1.5) rot=(0,0,1;0rad)
  Support = -> [Fillet001]
  expr: Constraints[33] = dd.ddNotchHeight
  expr: Constraints[19] = dd.ddGrosorPlaca
  expr: Constraints[18] = dd.ddNotchHeight
  sketch-geometry (14):
    g0: LineSegment StartX=-117.5 StartY=120 StartZ=0 EndX=-116 EndY=120 EndZ=0
    g1: LineSegment StartX=-116 StartY=120 StartZ=0 EndX=-116 EndY=100 EndZ=0
    g2: LineSegment StartX=-116 StartY=100 StartZ=0 EndX=-117.5 EndY=100 EndZ=0
    g3: LineSegment StartX=-117.5 StartY=100 StartZ=0 EndX=-117.5 EndY=120 EndZ=0
    g4: LineSegment StartX=-116 StartY=40 StartZ=0 EndX=-117.5 EndY=40 EndZ=0
    g5: LineSegment StartX=-117.5 StartY=40 StartZ=0 EndX=-117.5 EndY=20 EndZ=0
    g6: LineSegment StartX=-117.5 StartY=20 StartZ=0 EndX=-116 EndY=20 EndZ=0
    g7: LineSegment StartX=-116 StartY=20 StartZ=0 EndX=-116 EndY=40 EndZ=0
    g8: GeomPoint X=-116 Y=110 Z=0
    g9: GeomPoint X=-116 Y=30 Z=0
    g10: LineSegment StartX=-65 StartY=65 StartZ=0 EndX=-116 EndY=65 EndZ=0
    g11: GeomPoint X=-130 Y=70 Z=0
    g12: GeomPoint X=-130 Y=0 Z=0
    g13: LineSegment StartX=-130 StartY=70 StartZ=0 EndX=0 EndY=70 EndZ=0
  constraints (34):
    c: Coincident(g0,g1)
    c: Coincident(g1,g2)
    c: Coincident(g2,g3)
    c: Coincident(g3,g0)
    c: Horizontal(g0)
    c: Horizontal(g2)
    c: Vertical(g1)
    c: Vertical(g3)
    c: Coincident(g4,g5)
    c: Coincident(g5,g6)
    c: Coincident(g6,g7)
    c: Coincident(g7,g4)
    c: Horizontal(g4)
    c: Horizontal(g6)
    c: Vertical(g5)
    c: Vertical(g7)
    c: Equal(g4,g2)
    c: Equal(g1,g5)
    c: DistanceY(g3,g3) = 20
    c: DistanceX(g0,g0) = 1.5
    c: Symmetric(g0,g1,g8)
    c: Symmetric(g4,g6,g9)
    c: Vertical(g4,g2)
    c: Coincident(g10,g-5)
    c: Horizontal(g10)
    c: Vertical(g10,g1)
    c: DistanceX(g10,g10) = 51
    c: Vertical(g11,g-6)
    c: PointOnObject(g12,g-1)
    c: Symmetric(g-6,g12,g11)
    c: Coincident(g13,g11)
    c: PointOnObject(g13,g-2)
    c: Symmetric(g4,g1,g13)
    c: DistanceY(g12,g5) = 20
FEATURE [PartDesign::Pocket] Pocket001
  BaseFeature = -> Fillet001
  Length = 5
  Length2 = 5
  Profile = -> Sketch007
  Type = 2
FEATURE [Sketcher::SketchObject] Sketch008
  FullyConstrained = true
  MapMode = 5
  Support = -> [XY_Plane005]
  expr: Constraints[99] = dd.ddGrosorPlaca
  expr: Constraints[60] = dd.ddNotchHeight
  expr: Constraints[42] = dd.ddNotchHeight
  expr: Constraints[55] = 1.5 * 2 * (6 * 3 * 2 + 0.5)
  expr: Constraints[41] = dd.ddAlturaPlaca
  expr: Constraints[40] = dd.ddGrosorPlaca * 2
  expr: Constraints[100] = dd.ddNotchHeight / 2
  sketch-geometry (39):
    g0: LineSegment StartX=-54.75 StartY=70 StartZ=0 EndX=54.75 EndY=70 EndZ=0
    g1: LineSegment StartX=54.75 StartY=70 StartZ=0 EndX=54.75 EndY=50 EndZ=0
    g2: LineSegment StartX=54.75 StartY=50 StartZ=0 EndX=57.75 EndY=50 EndZ=0
    g3: LineSegment StartX=57.75 StartY=50 StartZ=0 EndX=57.75 EndY=30 EndZ=0
    g4: LineSegment StartX=57.75 StartY=30 StartZ=0 EndX=54.75 EndY=30 EndZ=0
    g5: LineSegment StartX=54.75 StartY=30 StartZ=0 EndX=54.75 EndY=-30 EndZ=0
    g6: LineSegment StartX=54.75 StartY=-30 StartZ=0 EndX=57.75 EndY=-30 EndZ=0
    g7: LineSegment StartX=57.75 StartY=-30 StartZ=0 EndX=57.75 EndY=-50 EndZ=0
    g8: LineSegment StartX=57.75 StartY=-50 StartZ=0 EndX=54.75 EndY=-50 EndZ=0
    g9: LineSegment StartX=54.75 StartY=-50 StartZ=0 EndX=54.75 EndY=-70 EndZ=0
    g10: LineSegment StartX=54.75 StartY=-70 StartZ=0 EndX=-54.75 EndY=-70 EndZ=0
    g11: LineSegment StartX=-54.75 StartY=-70 StartZ=0 EndX=-54.75 EndY=-50 EndZ=0
    g12: LineSegment StartX=-54.75 StartY=-50 StartZ=0 EndX=-57.75 EndY=-50 EndZ=0
    g13: LineSegment StartX=-57.75 StartY=-50 StartZ=0 EndX=-57.75 EndY=-30 EndZ=0
    g14: LineSegment StartX=-57.75 StartY=-30 StartZ=0 EndX=-54.75 EndY=-30 EndZ=0
    g15: LineSegment StartX=-54.75 StartY=-30 StartZ=0 EndX=-54.75 EndY=30 EndZ=0
    g16: LineSegment StartX=-54.75 StartY=30 StartZ=0 EndX=-57.75 EndY=30 EndZ=0
    g17: LineSegment StartX=-57.75 StartY=30 StartZ=0 EndX=-57.75 EndY=50 EndZ=0
    g18: LineSegment StartX=-57.75 StartY=50 StartZ=0 EndX=-54.75 EndY=50 EndZ=0
    g19: LineSegment StartX=-54.75 StartY=50 StartZ=0 EndX=-54.75 EndY=70 EndZ=0
    g20: GeomPoint X=-57.75 Y=40 Z=0
    g21: GeomPoint X=-57.75 Y=-40 Z=0
    g22: LineSegment StartX=-54.75 StartY=45 StartZ=0 EndX=-53.25 EndY=45 EndZ=0
    g23: LineSegment StartX=-53.25 StartY=45 StartZ=0 EndX=-53.25 EndY=35 EndZ=0
    g24: LineSegment StartX=-53.25 StartY=35 StartZ=0 EndX=-54.75 EndY=35 EndZ=0
    g25: LineSegment StartX=-54.75 StartY=35 StartZ=0 EndX=-54.75 EndY=45 EndZ=0
    g26: LineSegment StartX=53.25 StartY=45 StartZ=0 EndX=54.75 EndY=45 EndZ=0
    g27: LineSegment StartX=54.75 StartY=45 StartZ=0 EndX=54.75 EndY=35 EndZ=0
    g28: LineSegment StartX=54.75 StartY=35 StartZ=0 EndX=53.25 EndY=35 EndZ=0
    g29: LineSegment StartX=53.25 StartY=35 StartZ=0 EndX=53.25 EndY=45 EndZ=0
    g30: LineSegment StartX=53.25 StartY=-35 StartZ=0 EndX=54.75 EndY=-35 EndZ=0
    g31: LineSegment StartX=54.75 StartY=-35 StartZ=0 EndX=54.75 EndY=-45 EndZ=0
    g32: LineSegment StartX=54.75 StartY=-45 StartZ=0 EndX=53.25 EndY=-45 EndZ=0
    g33: LineSegment StartX=53.25 StartY=-45 StartZ=0 EndX=53.25 EndY=-35 EndZ=0
    g34: LineSegment StartX=-54.75 StartY=-35 StartZ=0 EndX=-53.25 EndY=-35 EndZ=0
    g35: LineSegment StartX=-53.25 StartY=-35 StartZ=0 EndX=-53.25 EndY=-45 EndZ=0
    g36: LineSegment StartX=-53.25 StartY=-45 StartZ=0 EndX=-54.75 EndY=-45 EndZ=0
    g37: LineSegment StartX=-54.75 StartY=-45 StartZ=0 EndX=-54.75 EndY=-35 EndZ=0
    g38: GeomPoint X=-54.75 Y=40 Z=0
  constraints (109):
    c: Horizontal(g0)
    c: Coincident(g0,g1)
    c: Vertical(g1)
    c: Coincident(g1,g2)
    c: Coincident(g2,g3)
    c: Vertical(g3)
    c: Coincident(g3,g4)
    c: Vertical(g5)
    c: Coincident(g6,g7)
    c: Vertical(g7)
    c: Coincident(g7,g8)
    c: Horizontal(g8)
    c: Coincident(g8,g9)
    c: Vertical(g9)
    c: Coincident(g9,g10)
    c: Horizontal(g10)
    c: Coincident(g10,g11)
    c: Vertical(g11)
    c: Coincident(g11,g12)
    c: Horizontal(g12)
    c: Coincident(g12,g13)
    c: Vertical(g13)
    c: Coincident(g13,g14)
    c: Horizontal(g14)
    c: Coincident(g14,g15)
    c: Vertical(g15)
    c: Coincident(g16,g17)
    c: Vertical(g17)
    c: Coincident(g17,g18)
    c: Horizontal(g18)
    c: Coincident(g18,g19)
    c: Vertical(g19)
    c: Coincident(g0,g19)
    c: Equal(g0,g10)
    c: Equal(g7,g13)
    c: Equal(g13,g3)
    c: Horizontal(g2)
    c: Equal(g2,g4)
    c: Equal(g16,g18)
    c: Equal(g3,g17)
    c: DistanceX(g2,g2) = 3
    c: DistanceY(g9,g0) = 140
    c: DistanceY(g17,g17) = 20
    c: Symmetric(g9,g0,g-1)
    c: Symmetric(g13,g12,g21)
    c: Symmetric(g17,g16,g20)
    c: Horizontal(g16)
    c: Coincident(g15,g16)
    c: Vertical(g12,g14)
    c: Coincident(g4,g5)
    c: Vertical(g1,g4)
    c: Horizontal(g6)
    c: Coincident(g5,g6)
    c: Equal(g4,g6)
    c: Equal(g6,g14)
    c: DistanceX(g0,g0) = 109.5
    c: Equal(g11,g9)
    c: Equal(g19,g1)
    c: Vertical(g16,g13)
    c: Equal(g19,g11)
    c: DistanceY(g11,g11) = 20
    c: Coincident(g22,g23)
    c: Coincident(g23,g24)
    c: Coincident(g24,g25)
    c: Coincident(g25,g22)
    c: Horizontal(g22)
    c: Horizontal(g24)
    c: Vertical(g23)
    c: Vertical(g25)
    c: Coincident(g26,g27)
    c: Coincident(g27,g28)
    c: Coincident(g28,g29)
    c: Coincident(g29,g26)
    c: Horizontal(g26)
    c: Horizontal(g28)
    c: Vertical(g27)
    c: Vertical(g29)
    c: Coincident(g30,g31)
    c: Coincident(g31,g32)
    c: Coincident(g32,g33)
    c: Coincident(g33,g30)
    c: Horizontal(g30)
    c: Horizontal(g32)
    c: Vertical(g31)
    c: Vertical(g33)
    c: Coincident(g34,g35)
    c: Coincident(g35,g36)
    c: Coincident(g36,g37)
    c: Coincident(g37,g34)
    c: Horizontal(g34)
    c: Horizontal(g36)
    c: Vertical(g35)
    c: Vertical(g37)
    c: Equal(g30,g28)
    c: Equal(g28,g34)
    c: Equal(g34,g24)
    c: Equal(g23,g35)
    c: Equal(g35,g33)
    c: Equal(g33,g29)
    c: DistanceX(g36,g36) = 1.5
    c: DistanceY(g35,g35) = 10
    c: Horizontal(g30,g34)
    c: Horizontal(g23,g28)
    c: Vertical(g28,g30)
    c: Vertical(g34,g23)
    c: Symmetric(g23,g30,g-1)
    c: Vertical(g30,g5)
    c: Symmetric(g22,g24,g38)
    c: Horizontal(g20,g38)
FEATURE [PartDesign::Pad] Pad007
  Direction = (0,0,1)
  Length = 1.5
  Length2 = 10
  Profile = -> Sketch008
  Type = 0
  expr: Length = dd.ddGrosorPlaca
FEATURE [PartDesign::CoordinateSystem] LCS_Placa_Fondo_Entrada
  AttacherType = Attacher::AttachEngine3D
  MapMode = 49
  Placement = pos=(-54.75,50,1.5) rot=(0.707107,0,-0.707107;3.14159rad)
  Support = -> [Pad007]
FEATURE [PartDesign::Body] Body001  label="PlacaFondo"
  Group = -> [Sketch008,Pad007,LCS_Placa_Fondo_Entrada]
  Origin = -> Origin005
  Tip = -> Pad007
FEATURE [PartDesign::CoordinateSystem] LCS_Placa_Salida_Fondo
  AttacherType = Attacher::AttachEngine3D
  MapMode = 49
  Placement = pos=(-117.5,120,1.5) rot=(1,0,0;3.14159rad)
  Support = -> [Pocket001]
FEATURE [Sketcher::SketchObject] Sketch009
  FullyConstrained = true
  MapMode = 5
  Support = -> [XY_Plane006]
  expr: Constraints[33] = dd.ddAlturaPlaca
  expr: Constraints[30] = dd.ddNotchHeight / 2
  expr: Constraints[32] = dd.ddNotchHeight * 1.5
  expr: Constraints[29] = dd.ddGrosorPlaca * 2
  sketch-geometry (13):
    g0: LineSegment StartX=-6.25 StartY=70 StartZ=0 EndX=6.25 EndY=70 EndZ=0
    g1: LineSegment StartX=6.25 StartY=70 StartZ=0 EndX=6.25 EndY=-70 EndZ=0
    g2: LineSegment StartX=6.25 StartY=-70 StartZ=0 EndX=-6.25 EndY=-70 EndZ=0
    g3: LineSegment StartX=-6.25 StartY=-70 StartZ=0 EndX=-6.25 EndY=-45 EndZ=0
    g4: LineSegment StartX=-6.25 StartY=-45 StartZ=0 EndX=-9.25 EndY=-45 EndZ=0
    g5: LineSegment StartX=-9.25 StartY=-45 StartZ=0 EndX=-9.25 EndY=-35 EndZ=0
    g6: LineSegment StartX=-9.25 StartY=-35 StartZ=0 EndX=-6.25 EndY=-35 EndZ=0
    g7: LineSegment StartX=-6.25 StartY=-35 StartZ=0 EndX=-6.25 EndY=35 EndZ=0
    g8: LineSegment StartX=-6.25 StartY=35 StartZ=0 EndX=-9.25 EndY=35 EndZ=0
    g9: LineSegment StartX=-9.25 StartY=35 StartZ=0 EndX=-9.25 EndY=45 EndZ=0
    g10: LineSegment StartX=-9.25 StartY=45 StartZ=0 EndX=-6.25 EndY=45 EndZ=0
    g11: LineSegment StartX=-6.25 StartY=45 StartZ=0 EndX=-6.25 EndY=70 EndZ=0
    g12: GeomPoint X=-6.25 Y=-40 Z=0
  constraints (36):
    c: Horizontal(g0)
    c: Coincident(g0,g1)
    c: Vertical(g1)
    c: Coincident(g1,g2)
    c: Horizontal(g2)
    c: Coincident(g2,g3)
    c: Coincident(g3,g4)
    c: Horizontal(g4)
    c: Coincident(g4,g5)
    c: Vertical(g5)
    c: Coincident(g5,g6)
    c: Horizontal(g6)
    c: Coincident(g6,g7)
    c: Vertical(g7)
    c: Coincident(g7,g8)
    c: Horizontal(g8)
    c: Coincident(g8,g9)
    c: Vertical(g9)
    c: Coincident(g9,g10)
    c: Horizontal(g10)
    c: Coincident(g10,g11)
    c: Coincident(g11,g0)
    c: Vertical(g11)
    c: Vertical(g7,g10)
    c: Vertical(g6,g3)
    c: Vertical(g3)
    c: Equal(g3,g11)
    c: Equal(g9,g5)
    c: Equal(g8,g6)
    c: DistanceX(g6,g6) = 3
    c: DistanceY(g5,g5) = 10
    c: Symmetric(g3,g6,g12)
    c: DistanceY(g2,g12) = 30
    c: DistanceY(g1,g1) = 140
    c: DistanceX(g0,g0) = 12.5
    c: Symmetric(g0,g1,g-1)
FEATURE [PartDesign::Pad] Pad008
  Direction = (0,0,1)
  Length = 1.5
  Length2 = 10
  Profile = -> Sketch009
  Type = 0
  expr: Length = dd.ddGrosorPlaca
FEATURE [Sketcher::SketchObject] Sketch010
  ExternalGeometry = -> [Pad008]
  FullyConstrained = true
  MapMode = 5
  Placement = pos=(0,0,1.5) rot=(0,0,1;0rad)
  Support = -> [Pad008]
  sketch-geometry (3):
    g0: Circle CenterX=0 CenterY=35 CenterZ=0 NormalX=0 NormalY=0 NormalZ=1 AngleXU=0 Radius=2.5
    g1: Circle CenterX=0 CenterY=-35 CenterZ=0 NormalX=0 NormalY=0 NormalZ=1 AngleXU=0 Radius=2.5
    g2: GeomPoint X=0 Y=-70 Z=0
  constraints (6):
    c: PointOnObject(g0,g-2)
    c: Equal(g1,g0)
    c: Symmetric(g0,g1,g-1)
    c: Diameter(g0) = 5
    c: PointOnObject(g2,g-3)
    c: Symmetric(g-1,g2,g1)
FEATURE [PartDesign::Hole] Hole
  BaseFeature = -> Pad008
  Depth = 286.607
  DepthType = 1
  Diameter = 5.5
  DrillForDepth = false
  DrillPoint = 1
  DrillPointAngle = 118
  HoleCutCountersinkAngle = 90
  HoleCutCustomValues = false
  HoleCutDepth = 0
  HoleCutDiameter = 0
  HoleCutType = 0
  ModelActualThread = false
  Profile = -> Sketch010
  Tapered = false
  TaperedAngle = 90
  ThreadAngle = 0
  ThreadClass = 0
  ThreadCutOffInner = 0
  ThreadCutOffOuter = 0
  ThreadDirection = 0
  ThreadFit = 0
  ThreadPitch = 0
  ThreadSize = 13
  ThreadType = 1
  Threaded = false
FEATURE [Sketcher::SketchObject] Sketch011
  ExternalGeometry = -> [Pocket001]
  FullyConstrained = true
  MapMode = 5
  Placement = pos=(0,0,1.5) rot=(0,0,1;0rad)
  Support = -> [Pocket001]
  sketch-geometry (8):
    g0: Circle CenterX=-123.75 CenterY=105 CenterZ=0 NormalX=0 NormalY=0 NormalZ=1 AngleXU=0 Radius=5
    g1: Circle CenterX=-123.75 CenterY=35 CenterZ=0 NormalX=0 NormalY=0 NormalZ=1 AngleXU=0 Radius=5
    g2: GeomPoint X=-130 Y=0 Z=0
    g3: GeomPoint X=-117.5 Y=0 Z=0
    g4: GeomPoint X=-123.75 Y=0 Z=0
    g5: GeomPoint X=-130 Y=70 Z=0
    g6: LineSegment StartX=-130 StartY=70 StartZ=0 EndX=0 EndY=70 EndZ=0
    g7: GeomPoint X=-123.75 Y=70 Z=0
  constraints (14):
    c: Vertical(g1,g0)
    c: Equal(g0,g1)
    c: Diameter(g0) = 10
    c: PointOnObject(g3,g-1)
    c: Vertical(g-4,g3)
    c: Symmetric(g2,g3,g4)
    c: Coincident(g2,g-5)
    c: Vertical(g4,g1)
    c: Symmetric(g-5,g2,g5)
    c: Coincident(g6,g5)
    c: PointOnObject(g6,g-2)
    c: Symmetric(g1,g0,g6)
    c: PointOnObject(g7,g6)
    c: Symmetric(g4,g7,g1)
FEATURE [PartDesign::Hole] Hole001
  BaseFeature = -> Pocket001
  Depth = 386.619
  DepthType = 1
  Diameter = 5.5
  DrillForDepth = false
  DrillPoint = 1
  DrillPointAngle = 118
  HoleCutCountersinkAngle = 90
  HoleCutCustomValues = false
  HoleCutDepth = 0
  HoleCutDiameter = 6.1
  HoleCutType = 0
  ModelActualThread = false
  Profile = -> Sketch011
  Tapered = false
  TaperedAngle = 90
  ThreadAngle = 0
  ThreadClass = 0
  ThreadCutOffInner = 0
  ThreadCutOffOuter = 0
  ThreadDirection = 0
  ThreadFit = 0
  ThreadPitch = 0
  ThreadSize = 13
  ThreadType = 1
  Threaded = false
FEATURE [Sketcher::SketchObject] Sketch012
  ExternalGeometry = -> [Pocket]
  FullyConstrained = true
  MapMode = 5
  Placement = pos=(0,0,1.5) rot=(0,0,1;0rad)
  Support = -> [Pocket]
  sketch-geometry (7):
    g0: Circle CenterX=-123.75 CenterY=105 CenterZ=0 NormalX=0 NormalY=0 NormalZ=1 AngleXU=0 Radius=2.5
    g1: Circle CenterX=-123.75 CenterY=35 CenterZ=0 NormalX=0 NormalY=0 NormalZ=1 AngleXU=0 Radius=2.5
    g2: GeomPoint X=-117.5 Y=0 Z=0
    g3: GeomPoint X=-123.75 Y=0 Z=0
    g4: GeomPoint X=-130 Y=70 Z=0
    g5: LineSegment StartX=-130 StartY=70 StartZ=0 EndX=0 EndY=70 EndZ=0
    g6: GeomPoint X=-123.75 Y=70 Z=0
  constraints (13):
    c: Equal(g1,g0)
    c: Diameter(g1) = 5
    c: PointOnObject(g2,g-1)
    c: Vertical(g2,g-3)
    c: Symmetric(g-4,g2,g3)
    c: Vertical(g1,g3)
    c: Vertical(g3,g0)
    c: Symmetric(g-4,g-4,g4)
    c: Coincident(g5,g4)
    c: PointOnObject(g5,g-2)
    c: Symmetric(g1,g0,g5)
    c: PointOnObject(g6,g5)
    c: Symmetric(g3,g6,g1)
FEATURE [PartDesign::Hole] Hole002
  BaseFeature = -> Pocket
  Depth = 386.619
  DepthType = 1
  Diameter = 5.5
  DrillForDepth = false
  DrillPoint = 1
  DrillPointAngle = 118
  HoleCutCountersinkAngle = 90
  HoleCutCustomValues = false
  HoleCutDepth = 0
  HoleCutDiameter = 6.1
  HoleCutType = 0
  ModelActualThread = false
  Profile = -> Sketch012
  Tapered = false
  TaperedAngle = 90
  ThreadAngle = 0
  ThreadClass = 0
  ThreadCutOffInner = 0
  ThreadCutOffOuter = 0
  ThreadDirection = 0
  ThreadFit = 0
  ThreadPitch = 0
  ThreadSize = 13
  ThreadType = 1
  Threaded = false
FEATURE [PartDesign::CoordinateSystem] LCS_Placa_union_salida
  AttacherType = Attacher::AttachEngine3D
  MapMode = 11
  Placement = pos=(-123.75,35,0) rot=(0.707107,-0.707107,0;3.14159rad)
  Support = -> [Hole002]
FEATURE [PartDesign::CoordinateSystem] LCS_Placa_Union_Entrada
  AttacherType = Attacher::AttachEngine3D
  MapMode = 11
  Placement = pos=(0,-35,0) rot=(0,0,1;1.5708rad)
  Support = -> [Hole]
FEATURE [PartDesign::CoordinateSystem] LCS_Placa_union_salida001
  AttacherType = Attacher::AttachEngine3D
  MapMode = 11
  Placement = pos=(-123.75,35,1.5) rot=(0.707107,-0.707107,0;3.14159rad)
  Support = -> [Hole001]
FEATURE [PartDesign::Body] CuchillaFija001  label="PlacaCaja"
  Group = -> [Sketch003,Pad003,LCS_eje_central002,LCS_placa_caja_salida,Sketch,Pad004,Fillet,Fillet001,Sketch007,Pocket001,LCS_Placa_Salida_Fondo,Sketch011,Hole001,LCS_Placa_union_salida001]
  Origin = -> Origin003
  Tip = -> Hole001
FEATURE [PartDesign::CoordinateSystem] LCS_Paca_union_entrada_2
  AttacherType = Attacher::AttachEngine3D
  MapMode = 11
  Placement = pos=(0,-35,1.5) rot=(0.707107,-0.707107,0;3.14159rad)
  Support = -> [Hole]
FEATURE [PartDesign::Body] Body002  label="Placa_union"
  Group = -> [Sketch009,Pad008,Sketch010,Hole,LCS_Placa_Union_Entrada,LCS_Paca_union_entrada_2]
  Origin = -> Origin006
  Tip = -> Hole
FEATURE [PartDesign::Line] HoleAxis_1
  AttacherType = Attacher::AttachEngineLine
  Length = 7.74987
  MapMode = 19
  Placement = pos=(-123.75,35,1.5) rot=(0,0,1;0rad)
  ResizeMode = 1
  Support = -> [Hole002]
FEATURE [PartDesign::Body] CuchillaFija002  label="PlacaCajaSalida"
  Group = -> [Sketch005,Pad005,LCS_eje_central003,LCS_placa_caja_salida001,Sketch004,Pad006,Fillet002,Fillet003,Sketch006,Pocket,Sketch012,Hole002,LCS_Placa_union_salida,HoleAxis_1]
  Origin = -> Origin004
  Tip = -> Hole002
FEATURE [PartDesign::Chamfer] Chamfer
  Angle = 45
  Base = -> Pad [Edge20]
  BaseFeature = -> Pad
  ChamferType = 0
  FlipDirection = false
  Size = 7.5
  Size2 = 1
  SupportTransform = false
FEATURE [PartDesign::Body] Body  label="CuchillaFijaSeparador"
  Group = -> [Sketch001,Pad,LCS_eje_central,LCS_cuchilla_fija_separador_salida,Chamfer]
  Origin = -> Origin
  Tip = -> Chamfer
FEATURE [PartDesign::Chamfer] Chamfer001
  Angle = 45
  Base = -> Pad002 [Edge2]
  BaseFeature = -> Pad002
  ChamferType = 0
  FlipDirection = false
  Size = 7.5
  Size2 = 1
  SupportTransform = false
FEATURE [PartDesign::Body] CuchillaFija
  Group = -> [Sketch002,Pad002,LCS_eje_central001,LCS_cuchilla_fija_salida,Chamfer001]
  Origin = -> Origin002
  Tip = -> Chamfer001
